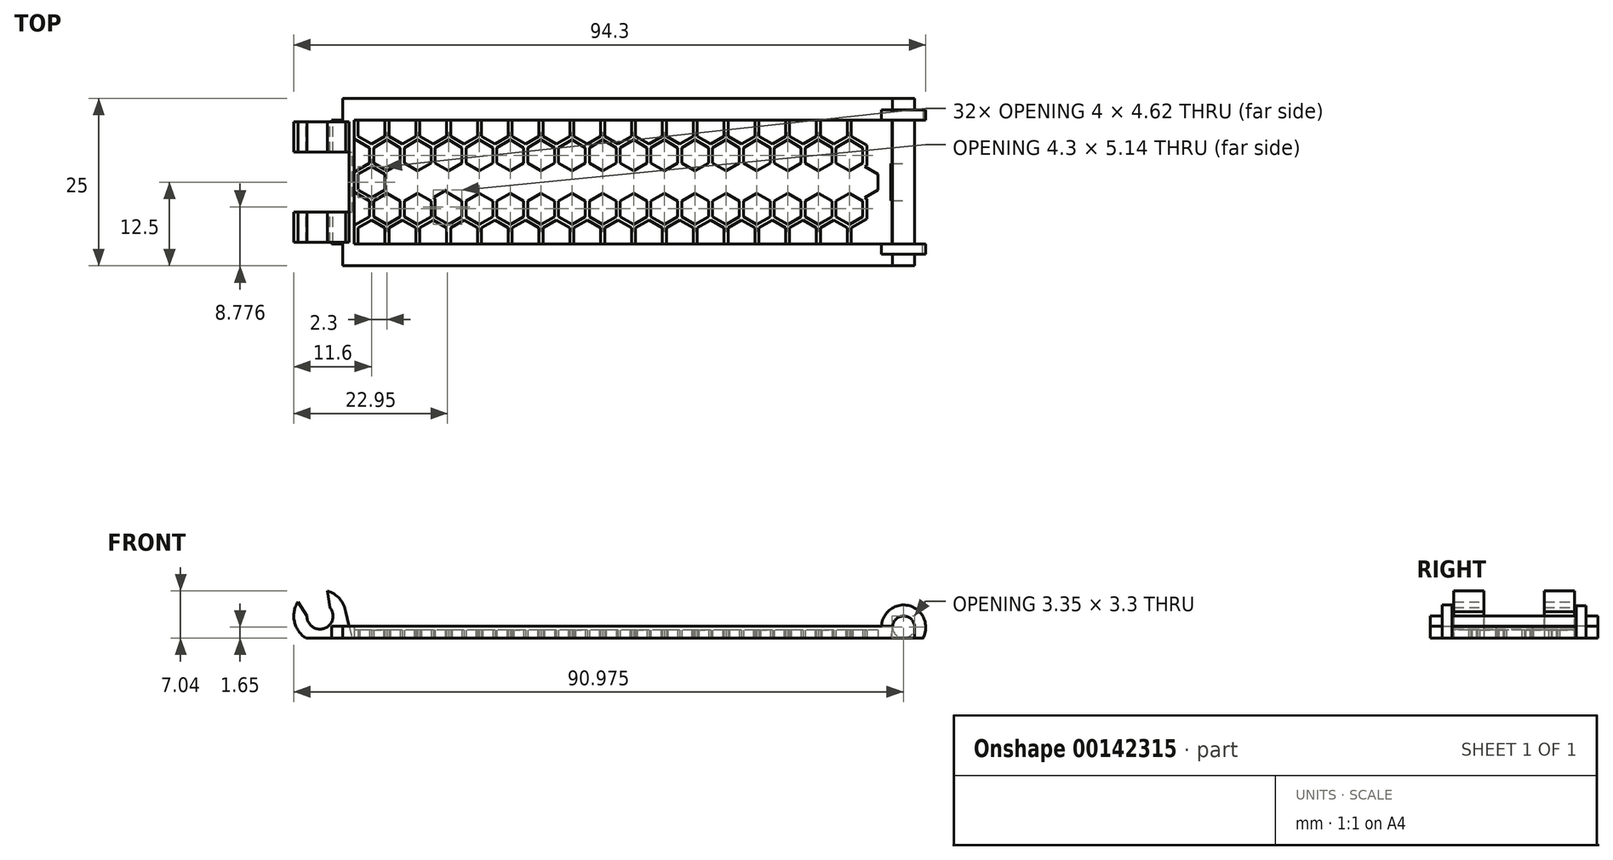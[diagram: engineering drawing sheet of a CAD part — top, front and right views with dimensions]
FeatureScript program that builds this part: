
annotation { "Feature Type Name" : "Feature", "Feature Type Description" : "" }
export const myFeature = defineFeature(function(context is Context, id is Id, definition is map)
    precondition{}
    {
        {
            var Q0;
            Q0=qCreatedBy(makeId("Top.planeOp"),FACE);
            var sketch = newSketch(context, id + "F0", { "sketchPlane" : qUnion([Q0])});
            skLineSegment(sketch, "E0.bottom", {"start": v(-40.15, -9.25) * mm, "end": v(40.15, -9.25) * mm});
            skLineSegment(sketch, "E0.top", {"start": v(-40.15, 9.25) * mm, "end": v(40.15, 9.25) * mm});
            skLineSegment(sketch, "E0.left", {"start": v(-40.15, -9.25) * mm, "end": v(-40.15, 9.25) * mm});
            skLineSegment(sketch, "E0.right", {"start": v(40.15, -9.25) * mm, "end": v(40.15, 9.25) * mm});
            skLineSegment(sketch, "E1.bottom", {"start": v(-43.5, -12.5) * mm, "end": v(43.5, -12.5) * mm});
            skLineSegment(sketch, "E1.top", {"start": v(-43.5, 12.5) * mm, "end": v(43.5, 12.5) * mm});
            skLineSegment(sketch, "E1.left", {"start": v(-43.5, -12.5) * mm, "end": v(-43.5, 12.5) * mm});
            skLineSegment(sketch, "E1.right", {"start": v(43.5, -12.5) * mm, "end": v(43.5, 12.5) * mm});
            skLineSegment(sketch, "E2", {"start": v(-43.5, -9.25) * mm, "end": v(-41.85, -9.25) * mm});
            skLineSegment(sketch, "E3", {"start": v(-41.85, -9.25) * mm, "end": v(-41.85, -12.5) * mm});
            skLineSegment(sketch, "E4", {"start": v(-56.32, 0) * mm, "end": v(-53.02, 0) * mm, "construction": true});
            skLineSegment(sketch, "E5.MirrorCS", {"start": v(-43.5, 9.25) * mm, "end": v(-41.85, 9.25) * mm});
            skLineSegment(sketch, "E6.MirrorCS", {"start": v(-41.85, 9.25) * mm, "end": v(-41.85, 12.5) * mm});
            skSolve(sketch);
        }
        {
            var Q0;
            Q0=makeQuery(id+"F0.imprint","IMPRINT",FACE,{"disambiguationData":[TD([[makeQuery(id+"F0.imprint","IMPRINT",EDGE,{"derivedFrom":sQuery(id+"F0.wireOp",EDGE,"E0.bottom")}),-1.0]])]});
            extrude(context, id + "F1", {"entities" : qUnion([Q0]), "depth" : 1.8 * mm});
        }
        {
            var Q0;
            Q0=qCreatedBy(makeId("Top.planeOp"),FACE);
            var sketch = newSketch(context, id + "F2", { "sketchPlane" : qUnion([Q0])});
            skArc(sketch, "E7.cCircle", {"start": v(-38.85, -2.25) * mm, "mid": v(-34.95, 0) * mm, "end": v(-38.85, 2.25) * mm, "construction": true});
            skLineSegment(sketch, "E7.0", {"start": v(-40.15, -1.5) * mm, "end": v(-40.15, 0) * mm});
            skLineSegment(sketch, "E7.1", {"start": v(-40.15, 1.5) * mm, "end": v(-37.85, 2.83) * mm});
            skLineSegment(sketch, "E7.2", {"start": v(-36.25, 2.25) * mm, "end": v(-35.25, 1.67) * mm});
            skLineSegment(sketch, "E7.4", {"start": v(-35.25, -1.67) * mm, "end": v(-37.25, -2.83) * mm});
            skPoint(sketch, "E7.0.midPoint", {"position": v(-40.15, 0) * mm});
            skLineSegment(sketch, "E8.0", {"start": v(-39.55, -1.15) * mm, "end": v(-39.55, 1.15) * mm});
            skLineSegment(sketch, "E8.1", {"start": v(-39.55, 1.15) * mm, "end": v(-37.55, 2.3) * mm});
            skLineSegment(sketch, "E8.2", {"start": v(-37.55, 2.3) * mm, "end": v(-35.55, 1.15) * mm});
            skLineSegment(sketch, "E8.3", {"start": v(-35.55, 1.15) * mm, "end": v(-35.55, -1.15) * mm});
            skLineSegment(sketch, "E8.4", {"start": v(-35.55, -1.15) * mm, "end": v(-37.55, -2.3) * mm});
            skLineSegment(sketch, "E8.5", {"start": v(-37.55, -2.3) * mm, "end": v(-39.55, -1.15) * mm});
            skPoint(sketch, "E8.0.midPoint", {"position": v(-39.55, 0) * mm});
            skPoint(sketch, "E9.MirrorP", {"position": v(-36.55, 6.24) * mm});
            skPoint(sketch, "E10.MirrorP", {"position": v(-36.25, 5.72) * mm});
            skLineSegment(sketch, "E11.MirrorCS", {"start": v(-35.25, 1.67) * mm, "end": v(-33.25, 2.83) * mm});
            skLineSegment(sketch, "E12.MirrorCS", {"start": v(-37.25, 2.83) * mm, "end": v(-35.25, 1.67) * mm});
            skLineSegment(sketch, "E13.MirrorCS", {"start": v(-37.25, 5.14) * mm, "end": v(-37.25, 2.83) * mm});
            skLineSegment(sketch, "E14.MirrorCS", {"start": v(-35.25, 6.3) * mm, "end": v(-37.25, 5.14) * mm});
            skCircle(sketch, "E15.MirrorC", {"center": v(-35.25, 3.98) * mm, "radius": 2 * mm, "construction": true});
            skLineSegment(sketch, "E16.MirrorCS", {"start": v(-33.25, 2.83) * mm, "end": v(-33.25, 5.14) * mm});
            skLineSegment(sketch, "E17.MirrorCS", {"start": v(-33.25, 5.14) * mm, "end": v(-35.25, 6.3) * mm});
            skCircle(sketch, "E18.MirrorC", {"center": v(-35.25, 3.98) * mm, "radius": 2.6 * mm, "construction": true});
            skLineSegment(sketch, "E19.MirrorCS", {"start": v(-35.55, 6.81) * mm, "end": v(-37.55, 5.66) * mm});
            skLineSegment(sketch, "E20.MirrorCS", {"start": v(-32.65, 2.48) * mm, "end": v(-32.65, 5.48) * mm});
            skLineSegment(sketch, "E21.MirrorCS", {"start": v(-32.65, 5.48) * mm, "end": v(-34.95, 6.81) * mm});
            skLineSegment(sketch, "E22.MirrorCS", {"start": v(-39.55, 6.81) * mm, "end": v(-39.55, 9.12) * mm});
            skLineSegment(sketch, "E23.MirrorCS", {"start": v(-40.15, 6.81) * mm, "end": v(-40.15, 9.12) * mm});
            skLineSegment(sketch, "E24.MirrorCS", {"start": v(-39.55, 9.12) * mm, "end": v(-39.33, 9.25) * mm});
            skLineSegment(sketch, "E25.MirrorCS", {"start": v(-35.77, 9.25) * mm, "end": v(-35.55, 9.12) * mm});
            skLineSegment(sketch, "E26.MirrorCS", {"start": v(-37.55, 5.66) * mm, "end": v(-39.55, 6.81) * mm});
            skLineSegment(sketch, "E27.MirrorCS", {"start": v(-35.55, 9.12) * mm, "end": v(-35.55, 6.81) * mm});
            skLineSegment(sketch, "E28.MirrorCS", {"start": v(-34.95, 9.25) * mm, "end": v(-34.95, 6.81) * mm});
            skLineSegment(sketch, "E29.MirrorCS", {"start": v(-40.15, 6.47) * mm, "end": v(-40.15, 9.25) * mm});
            skCircle(sketch, "E30.MirrorC", {"center": v(-37.55, 7.97) * mm, "radius": 2.6 * mm, "construction": true});
            skCircle(sketch, "E31.MirrorC", {"center": v(-37.55, 7.97) * mm, "radius": 2 * mm, "construction": true});
            skCircle(sketch, "E32.MirrorC", {"center": v(-37.55, 0) * mm, "radius": 2 * mm, "construction": true});
            skLineSegment(sketch, "E33.MirrorCS", {"start": v(-34.95, 1.15) * mm, "end": v(-34.95, -1.15) * mm});
            skLineSegment(sketch, "E34.trimOffspring", {"start": v(-37.85, 5.14) * mm, "end": v(-40.15, 6.47) * mm});
            skLineSegment(sketch, "E35.trimOffspring", {"start": v(-37.85, 5.14) * mm, "end": v(-37.85, 2.83) * mm});
            skLineSegment(sketch, "E36", {"start": v(-34.95, 9.25) * mm, "end": v(-35.77, 9.25) * mm});
            skLineSegment(sketch, "E37.trimOffspring", {"start": v(-34.95, 1.15) * mm, "end": v(-32.65, 2.48) * mm});
            skPoint(sketch, "E38.orphan", {"position": v(-37.55, 3) * mm});
            skLineSegment(sketch, "E39.MirrorCS", {"start": v(-35.25, -6.3) * mm, "end": v(-37.25, -5.14) * mm});
            skLineSegment(sketch, "E40.MirrorCS", {"start": v(-35.55, -6.81) * mm, "end": v(-37.55, -5.66) * mm});
            skLineSegment(sketch, "E41.MirrorCS", {"start": v(-39.55, -9.12) * mm, "end": v(-39.33, -9.25) * mm});
            skLineSegment(sketch, "E42.MirrorCS", {"start": v(-37.25, -2.83) * mm, "end": v(-35.25, -1.67) * mm});
            skLineSegment(sketch, "E43.MirrorCS", {"start": v(-35.77, -9.25) * mm, "end": v(-35.55, -9.12) * mm});
            skLineSegment(sketch, "E44.MirrorCS", {"start": v(-37.55, -2.3) * mm, "end": v(-35.55, -1.15) * mm});
            skLineSegment(sketch, "E45.MirrorCS", {"start": v(-35.55, -1.15) * mm, "end": v(-35.55, 1.15) * mm});
            skPoint(sketch, "E46.MirrorP", {"position": v(-36.55, -6.24) * mm});
            skLineSegment(sketch, "E47.MirrorCS", {"start": v(-34.95, -1.15) * mm, "end": v(-34.95, 1.15) * mm});
            skPoint(sketch, "E48.MirrorP", {"position": v(-36.25, -5.72) * mm});
            skLineSegment(sketch, "E49.MirrorCS", {"start": v(-40.15, -1.5) * mm, "end": v(-37.85, -2.83) * mm});
            skLineSegment(sketch, "E50.MirrorCS", {"start": v(-39.55, -1.15) * mm, "end": v(-37.55, -2.3) * mm});
            skLineSegment(sketch, "E51.MirrorCS", {"start": v(-40.15, -6.81) * mm, "end": v(-40.15, -9.12) * mm});
            skLineSegment(sketch, "E52.MirrorCS", {"start": v(-37.85, -5.14) * mm, "end": v(-40.15, -6.47) * mm});
            skCircle(sketch, "E53.MirrorC", {"center": v(-35.25, -3.98) * mm, "radius": 2 * mm, "construction": true});
            skLineSegment(sketch, "E54.MirrorCS", {"start": v(-40.15, -6.47) * mm, "end": v(-40.15, -9.25) * mm});
            skLineSegment(sketch, "E55.MirrorCS", {"start": v(-35.25, -1.67) * mm, "end": v(-33.25, -2.83) * mm});
            skLineSegment(sketch, "E56.MirrorCS", {"start": v(-32.65, -2.48) * mm, "end": v(-32.65, -5.48) * mm});
            skLineSegment(sketch, "E57.MirrorCS", {"start": v(-34.95, -9.25) * mm, "end": v(-35.77, -9.25) * mm});
            skLineSegment(sketch, "E58.MirrorCS", {"start": v(-35.25, 1.67) * mm, "end": v(-37.25, 2.83) * mm});
            skCircle(sketch, "E59.MirrorC", {"center": v(-37.55, 0) * mm, "radius": 2.6 * mm, "construction": true});
            skLineSegment(sketch, "E60.MirrorCS", {"start": v(-37.25, -5.14) * mm, "end": v(-37.25, -2.83) * mm});
            skLineSegment(sketch, "E61.MirrorCS", {"start": v(-37.55, -5.66) * mm, "end": v(-39.55, -6.81) * mm});
            skCircle(sketch, "E62.MirrorC", {"center": v(-37.55, -7.97) * mm, "radius": 2 * mm, "construction": true});
            skLineSegment(sketch, "E63.MirrorCS", {"start": v(-37.55, 2.3) * mm, "end": v(-39.55, 1.15) * mm});
            skLineSegment(sketch, "E64.MirrorCS", {"start": v(-37.85, -5.14) * mm, "end": v(-37.85, -2.83) * mm});
            skLineSegment(sketch, "E65.MirrorCS", {"start": v(-40.15, 1.5) * mm, "end": v(-40.15, -1.5) * mm});
            skLineSegment(sketch, "E66.MirrorCS", {"start": v(-33.25, -2.83) * mm, "end": v(-33.25, -5.14) * mm});
            skLineSegment(sketch, "E67.MirrorCS", {"start": v(-39.55, -6.81) * mm, "end": v(-39.55, -9.12) * mm});
            skLineSegment(sketch, "E68.MirrorCS", {"start": v(-32.65, -5.48) * mm, "end": v(-34.95, -6.81) * mm});
            skCircle(sketch, "E69.MirrorC", {"center": v(-35.25, -3.98) * mm, "radius": 2.6 * mm, "construction": true});
            skLineSegment(sketch, "E70.MirrorCS", {"start": v(-33.25, -5.14) * mm, "end": v(-35.25, -6.3) * mm});
            skCircle(sketch, "E71.MirrorC", {"center": v(-37.55, -7.97) * mm, "radius": 2.6 * mm, "construction": true});
            skLineSegment(sketch, "E72.MirrorCS", {"start": v(-35.55, 1.15) * mm, "end": v(-37.55, 2.3) * mm});
            skPoint(sketch, "E73.MirrorP", {"position": v(-37.55, -3) * mm});
            skLineSegment(sketch, "E74.MirrorCS", {"start": v(-34.95, -1.15) * mm, "end": v(-32.65, -2.48) * mm});
            skLineSegment(sketch, "E75.MirrorCS", {"start": v(-39.55, 1.15) * mm, "end": v(-39.55, -1.15) * mm});
            skLineSegment(sketch, "E76.MirrorCS", {"start": v(-28.36, 0) * mm, "end": v(-28.36, -9.25) * mm});
            skLineSegment(sketch, "E77.MirrorCS", {"start": v(-35.55, -9.12) * mm, "end": v(-35.55, -6.81) * mm});
            skLineSegment(sketch, "E78.MirrorCS", {"start": v(-34.95, -9.25) * mm, "end": v(-34.95, -6.81) * mm});
            skPoint(sketch, "E79.orphan", {"position": v(-34.95, 1.5) * mm});
            skLineSegment(sketch, "E80.trimOffspring", {"start": v(-37.85, 2.83) * mm, "end": v(-40.15, 1.5) * mm});
            skLineSegment(sketch, "E81.trimOffspring", {"start": v(-37.85, -2.83) * mm, "end": v(-40.15, -1.5) * mm});
            skPoint(sketch, "E82.trimOffspring.end.orphan", {"position": v(-34.95, -1.5) * mm});
            skLineSegment(sketch, "E83.trimOffspring", {"start": v(-39.33, -9.25) * mm, "end": v(-40.15, -9.25) * mm});
            skLineSegment(sketch, "E84.trimOffspring", {"start": v(-36.02, 9.25) * mm, "end": v(-40.15, 9.25) * mm});
            skPoint(sketch, "E85.1.0.0", {"position": v(-30.35, -1.5) * mm});
            skPoint(sketch, "E85.1.0.1", {"position": v(-31.65, -5.72) * mm});
            skCircle(sketch, "E85.1.0.2", {"center": v(-32.95, 0) * mm, "radius": 2 * mm, "construction": true});
            skPoint(sketch, "E85.1.0.3", {"position": v(-32.95, 3) * mm});
            skPoint(sketch, "E85.1.0.4", {"position": v(-31.95, -6.24) * mm});
            skPoint(sketch, "E85.1.0.5", {"position": v(-30.35, 1.5) * mm});
            skCircle(sketch, "E85.1.0.6", {"center": v(-32.95, 0) * mm, "radius": 2.6 * mm, "construction": true});
            skPoint(sketch, "E85.1.0.7", {"position": v(-31.95, 6.24) * mm});
            skPoint(sketch, "E85.1.0.8", {"position": v(-32.95, -3) * mm});
            skCircle(sketch, "E85.1.0.9", {"center": v(-32.95, -7.97) * mm, "radius": 2.6 * mm, "construction": true});
            skPoint(sketch, "E85.1.0.10", {"position": v(-31.65, 5.72) * mm});
            skCircle(sketch, "E85.1.0.11", {"center": v(-30.65, -3.98) * mm, "radius": 2.6 * mm, "construction": true});
            skCircle(sketch, "E85.1.0.12", {"center": v(-30.65, 3.98) * mm, "radius": 2.6 * mm, "construction": true});
            skCircle(sketch, "E85.1.0.13", {"center": v(-32.95, 7.97) * mm, "radius": 2 * mm, "construction": true});
            skCircle(sketch, "E85.1.0.14", {"center": v(-30.65, -3.98) * mm, "radius": 2 * mm, "construction": true});
            skLineSegment(sketch, "E85.1.0.15", {"start": v(-31.42, 9.25) * mm, "end": v(-35.55, 9.25) * mm});
            skPoint(sketch, "E85.1.0.16", {"position": v(-35.55, 0) * mm});
            skCircle(sketch, "E85.1.0.17", {"center": v(-32.95, 7.97) * mm, "radius": 2.6 * mm, "construction": true});
            skCircle(sketch, "E85.1.0.18", {"center": v(-30.65, 3.98) * mm, "radius": 2 * mm, "construction": true});
            skCircle(sketch, "E85.1.0.19", {"center": v(-32.95, -7.97) * mm, "radius": 2 * mm, "construction": true});
            skArc(sketch, "E85.1.0.20", {"start": v(-34.25, -2.25) * mm, "mid": v(-30.35, 0) * mm, "end": v(-34.25, 2.25) * mm, "construction": true});
            skPoint(sketch, "E85.1.0.21", {"position": v(-32.95, 3) * mm});
            skCircle(sketch, "E85.1.0.22", {"center": v(-32.95, 0) * mm, "radius": 2 * mm, "construction": true});
            skPoint(sketch, "E85.1.0.23", {"position": v(-30.35, 1.5) * mm});
            skLineSegment(sketch, "E85.1.0.24", {"start": v(-35.55, 6.81) * mm, "end": v(-35.55, 9.12) * mm});
            skLineSegment(sketch, "E85.1.0.25", {"start": v(-33.25, 5.14) * mm, "end": v(-35.55, 6.47) * mm});
            skLineSegment(sketch, "E85.1.0.26", {"start": v(-34.95, 6.81) * mm, "end": v(-34.95, 9.12) * mm});
            skLineSegment(sketch, "E85.1.0.27", {"start": v(-28.05, 5.48) * mm, "end": v(-30.35, 6.81) * mm});
            skLineSegment(sketch, "E85.1.0.28", {"start": v(-28.05, 2.48) * mm, "end": v(-28.05, 5.48) * mm});
            skLineSegment(sketch, "E85.1.0.29", {"start": v(-28.05, -2.48) * mm, "end": v(-28.05, -5.48) * mm});
            skLineSegment(sketch, "E85.1.0.30", {"start": v(-35.55, -6.47) * mm, "end": v(-35.55, -9.25) * mm});
            skLineSegment(sketch, "E85.1.0.31", {"start": v(-28.05, -5.48) * mm, "end": v(-30.35, -6.81) * mm});
            skPoint(sketch, "E85.1.0.32", {"position": v(-31.65, -5.72) * mm});
            skLineSegment(sketch, "E85.1.0.33", {"start": v(-34.95, -6.81) * mm, "end": v(-34.95, -9.12) * mm});
            skPoint(sketch, "E85.1.0.34", {"position": v(-31.65, 5.72) * mm});
            skLineSegment(sketch, "E85.1.0.35", {"start": v(-28.65, -2.83) * mm, "end": v(-28.65, -5.14) * mm});
            skLineSegment(sketch, "E85.1.0.36", {"start": v(-28.65, 2.83) * mm, "end": v(-28.65, 5.14) * mm});
            skPoint(sketch, "E85.1.0.37", {"position": v(-31.95, 6.24) * mm});
            skLineSegment(sketch, "E85.1.0.38", {"start": v(-33.25, -5.14) * mm, "end": v(-35.55, -6.47) * mm});
            skPoint(sketch, "E85.1.0.39", {"position": v(-34.95, 0) * mm});
            skLineSegment(sketch, "E85.1.0.40", {"start": v(-30.35, 9.25) * mm, "end": v(-30.35, 6.81) * mm});
            skLineSegment(sketch, "E85.1.0.41", {"start": v(-30.35, -9.25) * mm, "end": v(-30.35, -6.81) * mm});
            skPoint(sketch, "E85.1.0.42", {"position": v(-35.55, 0) * mm});
            skPoint(sketch, "E85.1.0.43", {"position": v(-31.95, -6.24) * mm});
            skPoint(sketch, "E85.1.0.44", {"position": v(-32.95, -3) * mm});
            skLineSegment(sketch, "E85.1.0.45", {"start": v(-30.95, -9.12) * mm, "end": v(-30.95, -6.81) * mm});
            skLineSegment(sketch, "E85.1.0.46", {"start": v(-30.95, 9.12) * mm, "end": v(-30.95, 6.81) * mm});
            skPoint(sketch, "E85.1.0.47", {"position": v(-30.35, -1.5) * mm});
            skLineSegment(sketch, "E85.1.0.48", {"start": v(-35.55, 1.5) * mm, "end": v(-33.25, 2.83) * mm});
            skLineSegment(sketch, "E85.1.0.49", {"start": v(-32.65, 5.14) * mm, "end": v(-32.65, 2.83) * mm});
            skLineSegment(sketch, "E85.1.0.50", {"start": v(-30.65, 1.67) * mm, "end": v(-28.65, 2.83) * mm});
            skLineSegment(sketch, "E85.1.0.51", {"start": v(-32.95, -5.66) * mm, "end": v(-34.95, -6.81) * mm});
            skLineSegment(sketch, "E85.1.0.52", {"start": v(-33.25, 5.14) * mm, "end": v(-33.25, 2.83) * mm});
            skLineSegment(sketch, "E85.1.0.53", {"start": v(-32.65, -5.14) * mm, "end": v(-32.65, -2.83) * mm});
            skLineSegment(sketch, "E85.1.0.54", {"start": v(-30.35, -1.15) * mm, "end": v(-28.05, -2.48) * mm});
            skLineSegment(sketch, "E85.1.0.55", {"start": v(-30.35, -1.15) * mm, "end": v(-30.35, 1.15) * mm});
            skLineSegment(sketch, "E85.1.0.56", {"start": v(-30.35, -9.25) * mm, "end": v(-31.17, -9.25) * mm});
            skLineSegment(sketch, "E85.1.0.57", {"start": v(-30.65, -1.67) * mm, "end": v(-28.65, -2.83) * mm});
            skLineSegment(sketch, "E85.1.0.58", {"start": v(-28.65, -5.14) * mm, "end": v(-30.65, -6.3) * mm});
            skCircle(sketch, "E85.1.0.59", {"center": v(-32.95, 0) * mm, "radius": 2 * mm, "construction": true});
            skLineSegment(sketch, "E85.1.0.60", {"start": v(-34.95, -9.12) * mm, "end": v(-34.73, -9.25) * mm});
            skLineSegment(sketch, "E85.1.0.61", {"start": v(-28.65, 5.14) * mm, "end": v(-30.65, 6.3) * mm});
            skLineSegment(sketch, "E85.1.0.62", {"start": v(-33.25, -2.83) * mm, "end": v(-35.55, -1.5) * mm});
            skLineSegment(sketch, "E85.1.0.63", {"start": v(-35.55, 6.47) * mm, "end": v(-35.55, 9.25) * mm});
            skPoint(sketch, "E85.1.0.64", {"position": v(-34.95, 0) * mm});
            skLineSegment(sketch, "E85.1.0.65", {"start": v(-33.25, -5.14) * mm, "end": v(-33.25, -2.83) * mm});
            skLineSegment(sketch, "E85.1.0.66", {"start": v(-35.55, -6.81) * mm, "end": v(-35.55, -9.12) * mm});
            skLineSegment(sketch, "E85.1.0.67", {"start": v(-30.35, 1.15) * mm, "end": v(-28.05, 2.48) * mm});
            skLineSegment(sketch, "E85.1.0.68", {"start": v(-32.95, 5.66) * mm, "end": v(-34.95, 6.81) * mm});
            skLineSegment(sketch, "E85.1.0.69", {"start": v(-35.55, -1.5) * mm, "end": v(-35.55, 0) * mm});
            skLineSegment(sketch, "E85.1.0.70", {"start": v(-31.17, 9.25) * mm, "end": v(-30.95, 9.12) * mm});
            skLineSegment(sketch, "E85.1.0.71", {"start": v(-34.95, 9.12) * mm, "end": v(-34.73, 9.25) * mm});
            skLineSegment(sketch, "E85.1.0.72", {"start": v(-30.35, -1.15) * mm, "end": v(-30.35, 1.15) * mm});
            skLineSegment(sketch, "E85.1.0.73", {"start": v(-35.55, 1.5) * mm, "end": v(-33.25, 2.83) * mm});
            skLineSegment(sketch, "E85.1.0.74", {"start": v(-30.65, -6.3) * mm, "end": v(-32.65, -5.14) * mm});
            skLineSegment(sketch, "E85.1.0.75", {"start": v(-31.17, -9.25) * mm, "end": v(-30.95, -9.12) * mm});
            skLineSegment(sketch, "E85.1.0.76", {"start": v(-30.95, 6.81) * mm, "end": v(-32.95, 5.66) * mm});
            skLineSegment(sketch, "E85.1.0.77", {"start": v(-30.95, -6.81) * mm, "end": v(-32.95, -5.66) * mm});
            skLineSegment(sketch, "E85.1.0.78", {"start": v(-34.73, -9.25) * mm, "end": v(-35.55, -9.25) * mm});
            skLineSegment(sketch, "E85.1.0.79", {"start": v(-30.65, 6.3) * mm, "end": v(-32.65, 5.14) * mm});
            skCircle(sketch, "E85.1.0.80", {"center": v(-32.95, 0) * mm, "radius": 2 * mm, "construction": true});
            skLineSegment(sketch, "E85.1.0.81", {"start": v(-30.35, 9.25) * mm, "end": v(-31.17, 9.25) * mm});
            skLineSegment(sketch, "E85.1.0.82", {"start": v(-35.55, -1.5) * mm, "end": v(-33.25, -2.83) * mm});
            skLineSegment(sketch, "E85.1.0.83", {"start": v(-30.95, 1.15) * mm, "end": v(-30.95, -1.15) * mm});
            skLineSegment(sketch, "E85.1.0.85", {"start": v(-30.35, 1.15) * mm, "end": v(-30.35, -1.15) * mm});
            skLineSegment(sketch, "E85.1.0.86", {"start": v(-30.95, 6.81) * mm, "end": v(-32.95, 5.66) * mm});
            skLineSegment(sketch, "E85.1.0.87", {"start": v(-30.95, -6.81) * mm, "end": v(-32.95, -5.66) * mm});
            skLineSegment(sketch, "E85.1.0.88", {"start": v(-30.65, -6.3) * mm, "end": v(-32.65, -5.14) * mm});
            skLineSegment(sketch, "E85.1.0.89", {"start": v(-35.55, 1.5) * mm, "end": v(-35.55, -1.5) * mm});
            skLineSegment(sketch, "E85.1.0.90", {"start": v(-33.25, 2.83) * mm, "end": v(-35.55, 1.5) * mm});
            skLineSegment(sketch, "E85.1.0.91", {"start": v(-30.65, 6.3) * mm, "end": v(-32.65, 5.14) * mm});
            skLineSegment(sketch, "E85.1.0.92", {"start": v(-35.55, -1.5) * mm, "end": v(-33.25, -2.83) * mm});
            skLineSegment(sketch, "E85.1.0.93", {"start": v(-32.95, -2.3) * mm, "end": v(-34.95, -1.15) * mm});
            skLineSegment(sketch, "E85.1.0.94", {"start": v(-31.65, 2.25) * mm, "end": v(-30.65, 1.67) * mm});
            skLineSegment(sketch, "E85.1.0.95", {"start": v(-32.65, 2.83) * mm, "end": v(-30.65, 1.67) * mm});
            skLineSegment(sketch, "E85.1.0.97", {"start": v(-30.95, -1.15) * mm, "end": v(-30.95, 1.15) * mm});
            skLineSegment(sketch, "E85.1.0.98", {"start": v(-30.35, 1.15) * mm, "end": v(-30.35, -1.15) * mm});
            skLineSegment(sketch, "E85.1.0.99", {"start": v(-30.95, -1.15) * mm, "end": v(-32.95, -2.3) * mm});
            skLineSegment(sketch, "E85.1.0.100", {"start": v(-34.95, 1.15) * mm, "end": v(-32.95, 2.3) * mm});
            skLineSegment(sketch, "E85.1.0.101", {"start": v(-30.65, -1.67) * mm, "end": v(-32.65, -2.83) * mm});
            skLineSegment(sketch, "E85.1.0.102", {"start": v(-30.65, 1.67) * mm, "end": v(-32.65, 2.83) * mm});
            skLineSegment(sketch, "E85.1.0.103", {"start": v(-30.95, 1.15) * mm, "end": v(-30.95, -1.15) * mm});
            skLineSegment(sketch, "E85.1.0.104", {"start": v(-34.95, -1.15) * mm, "end": v(-32.95, -2.3) * mm});
            skLineSegment(sketch, "E85.1.0.105", {"start": v(-32.95, 2.3) * mm, "end": v(-30.95, 1.15) * mm});
            skLineSegment(sketch, "E85.1.0.106", {"start": v(-32.95, -2.3) * mm, "end": v(-30.95, -1.15) * mm});
            skLineSegment(sketch, "E85.1.0.107", {"start": v(-32.65, -2.83) * mm, "end": v(-30.65, -1.67) * mm});
            skLineSegment(sketch, "E85.1.0.108", {"start": v(-34.95, 1.15) * mm, "end": v(-32.95, 2.3) * mm});
            skLineSegment(sketch, "E85.1.0.109", {"start": v(-30.95, -1.15) * mm, "end": v(-30.95, 1.15) * mm});
            skLineSegment(sketch, "E85.1.0.110", {"start": v(-34.95, -1.15) * mm, "end": v(-32.95, -2.3) * mm});
            skLineSegment(sketch, "E85.1.0.111", {"start": v(-30.95, 1.15) * mm, "end": v(-32.95, 2.3) * mm});
            skLineSegment(sketch, "E85.1.0.112", {"start": v(-32.95, -2.3) * mm, "end": v(-30.95, -1.15) * mm});
            skLineSegment(sketch, "E85.1.0.113", {"start": v(-32.65, -2.83) * mm, "end": v(-30.65, -1.67) * mm});
            skLineSegment(sketch, "E85.1.0.114", {"start": v(-32.95, 2.3) * mm, "end": v(-34.95, 1.15) * mm});
            skLineSegment(sketch, "E85.1.0.115", {"start": v(-32.95, 2.3) * mm, "end": v(-30.95, 1.15) * mm});
            skPoint(sketch, "E85.2.0.0", {"position": v(-25.75, -1.5) * mm});
            skPoint(sketch, "E85.2.0.1", {"position": v(-27.05, -5.72) * mm});
            skCircle(sketch, "E85.2.0.2", {"center": v(-28.35, 0) * mm, "radius": 2 * mm, "construction": true});
            skPoint(sketch, "E85.2.0.3", {"position": v(-28.35, 3) * mm});
            skPoint(sketch, "E85.2.0.4", {"position": v(-27.35, -6.24) * mm});
            skPoint(sketch, "E85.2.0.5", {"position": v(-25.75, 1.5) * mm});
            skCircle(sketch, "E85.2.0.6", {"center": v(-28.35, 0) * mm, "radius": 2.6 * mm, "construction": true});
            skPoint(sketch, "E85.2.0.7", {"position": v(-27.35, 6.24) * mm});
            skPoint(sketch, "E85.2.0.8", {"position": v(-28.35, -3) * mm});
            skCircle(sketch, "E85.2.0.9", {"center": v(-28.35, -7.97) * mm, "radius": 2.6 * mm, "construction": true});
            skPoint(sketch, "E85.2.0.10", {"position": v(-27.05, 5.72) * mm});
            skCircle(sketch, "E85.2.0.11", {"center": v(-26.05, -3.98) * mm, "radius": 2.6 * mm, "construction": true});
            skCircle(sketch, "E85.2.0.12", {"center": v(-26.05, 3.98) * mm, "radius": 2.6 * mm, "construction": true});
            skCircle(sketch, "E85.2.0.13", {"center": v(-28.35, 7.97) * mm, "radius": 2 * mm, "construction": true});
            skCircle(sketch, "E85.2.0.14", {"center": v(-26.05, -3.98) * mm, "radius": 2 * mm, "construction": true});
            skLineSegment(sketch, "E85.2.0.15", {"start": v(-26.82, 9.25) * mm, "end": v(-30.95, 9.25) * mm});
            skPoint(sketch, "E85.2.0.16", {"position": v(-30.95, 0) * mm});
            skCircle(sketch, "E85.2.0.17", {"center": v(-28.35, 7.97) * mm, "radius": 2.6 * mm, "construction": true});
            skCircle(sketch, "E85.2.0.18", {"center": v(-26.05, 3.98) * mm, "radius": 2 * mm, "construction": true});
            skCircle(sketch, "E85.2.0.19", {"center": v(-28.35, -7.97) * mm, "radius": 2 * mm, "construction": true});
            skArc(sketch, "E85.2.0.20", {"start": v(-29.65, -2.25) * mm, "mid": v(-25.75, 0) * mm, "end": v(-29.65, 2.25) * mm, "construction": true});
            skPoint(sketch, "E85.2.0.21", {"position": v(-28.35, 3) * mm});
            skCircle(sketch, "E85.2.0.22", {"center": v(-28.35, 0) * mm, "radius": 2 * mm, "construction": true});
            skPoint(sketch, "E85.2.0.23", {"position": v(-25.75, 1.5) * mm});
            skLineSegment(sketch, "E85.2.0.24", {"start": v(-30.95, 6.81) * mm, "end": v(-30.95, 9.12) * mm});
            skLineSegment(sketch, "E85.2.0.25", {"start": v(-28.65, 5.14) * mm, "end": v(-30.95, 6.47) * mm});
            skLineSegment(sketch, "E85.2.0.26", {"start": v(-30.35, 6.81) * mm, "end": v(-30.35, 9.12) * mm});
            skLineSegment(sketch, "E85.2.0.27", {"start": v(-23.45, 5.48) * mm, "end": v(-25.75, 6.81) * mm});
            skLineSegment(sketch, "E85.2.0.28", {"start": v(-23.45, 2.48) * mm, "end": v(-23.45, 5.48) * mm});
            skLineSegment(sketch, "E85.2.0.29", {"start": v(-23.45, -2.48) * mm, "end": v(-23.45, -5.48) * mm});
            skLineSegment(sketch, "E85.2.0.30", {"start": v(-30.95, -6.47) * mm, "end": v(-30.95, -9.25) * mm});
            skLineSegment(sketch, "E85.2.0.31", {"start": v(-23.45, -5.48) * mm, "end": v(-25.75, -6.81) * mm});
            skPoint(sketch, "E85.2.0.32", {"position": v(-27.05, -5.72) * mm});
            skLineSegment(sketch, "E85.2.0.33", {"start": v(-30.35, -6.81) * mm, "end": v(-30.35, -9.12) * mm});
            skPoint(sketch, "E85.2.0.34", {"position": v(-27.05, 5.72) * mm});
            skLineSegment(sketch, "E85.2.0.35", {"start": v(-24.05, -2.83) * mm, "end": v(-24.05, -5.14) * mm});
            skLineSegment(sketch, "E85.2.0.36", {"start": v(-24.05, 2.83) * mm, "end": v(-24.05, 5.14) * mm});
            skPoint(sketch, "E85.2.0.37", {"position": v(-27.35, 6.24) * mm});
            skLineSegment(sketch, "E85.2.0.38", {"start": v(-28.65, -5.14) * mm, "end": v(-30.95, -6.47) * mm});
            skPoint(sketch, "E85.2.0.39", {"position": v(-30.35, 0) * mm});
            skLineSegment(sketch, "E85.2.0.40", {"start": v(-25.75, 9.25) * mm, "end": v(-25.75, 6.81) * mm});
            skLineSegment(sketch, "E85.2.0.41", {"start": v(-25.75, -9.25) * mm, "end": v(-25.75, -6.81) * mm});
            skPoint(sketch, "E85.2.0.42", {"position": v(-30.95, 0) * mm});
            skPoint(sketch, "E85.2.0.43", {"position": v(-27.35, -6.24) * mm});
            skPoint(sketch, "E85.2.0.44", {"position": v(-28.35, -3) * mm});
            skLineSegment(sketch, "E85.2.0.45", {"start": v(-26.35, -9.12) * mm, "end": v(-26.35, -6.81) * mm});
            skLineSegment(sketch, "E85.2.0.46", {"start": v(-26.35, 9.12) * mm, "end": v(-26.35, 6.81) * mm});
            skPoint(sketch, "E85.2.0.47", {"position": v(-25.75, -1.5) * mm});
            skLineSegment(sketch, "E85.2.0.48", {"start": v(-30.95, 1.5) * mm, "end": v(-28.65, 2.83) * mm});
            skLineSegment(sketch, "E85.2.0.49", {"start": v(-28.05, 5.14) * mm, "end": v(-28.05, 2.83) * mm});
            skLineSegment(sketch, "E85.2.0.50", {"start": v(-26.05, 1.67) * mm, "end": v(-24.05, 2.83) * mm});
            skLineSegment(sketch, "E85.2.0.51", {"start": v(-28.35, -5.66) * mm, "end": v(-30.35, -6.81) * mm});
            skLineSegment(sketch, "E85.2.0.52", {"start": v(-28.65, 5.14) * mm, "end": v(-28.65, 2.83) * mm});
            skLineSegment(sketch, "E85.2.0.53", {"start": v(-28.05, -5.14) * mm, "end": v(-28.05, -2.83) * mm});
            skLineSegment(sketch, "E85.2.0.54", {"start": v(-25.75, -1.15) * mm, "end": v(-23.45, -2.48) * mm});
            skLineSegment(sketch, "E85.2.0.55", {"start": v(-25.75, -1.15) * mm, "end": v(-25.75, 1.15) * mm});
            skLineSegment(sketch, "E85.2.0.56", {"start": v(-25.75, -9.25) * mm, "end": v(-26.57, -9.25) * mm});
            skLineSegment(sketch, "E85.2.0.57", {"start": v(-26.05, -1.67) * mm, "end": v(-24.05, -2.83) * mm});
            skLineSegment(sketch, "E85.2.0.58", {"start": v(-24.05, -5.14) * mm, "end": v(-26.05, -6.3) * mm});
            skCircle(sketch, "E85.2.0.59", {"center": v(-28.35, 0) * mm, "radius": 2 * mm, "construction": true});
            skLineSegment(sketch, "E85.2.0.60", {"start": v(-30.35, -9.12) * mm, "end": v(-30.13, -9.25) * mm});
            skLineSegment(sketch, "E85.2.0.61", {"start": v(-24.05, 5.14) * mm, "end": v(-26.05, 6.3) * mm});
            skLineSegment(sketch, "E85.2.0.62", {"start": v(-28.65, -2.83) * mm, "end": v(-30.95, -1.5) * mm});
            skLineSegment(sketch, "E85.2.0.63", {"start": v(-30.95, 6.47) * mm, "end": v(-30.95, 9.25) * mm});
            skPoint(sketch, "E85.2.0.64", {"position": v(-30.35, 0) * mm});
            skLineSegment(sketch, "E85.2.0.65", {"start": v(-28.65, -5.14) * mm, "end": v(-28.65, -2.83) * mm});
            skLineSegment(sketch, "E85.2.0.66", {"start": v(-30.95, -6.81) * mm, "end": v(-30.95, -9.12) * mm});
            skLineSegment(sketch, "E85.2.0.67", {"start": v(-25.75, 1.15) * mm, "end": v(-23.45, 2.48) * mm});
            skLineSegment(sketch, "E85.2.0.68", {"start": v(-28.35, 5.66) * mm, "end": v(-30.35, 6.81) * mm});
            skLineSegment(sketch, "E85.2.0.69", {"start": v(-30.95, -1.5) * mm, "end": v(-30.95, 0) * mm});
            skLineSegment(sketch, "E85.2.0.70", {"start": v(-26.57, 9.25) * mm, "end": v(-26.35, 9.12) * mm});
            skLineSegment(sketch, "E85.2.0.71", {"start": v(-30.35, 9.12) * mm, "end": v(-30.13, 9.25) * mm});
            skLineSegment(sketch, "E85.2.0.72", {"start": v(-25.75, -1.15) * mm, "end": v(-25.75, 1.15) * mm});
            skLineSegment(sketch, "E85.2.0.73", {"start": v(-30.95, 1.5) * mm, "end": v(-28.65, 2.83) * mm});
            skLineSegment(sketch, "E85.2.0.74", {"start": v(-26.05, -6.3) * mm, "end": v(-28.05, -5.14) * mm});
            skLineSegment(sketch, "E85.2.0.75", {"start": v(-26.57, -9.25) * mm, "end": v(-26.35, -9.12) * mm});
            skLineSegment(sketch, "E85.2.0.76", {"start": v(-26.35, 6.81) * mm, "end": v(-28.35, 5.66) * mm});
            skLineSegment(sketch, "E85.2.0.77", {"start": v(-26.35, -6.81) * mm, "end": v(-28.35, -5.66) * mm});
            skLineSegment(sketch, "E85.2.0.78", {"start": v(-30.13, -9.25) * mm, "end": v(-30.95, -9.25) * mm});
            skLineSegment(sketch, "E85.2.0.79", {"start": v(-26.05, 6.3) * mm, "end": v(-28.05, 5.14) * mm});
            skCircle(sketch, "E85.2.0.80", {"center": v(-28.35, 0) * mm, "radius": 2 * mm, "construction": true});
            skLineSegment(sketch, "E85.2.0.81", {"start": v(-25.75, 9.25) * mm, "end": v(-26.57, 9.25) * mm});
            skLineSegment(sketch, "E85.2.0.82", {"start": v(-30.95, -1.5) * mm, "end": v(-28.65, -2.83) * mm});
            skLineSegment(sketch, "E85.2.0.83", {"start": v(-26.35, 1.15) * mm, "end": v(-26.35, -1.15) * mm});
            skLineSegment(sketch, "E85.2.0.84", {"start": v(-30.35, -1.15) * mm, "end": v(-30.35, 1.15) * mm});
            skLineSegment(sketch, "E85.2.0.85", {"start": v(-25.75, 1.15) * mm, "end": v(-25.75, -1.15) * mm});
            skLineSegment(sketch, "E85.2.0.86", {"start": v(-26.35, 6.81) * mm, "end": v(-28.35, 5.66) * mm});
            skLineSegment(sketch, "E85.2.0.87", {"start": v(-26.35, -6.81) * mm, "end": v(-28.35, -5.66) * mm});
            skLineSegment(sketch, "E85.2.0.88", {"start": v(-26.05, -6.3) * mm, "end": v(-28.05, -5.14) * mm});
            skLineSegment(sketch, "E85.2.0.89", {"start": v(-30.95, 1.5) * mm, "end": v(-30.95, -1.5) * mm});
            skLineSegment(sketch, "E85.2.0.90", {"start": v(-28.65, 2.83) * mm, "end": v(-30.95, 1.5) * mm});
            skLineSegment(sketch, "E85.2.0.91", {"start": v(-26.05, 6.3) * mm, "end": v(-28.05, 5.14) * mm});
            skLineSegment(sketch, "E85.2.0.92", {"start": v(-30.95, -1.5) * mm, "end": v(-28.65, -2.83) * mm});
            skLineSegment(sketch, "E85.2.0.93", {"start": v(-28.35, -2.3) * mm, "end": v(-30.35, -1.15) * mm});
            skLineSegment(sketch, "E85.2.0.94", {"start": v(-27.05, 2.25) * mm, "end": v(-26.05, 1.67) * mm});
            skLineSegment(sketch, "E85.2.0.95", {"start": v(-28.05, 2.83) * mm, "end": v(-26.05, 1.67) * mm});
            skLineSegment(sketch, "E85.2.0.96", {"start": v(-30.35, 1.15) * mm, "end": v(-30.35, -1.15) * mm});
            skLineSegment(sketch, "E85.2.0.97", {"start": v(-26.35, -1.15) * mm, "end": v(-26.35, 1.15) * mm});
            skLineSegment(sketch, "E85.2.0.98", {"start": v(-25.75, 1.15) * mm, "end": v(-25.75, -1.15) * mm});
            skLineSegment(sketch, "E85.2.0.99", {"start": v(-26.35, -1.15) * mm, "end": v(-28.35, -2.3) * mm});
            skLineSegment(sketch, "E85.2.0.100", {"start": v(-30.35, 1.15) * mm, "end": v(-28.35, 2.3) * mm});
            skLineSegment(sketch, "E85.2.0.101", {"start": v(-26.05, -1.67) * mm, "end": v(-28.05, -2.83) * mm});
            skLineSegment(sketch, "E85.2.0.102", {"start": v(-26.05, 1.67) * mm, "end": v(-28.05, 2.83) * mm});
            skLineSegment(sketch, "E85.2.0.103", {"start": v(-26.35, 1.15) * mm, "end": v(-26.35, -1.15) * mm});
            skLineSegment(sketch, "E85.2.0.104", {"start": v(-30.35, -1.15) * mm, "end": v(-28.35, -2.3) * mm});
            skLineSegment(sketch, "E85.2.0.105", {"start": v(-28.35, 2.3) * mm, "end": v(-26.35, 1.15) * mm});
            skLineSegment(sketch, "E85.2.0.106", {"start": v(-28.35, -2.3) * mm, "end": v(-26.35, -1.15) * mm});
            skLineSegment(sketch, "E85.2.0.107", {"start": v(-28.05, -2.83) * mm, "end": v(-26.05, -1.67) * mm});
            skLineSegment(sketch, "E85.2.0.108", {"start": v(-30.35, 1.15) * mm, "end": v(-28.35, 2.3) * mm});
            skLineSegment(sketch, "E85.2.0.109", {"start": v(-26.35, -1.15) * mm, "end": v(-26.35, 1.15) * mm});
            skLineSegment(sketch, "E85.2.0.110", {"start": v(-30.35, -1.15) * mm, "end": v(-28.35, -2.3) * mm});
            skLineSegment(sketch, "E85.2.0.111", {"start": v(-26.35, 1.15) * mm, "end": v(-28.35, 2.3) * mm});
            skLineSegment(sketch, "E85.2.0.112", {"start": v(-28.35, -2.3) * mm, "end": v(-26.35, -1.15) * mm});
            skLineSegment(sketch, "E85.2.0.113", {"start": v(-28.05, -2.83) * mm, "end": v(-26.05, -1.67) * mm});
            skLineSegment(sketch, "E85.2.0.114", {"start": v(-28.35, 2.3) * mm, "end": v(-30.35, 1.15) * mm});
            skLineSegment(sketch, "E85.2.0.115", {"start": v(-28.35, 2.3) * mm, "end": v(-26.35, 1.15) * mm});
            skLineSegment(sketch, "E85.direction1", {"start": v(-40.15, -9.25) * mm, "end": v(-35.55, -9.25) * mm, "construction": true});
            skPoint(sketch, "E86.0.3.0", {"position": v(-21.15, -1.5) * mm});
            skPoint(sketch, "E86.1.3.0", {"position": v(-22.45, -5.72) * mm});
            skCircle(sketch, "E86.2.3.0", {"center": v(-23.75, 0) * mm, "radius": 2 * mm, "construction": true});
            skPoint(sketch, "E86.4.3.0", {"position": v(-23.75, 3) * mm});
            skPoint(sketch, "E86.5.3.0", {"position": v(-22.75, -6.24) * mm});
            skPoint(sketch, "E86.6.3.0", {"position": v(-21.15, 1.5) * mm});
            skCircle(sketch, "E86.7.3.0", {"center": v(-23.75, 0) * mm, "radius": 2.6 * mm, "construction": true});
            skPoint(sketch, "E86.9.3.0", {"position": v(-22.75, 6.24) * mm});
            skPoint(sketch, "E86.10.3.0", {"position": v(-23.75, -3) * mm});
            skCircle(sketch, "E86.11.3.0", {"center": v(-23.75, -7.97) * mm, "radius": 2.6 * mm, "construction": true});
            skPoint(sketch, "E86.13.3.0", {"position": v(-22.45, 5.72) * mm});
            skCircle(sketch, "E86.14.3.0", {"center": v(-21.45, -3.98) * mm, "radius": 2.6 * mm, "construction": true});
            skCircle(sketch, "E86.16.3.0", {"center": v(-21.45, 3.98) * mm, "radius": 2.6 * mm, "construction": true});
            skCircle(sketch, "E86.18.3.0", {"center": v(-23.75, 7.97) * mm, "radius": 2 * mm, "construction": true});
            skCircle(sketch, "E86.20.3.0", {"center": v(-21.45, -3.98) * mm, "radius": 2 * mm, "construction": true});
            skLineSegment(sketch, "E86.22.3.0", {"start": v(-22.22, 9.25) * mm, "end": v(-26.35, 9.25) * mm});
            skPoint(sketch, "E86.25.3.0", {"position": v(-26.35, 0) * mm});
            skCircle(sketch, "E86.26.3.0", {"center": v(-23.75, 7.97) * mm, "radius": 2.6 * mm, "construction": true});
            skCircle(sketch, "E86.28.3.0", {"center": v(-21.45, 3.98) * mm, "radius": 2 * mm, "construction": true});
            skCircle(sketch, "E86.30.3.0", {"center": v(-23.75, -7.97) * mm, "radius": 2 * mm, "construction": true});
            skArc(sketch, "E86.32.3.0", {"start": v(-25.05, -2.25) * mm, "mid": v(-21.15, 0) * mm, "end": v(-25.05, 2.25) * mm, "construction": true});
            skPoint(sketch, "E86.36.3.0", {"position": v(-23.75, 3) * mm});
            skCircle(sketch, "E86.37.3.0", {"center": v(-23.75, 0) * mm, "radius": 2 * mm, "construction": true});
            skPoint(sketch, "E86.39.3.0", {"position": v(-21.15, 1.5) * mm});
            skLineSegment(sketch, "E86.40.3.0", {"start": v(-26.35, 6.81) * mm, "end": v(-26.35, 9.12) * mm});
            skLineSegment(sketch, "E86.43.3.0", {"start": v(-24.05, 5.14) * mm, "end": v(-26.35, 6.47) * mm});
            skLineSegment(sketch, "E86.46.3.0", {"start": v(-25.75, 6.81) * mm, "end": v(-25.75, 9.12) * mm});
            skLineSegment(sketch, "E86.49.3.0", {"start": v(-18.85, 5.48) * mm, "end": v(-21.15, 6.81) * mm});
            skLineSegment(sketch, "E86.52.3.0", {"start": v(-18.85, 2.48) * mm, "end": v(-18.85, 5.48) * mm});
            skLineSegment(sketch, "E86.55.3.0", {"start": v(-18.85, -2.48) * mm, "end": v(-18.85, -5.48) * mm});
            skLineSegment(sketch, "E86.58.3.0", {"start": v(-26.35, -6.47) * mm, "end": v(-26.35, -9.25) * mm});
            skLineSegment(sketch, "E86.61.3.0", {"start": v(-18.85, -5.48) * mm, "end": v(-21.15, -6.81) * mm});
            skPoint(sketch, "E86.64.3.0", {"position": v(-22.45, -5.72) * mm});
            skLineSegment(sketch, "E86.65.3.0", {"start": v(-25.75, -6.81) * mm, "end": v(-25.75, -9.12) * mm});
            skPoint(sketch, "E86.68.3.0", {"position": v(-22.45, 5.72) * mm});
            skLineSegment(sketch, "E86.69.3.0", {"start": v(-19.45, -2.83) * mm, "end": v(-19.45, -5.14) * mm});
            skLineSegment(sketch, "E86.72.3.0", {"start": v(-19.45, 2.83) * mm, "end": v(-19.45, 5.14) * mm});
            skPoint(sketch, "E86.75.3.0", {"position": v(-22.75, 6.24) * mm});
            skLineSegment(sketch, "E86.76.3.0", {"start": v(-24.05, -5.14) * mm, "end": v(-26.35, -6.47) * mm});
            skPoint(sketch, "E86.79.3.0", {"position": v(-25.75, 0) * mm});
            skLineSegment(sketch, "E86.80.3.0", {"start": v(-21.15, 9.25) * mm, "end": v(-21.15, 6.81) * mm});
            skLineSegment(sketch, "E86.83.3.0", {"start": v(-21.15, -9.25) * mm, "end": v(-21.15, -6.81) * mm});
            skPoint(sketch, "E86.86.3.0", {"position": v(-26.35, 0) * mm});
            skPoint(sketch, "E86.87.3.0", {"position": v(-22.75, -6.24) * mm});
            skPoint(sketch, "E86.88.3.0", {"position": v(-23.75, -3) * mm});
            skLineSegment(sketch, "E86.89.3.0", {"start": v(-21.75, -9.12) * mm, "end": v(-21.75, -6.81) * mm});
            skLineSegment(sketch, "E86.92.3.0", {"start": v(-21.75, 9.12) * mm, "end": v(-21.75, 6.81) * mm});
            skPoint(sketch, "E86.95.3.0", {"position": v(-21.15, -1.5) * mm});
            skLineSegment(sketch, "E86.96.3.0", {"start": v(-26.35, 1.5) * mm, "end": v(-24.05, 2.83) * mm});
            skLineSegment(sketch, "E86.99.3.0", {"start": v(-23.45, 5.14) * mm, "end": v(-23.45, 2.83) * mm});
            skLineSegment(sketch, "E86.102.3.0", {"start": v(-21.45, 1.67) * mm, "end": v(-19.45, 2.83) * mm});
            skLineSegment(sketch, "E86.105.3.0", {"start": v(-23.75, -5.66) * mm, "end": v(-25.75, -6.81) * mm});
            skLineSegment(sketch, "E86.108.3.0", {"start": v(-24.05, 5.14) * mm, "end": v(-24.05, 2.83) * mm});
            skLineSegment(sketch, "E86.111.3.0", {"start": v(-23.45, -5.14) * mm, "end": v(-23.45, -2.83) * mm});
            skLineSegment(sketch, "E86.114.3.0", {"start": v(-21.15, -1.15) * mm, "end": v(-18.85, -2.48) * mm});
            skLineSegment(sketch, "E86.117.3.0", {"start": v(-21.15, -1.15) * mm, "end": v(-21.15, 1.15) * mm});
            skLineSegment(sketch, "E86.120.3.0", {"start": v(-21.15, -9.25) * mm, "end": v(-21.97, -9.25) * mm});
            skLineSegment(sketch, "E86.123.3.0", {"start": v(-21.45, -1.67) * mm, "end": v(-19.45, -2.83) * mm});
            skLineSegment(sketch, "E86.126.3.0", {"start": v(-19.45, -5.14) * mm, "end": v(-21.45, -6.3) * mm});
            skCircle(sketch, "E86.129.3.0", {"center": v(-23.75, 0) * mm, "radius": 2 * mm, "construction": true});
            skLineSegment(sketch, "E86.131.3.0", {"start": v(-25.75, -9.12) * mm, "end": v(-25.53, -9.25) * mm});
            skLineSegment(sketch, "E86.134.3.0", {"start": v(-19.45, 5.14) * mm, "end": v(-21.45, 6.3) * mm});
            skLineSegment(sketch, "E86.137.3.0", {"start": v(-24.05, -2.83) * mm, "end": v(-26.35, -1.5) * mm});
            skLineSegment(sketch, "E86.140.3.0", {"start": v(-26.35, 6.47) * mm, "end": v(-26.35, 9.25) * mm});
            skPoint(sketch, "E86.143.3.0", {"position": v(-25.75, 0) * mm});
            skLineSegment(sketch, "E86.144.3.0", {"start": v(-24.05, -5.14) * mm, "end": v(-24.05, -2.83) * mm});
            skLineSegment(sketch, "E86.147.3.0", {"start": v(-26.35, -6.81) * mm, "end": v(-26.35, -9.12) * mm});
            skLineSegment(sketch, "E86.150.3.0", {"start": v(-21.15, 1.15) * mm, "end": v(-18.85, 2.48) * mm});
            skLineSegment(sketch, "E86.153.3.0", {"start": v(-23.75, 5.66) * mm, "end": v(-25.75, 6.81) * mm});
            skLineSegment(sketch, "E86.156.3.0", {"start": v(-26.35, -1.5) * mm, "end": v(-26.35, 0) * mm});
            skLineSegment(sketch, "E86.159.3.0", {"start": v(-21.97, 9.25) * mm, "end": v(-21.75, 9.12) * mm});
            skLineSegment(sketch, "E86.162.3.0", {"start": v(-25.75, 9.12) * mm, "end": v(-25.53, 9.25) * mm});
            skLineSegment(sketch, "E86.165.3.0", {"start": v(-21.15, -1.15) * mm, "end": v(-21.15, 1.15) * mm});
            skLineSegment(sketch, "E86.168.3.0", {"start": v(-26.35, 1.5) * mm, "end": v(-24.05, 2.83) * mm});
            skLineSegment(sketch, "E86.171.3.0", {"start": v(-21.45, -6.3) * mm, "end": v(-23.45, -5.14) * mm});
            skLineSegment(sketch, "E86.174.3.0", {"start": v(-21.97, -9.25) * mm, "end": v(-21.75, -9.12) * mm});
            skLineSegment(sketch, "E86.177.3.0", {"start": v(-21.75, 6.81) * mm, "end": v(-23.75, 5.66) * mm});
            skLineSegment(sketch, "E86.180.3.0", {"start": v(-21.75, -6.81) * mm, "end": v(-23.75, -5.66) * mm});
            skLineSegment(sketch, "E86.183.3.0", {"start": v(-25.53, -9.25) * mm, "end": v(-26.35, -9.25) * mm});
            skLineSegment(sketch, "E86.186.3.0", {"start": v(-21.45, 6.3) * mm, "end": v(-23.45, 5.14) * mm});
            skCircle(sketch, "E86.189.3.0", {"center": v(-23.75, 0) * mm, "radius": 2 * mm, "construction": true});
            skLineSegment(sketch, "E86.191.3.0", {"start": v(-21.15, 9.25) * mm, "end": v(-21.97, 9.25) * mm});
            skLineSegment(sketch, "E86.194.3.0", {"start": v(-26.35, -1.5) * mm, "end": v(-24.05, -2.83) * mm});
            skLineSegment(sketch, "E86.197.3.0", {"start": v(-21.75, 1.15) * mm, "end": v(-21.75, -1.15) * mm});
            skLineSegment(sketch, "E86.203.3.0", {"start": v(-21.15, 1.15) * mm, "end": v(-21.15, -1.15) * mm});
            skLineSegment(sketch, "E86.206.3.0", {"start": v(-21.75, 6.81) * mm, "end": v(-23.75, 5.66) * mm});
            skLineSegment(sketch, "E86.209.3.0", {"start": v(-21.75, -6.81) * mm, "end": v(-23.75, -5.66) * mm});
            skLineSegment(sketch, "E86.212.3.0", {"start": v(-21.45, -6.3) * mm, "end": v(-23.45, -5.14) * mm});
            skLineSegment(sketch, "E86.215.3.0", {"start": v(-26.35, 1.5) * mm, "end": v(-26.35, -1.5) * mm});
            skLineSegment(sketch, "E86.218.3.0", {"start": v(-24.05, 2.83) * mm, "end": v(-26.35, 1.5) * mm});
            skLineSegment(sketch, "E86.221.3.0", {"start": v(-21.45, 6.3) * mm, "end": v(-23.45, 5.14) * mm});
            skLineSegment(sketch, "E86.224.3.0", {"start": v(-26.35, -1.5) * mm, "end": v(-24.05, -2.83) * mm});
            skLineSegment(sketch, "E86.227.3.0", {"start": v(-23.75, -2.3) * mm, "end": v(-25.75, -1.15) * mm});
            skLineSegment(sketch, "E86.230.3.0", {"start": v(-22.45, 2.25) * mm, "end": v(-21.45, 1.67) * mm});
            skLineSegment(sketch, "E86.233.3.0", {"start": v(-23.45, 2.83) * mm, "end": v(-21.45, 1.67) * mm});
            skLineSegment(sketch, "E86.239.3.0", {"start": v(-21.75, -1.15) * mm, "end": v(-21.75, 1.15) * mm});
            skLineSegment(sketch, "E86.242.3.0", {"start": v(-21.15, 1.15) * mm, "end": v(-21.15, -1.15) * mm});
            skLineSegment(sketch, "E86.245.3.0", {"start": v(-21.75, -1.15) * mm, "end": v(-23.75, -2.3) * mm});
            skLineSegment(sketch, "E86.248.3.0", {"start": v(-25.75, 1.15) * mm, "end": v(-23.75, 2.3) * mm});
            skLineSegment(sketch, "E86.251.3.0", {"start": v(-21.45, -1.67) * mm, "end": v(-23.45, -2.83) * mm});
            skLineSegment(sketch, "E86.254.3.0", {"start": v(-21.45, 1.67) * mm, "end": v(-23.45, 2.83) * mm});
            skLineSegment(sketch, "E86.257.3.0", {"start": v(-21.75, 1.15) * mm, "end": v(-21.75, -1.15) * mm});
            skLineSegment(sketch, "E86.260.3.0", {"start": v(-25.75, -1.15) * mm, "end": v(-23.75, -2.3) * mm});
            skLineSegment(sketch, "E86.263.3.0", {"start": v(-23.75, 2.3) * mm, "end": v(-21.75, 1.15) * mm});
            skLineSegment(sketch, "E86.266.3.0", {"start": v(-23.75, -2.3) * mm, "end": v(-21.75, -1.15) * mm});
            skLineSegment(sketch, "E86.269.3.0", {"start": v(-23.45, -2.83) * mm, "end": v(-21.45, -1.67) * mm});
            skLineSegment(sketch, "E86.272.3.0", {"start": v(-25.75, 1.15) * mm, "end": v(-23.75, 2.3) * mm});
            skLineSegment(sketch, "E86.275.3.0", {"start": v(-21.75, -1.15) * mm, "end": v(-21.75, 1.15) * mm});
            skLineSegment(sketch, "E86.278.3.0", {"start": v(-25.75, -1.15) * mm, "end": v(-23.75, -2.3) * mm});
            skLineSegment(sketch, "E86.281.3.0", {"start": v(-21.75, 1.15) * mm, "end": v(-23.75, 2.3) * mm});
            skLineSegment(sketch, "E86.284.3.0", {"start": v(-23.75, -2.3) * mm, "end": v(-21.75, -1.15) * mm});
            skLineSegment(sketch, "E86.287.3.0", {"start": v(-23.45, -2.83) * mm, "end": v(-21.45, -1.67) * mm});
            skLineSegment(sketch, "E86.290.3.0", {"start": v(-23.75, 2.3) * mm, "end": v(-25.75, 1.15) * mm});
            skLineSegment(sketch, "E86.293.3.0", {"start": v(-23.75, 2.3) * mm, "end": v(-21.75, 1.15) * mm});
            skPoint(sketch, "E86.0.4.0", {"position": v(-16.55, -1.5) * mm});
            skPoint(sketch, "E86.1.4.0", {"position": v(-17.85, -5.72) * mm});
            skCircle(sketch, "E86.2.4.0", {"center": v(-19.15, 0) * mm, "radius": 2 * mm, "construction": true});
            skPoint(sketch, "E86.4.4.0", {"position": v(-19.15, 3) * mm});
            skPoint(sketch, "E86.5.4.0", {"position": v(-18.15, -6.24) * mm});
            skPoint(sketch, "E86.6.4.0", {"position": v(-16.55, 1.5) * mm});
            skCircle(sketch, "E86.7.4.0", {"center": v(-19.15, 0) * mm, "radius": 2.6 * mm, "construction": true});
            skPoint(sketch, "E86.9.4.0", {"position": v(-18.15, 6.24) * mm});
            skPoint(sketch, "E86.10.4.0", {"position": v(-19.15, -3) * mm});
            skCircle(sketch, "E86.11.4.0", {"center": v(-19.15, -7.97) * mm, "radius": 2.6 * mm, "construction": true});
            skPoint(sketch, "E86.13.4.0", {"position": v(-17.85, 5.72) * mm});
            skCircle(sketch, "E86.14.4.0", {"center": v(-16.85, -3.98) * mm, "radius": 2.6 * mm, "construction": true});
            skCircle(sketch, "E86.16.4.0", {"center": v(-16.85, 3.98) * mm, "radius": 2.6 * mm, "construction": true});
            skCircle(sketch, "E86.18.4.0", {"center": v(-19.15, 7.97) * mm, "radius": 2 * mm, "construction": true});
            skCircle(sketch, "E86.20.4.0", {"center": v(-16.85, -3.98) * mm, "radius": 2 * mm, "construction": true});
            skLineSegment(sketch, "E86.22.4.0", {"start": v(-17.62, 9.25) * mm, "end": v(-21.75, 9.25) * mm});
            skPoint(sketch, "E86.25.4.0", {"position": v(-21.75, 0) * mm});
            skCircle(sketch, "E86.26.4.0", {"center": v(-19.15, 7.97) * mm, "radius": 2.6 * mm, "construction": true});
            skCircle(sketch, "E86.28.4.0", {"center": v(-16.85, 3.98) * mm, "radius": 2 * mm, "construction": true});
            skCircle(sketch, "E86.30.4.0", {"center": v(-19.15, -7.97) * mm, "radius": 2 * mm, "construction": true});
            skArc(sketch, "E86.32.4.0", {"start": v(-20.45, -2.25) * mm, "mid": v(-16.55, 0) * mm, "end": v(-20.45, 2.25) * mm, "construction": true});
            skPoint(sketch, "E86.36.4.0", {"position": v(-19.15, 3) * mm});
            skCircle(sketch, "E86.37.4.0", {"center": v(-19.15, 0) * mm, "radius": 2 * mm, "construction": true});
            skPoint(sketch, "E86.39.4.0", {"position": v(-16.55, 1.5) * mm});
            skLineSegment(sketch, "E86.40.4.0", {"start": v(-21.75, 6.81) * mm, "end": v(-21.75, 9.12) * mm});
            skLineSegment(sketch, "E86.43.4.0", {"start": v(-19.45, 5.14) * mm, "end": v(-21.75, 6.47) * mm});
            skLineSegment(sketch, "E86.46.4.0", {"start": v(-21.15, 6.81) * mm, "end": v(-21.15, 9.12) * mm});
            skLineSegment(sketch, "E86.49.4.0", {"start": v(-14.25, 5.48) * mm, "end": v(-16.55, 6.81) * mm});
            skLineSegment(sketch, "E86.52.4.0", {"start": v(-14.25, 2.48) * mm, "end": v(-14.25, 5.48) * mm});
            skLineSegment(sketch, "E86.55.4.0", {"start": v(-14.25, -2.48) * mm, "end": v(-14.25, -5.48) * mm});
            skLineSegment(sketch, "E86.58.4.0", {"start": v(-21.75, -6.47) * mm, "end": v(-21.75, -9.25) * mm});
            skLineSegment(sketch, "E86.61.4.0", {"start": v(-14.25, -5.48) * mm, "end": v(-16.55, -6.81) * mm});
            skPoint(sketch, "E86.64.4.0", {"position": v(-17.85, -5.72) * mm});
            skLineSegment(sketch, "E86.65.4.0", {"start": v(-21.15, -6.81) * mm, "end": v(-21.15, -9.12) * mm});
            skPoint(sketch, "E86.68.4.0", {"position": v(-17.85, 5.72) * mm});
            skLineSegment(sketch, "E86.69.4.0", {"start": v(-14.85, -2.83) * mm, "end": v(-14.85, -5.14) * mm});
            skLineSegment(sketch, "E86.72.4.0", {"start": v(-14.85, 2.83) * mm, "end": v(-14.85, 5.14) * mm});
            skPoint(sketch, "E86.75.4.0", {"position": v(-18.15, 6.24) * mm});
            skLineSegment(sketch, "E86.76.4.0", {"start": v(-19.45, -5.14) * mm, "end": v(-21.75, -6.47) * mm});
            skPoint(sketch, "E86.79.4.0", {"position": v(-21.15, 0) * mm});
            skLineSegment(sketch, "E86.80.4.0", {"start": v(-16.55, 9.25) * mm, "end": v(-16.55, 6.81) * mm});
            skLineSegment(sketch, "E86.83.4.0", {"start": v(-16.55, -9.25) * mm, "end": v(-16.55, -6.81) * mm});
            skPoint(sketch, "E86.86.4.0", {"position": v(-21.75, 0) * mm});
            skPoint(sketch, "E86.87.4.0", {"position": v(-18.15, -6.24) * mm});
            skPoint(sketch, "E86.88.4.0", {"position": v(-19.15, -3) * mm});
            skLineSegment(sketch, "E86.89.4.0", {"start": v(-17.15, -9.12) * mm, "end": v(-17.15, -6.81) * mm});
            skLineSegment(sketch, "E86.92.4.0", {"start": v(-17.15, 9.12) * mm, "end": v(-17.15, 6.81) * mm});
            skPoint(sketch, "E86.95.4.0", {"position": v(-16.55, -1.5) * mm});
            skLineSegment(sketch, "E86.96.4.0", {"start": v(-21.75, 1.5) * mm, "end": v(-19.45, 2.83) * mm});
            skLineSegment(sketch, "E86.99.4.0", {"start": v(-18.85, 5.14) * mm, "end": v(-18.85, 2.83) * mm});
            skLineSegment(sketch, "E86.102.4.0", {"start": v(-16.85, 1.67) * mm, "end": v(-14.85, 2.83) * mm});
            skLineSegment(sketch, "E86.105.4.0", {"start": v(-19.15, -5.66) * mm, "end": v(-21.15, -6.81) * mm});
            skLineSegment(sketch, "E86.108.4.0", {"start": v(-19.45, 5.14) * mm, "end": v(-19.45, 2.83) * mm});
            skLineSegment(sketch, "E86.111.4.0", {"start": v(-18.85, -5.14) * mm, "end": v(-18.85, -2.83) * mm});
            skLineSegment(sketch, "E86.114.4.0", {"start": v(-16.55, -1.15) * mm, "end": v(-14.25, -2.48) * mm});
            skLineSegment(sketch, "E86.117.4.0", {"start": v(-16.55, -1.15) * mm, "end": v(-16.55, 1.15) * mm});
            skLineSegment(sketch, "E86.120.4.0", {"start": v(-16.55, -9.25) * mm, "end": v(-17.37, -9.25) * mm});
            skLineSegment(sketch, "E86.123.4.0", {"start": v(-16.85, -1.67) * mm, "end": v(-14.85, -2.83) * mm});
            skLineSegment(sketch, "E86.126.4.0", {"start": v(-14.85, -5.14) * mm, "end": v(-16.85, -6.3) * mm});
            skCircle(sketch, "E86.129.4.0", {"center": v(-19.15, 0) * mm, "radius": 2 * mm, "construction": true});
            skLineSegment(sketch, "E86.131.4.0", {"start": v(-21.15, -9.12) * mm, "end": v(-20.93, -9.25) * mm});
            skLineSegment(sketch, "E86.134.4.0", {"start": v(-14.85, 5.14) * mm, "end": v(-16.85, 6.3) * mm});
            skLineSegment(sketch, "E86.137.4.0", {"start": v(-19.45, -2.83) * mm, "end": v(-21.75, -1.5) * mm});
            skLineSegment(sketch, "E86.140.4.0", {"start": v(-21.75, 6.47) * mm, "end": v(-21.75, 9.25) * mm});
            skPoint(sketch, "E86.143.4.0", {"position": v(-21.15, 0) * mm});
            skLineSegment(sketch, "E86.144.4.0", {"start": v(-19.45, -5.14) * mm, "end": v(-19.45, -2.83) * mm});
            skLineSegment(sketch, "E86.147.4.0", {"start": v(-21.75, -6.81) * mm, "end": v(-21.75, -9.12) * mm});
            skLineSegment(sketch, "E86.150.4.0", {"start": v(-16.55, 1.15) * mm, "end": v(-14.25, 2.48) * mm});
            skLineSegment(sketch, "E86.153.4.0", {"start": v(-19.15, 5.66) * mm, "end": v(-21.15, 6.81) * mm});
            skLineSegment(sketch, "E86.156.4.0", {"start": v(-21.75, -1.5) * mm, "end": v(-21.75, 0) * mm});
            skLineSegment(sketch, "E86.159.4.0", {"start": v(-17.37, 9.25) * mm, "end": v(-17.15, 9.12) * mm});
            skLineSegment(sketch, "E86.162.4.0", {"start": v(-21.15, 9.12) * mm, "end": v(-20.93, 9.25) * mm});
            skLineSegment(sketch, "E86.165.4.0", {"start": v(-16.55, -1.15) * mm, "end": v(-16.55, 1.15) * mm});
            skLineSegment(sketch, "E86.168.4.0", {"start": v(-21.75, 1.5) * mm, "end": v(-19.45, 2.83) * mm});
            skLineSegment(sketch, "E86.171.4.0", {"start": v(-16.85, -6.3) * mm, "end": v(-18.85, -5.14) * mm});
            skLineSegment(sketch, "E86.174.4.0", {"start": v(-17.37, -9.25) * mm, "end": v(-17.15, -9.12) * mm});
            skLineSegment(sketch, "E86.177.4.0", {"start": v(-17.15, 6.81) * mm, "end": v(-19.15, 5.66) * mm});
            skLineSegment(sketch, "E86.180.4.0", {"start": v(-17.15, -6.81) * mm, "end": v(-19.15, -5.66) * mm});
            skLineSegment(sketch, "E86.183.4.0", {"start": v(-20.93, -9.25) * mm, "end": v(-21.75, -9.25) * mm});
            skLineSegment(sketch, "E86.186.4.0", {"start": v(-16.85, 6.3) * mm, "end": v(-18.85, 5.14) * mm});
            skCircle(sketch, "E86.189.4.0", {"center": v(-19.15, 0) * mm, "radius": 2 * mm, "construction": true});
            skLineSegment(sketch, "E86.191.4.0", {"start": v(-16.55, 9.25) * mm, "end": v(-17.37, 9.25) * mm});
            skLineSegment(sketch, "E86.194.4.0", {"start": v(-21.75, -1.5) * mm, "end": v(-19.45, -2.83) * mm});
            skLineSegment(sketch, "E86.197.4.0", {"start": v(-17.15, 1.15) * mm, "end": v(-17.15, -1.15) * mm});
            skLineSegment(sketch, "E86.200.4.0", {"start": v(-21.15, -1.15) * mm, "end": v(-21.15, 1.15) * mm});
            skLineSegment(sketch, "E86.203.4.0", {"start": v(-16.55, 1.15) * mm, "end": v(-16.55, -1.15) * mm});
            skLineSegment(sketch, "E86.206.4.0", {"start": v(-17.15, 6.81) * mm, "end": v(-19.15, 5.66) * mm});
            skLineSegment(sketch, "E86.209.4.0", {"start": v(-17.15, -6.81) * mm, "end": v(-19.15, -5.66) * mm});
            skLineSegment(sketch, "E86.212.4.0", {"start": v(-16.85, -6.3) * mm, "end": v(-18.85, -5.14) * mm});
            skLineSegment(sketch, "E86.215.4.0", {"start": v(-21.75, 1.5) * mm, "end": v(-21.75, -1.5) * mm});
            skLineSegment(sketch, "E86.218.4.0", {"start": v(-19.45, 2.83) * mm, "end": v(-21.75, 1.5) * mm});
            skLineSegment(sketch, "E86.221.4.0", {"start": v(-16.85, 6.3) * mm, "end": v(-18.85, 5.14) * mm});
            skLineSegment(sketch, "E86.224.4.0", {"start": v(-21.75, -1.5) * mm, "end": v(-19.45, -2.83) * mm});
            skLineSegment(sketch, "E86.227.4.0", {"start": v(-19.15, -2.3) * mm, "end": v(-21.15, -1.15) * mm});
            skLineSegment(sketch, "E86.230.4.0", {"start": v(-17.85, 2.25) * mm, "end": v(-16.85, 1.67) * mm});
            skLineSegment(sketch, "E86.233.4.0", {"start": v(-18.85, 2.83) * mm, "end": v(-16.85, 1.67) * mm});
            skLineSegment(sketch, "E86.236.4.0", {"start": v(-21.15, 1.15) * mm, "end": v(-21.15, -1.15) * mm});
            skLineSegment(sketch, "E86.239.4.0", {"start": v(-17.15, -1.15) * mm, "end": v(-17.15, 1.15) * mm});
            skLineSegment(sketch, "E86.242.4.0", {"start": v(-16.55, 1.15) * mm, "end": v(-16.55, -1.15) * mm});
            skLineSegment(sketch, "E86.245.4.0", {"start": v(-17.15, -1.15) * mm, "end": v(-19.15, -2.3) * mm});
            skLineSegment(sketch, "E86.248.4.0", {"start": v(-21.15, 1.15) * mm, "end": v(-19.15, 2.3) * mm});
            skLineSegment(sketch, "E86.251.4.0", {"start": v(-16.85, -1.67) * mm, "end": v(-18.85, -2.83) * mm});
            skLineSegment(sketch, "E86.254.4.0", {"start": v(-16.85, 1.67) * mm, "end": v(-18.85, 2.83) * mm});
            skLineSegment(sketch, "E86.257.4.0", {"start": v(-17.15, 1.15) * mm, "end": v(-17.15, -1.15) * mm});
            skLineSegment(sketch, "E86.260.4.0", {"start": v(-21.15, -1.15) * mm, "end": v(-19.15, -2.3) * mm});
            skLineSegment(sketch, "E86.263.4.0", {"start": v(-19.15, 2.3) * mm, "end": v(-17.15, 1.15) * mm});
            skLineSegment(sketch, "E86.266.4.0", {"start": v(-19.15, -2.3) * mm, "end": v(-17.15, -1.15) * mm});
            skLineSegment(sketch, "E86.269.4.0", {"start": v(-18.85, -2.83) * mm, "end": v(-16.85, -1.67) * mm});
            skLineSegment(sketch, "E86.272.4.0", {"start": v(-21.15, 1.15) * mm, "end": v(-19.15, 2.3) * mm});
            skLineSegment(sketch, "E86.275.4.0", {"start": v(-17.15, -1.15) * mm, "end": v(-17.15, 1.15) * mm});
            skLineSegment(sketch, "E86.278.4.0", {"start": v(-21.15, -1.15) * mm, "end": v(-19.15, -2.3) * mm});
            skLineSegment(sketch, "E86.281.4.0", {"start": v(-17.15, 1.15) * mm, "end": v(-19.15, 2.3) * mm});
            skLineSegment(sketch, "E86.284.4.0", {"start": v(-19.15, -2.3) * mm, "end": v(-17.15, -1.15) * mm});
            skLineSegment(sketch, "E86.287.4.0", {"start": v(-18.85, -2.83) * mm, "end": v(-16.85, -1.67) * mm});
            skLineSegment(sketch, "E86.290.4.0", {"start": v(-19.15, 2.3) * mm, "end": v(-21.15, 1.15) * mm});
            skLineSegment(sketch, "E86.293.4.0", {"start": v(-19.15, 2.3) * mm, "end": v(-17.15, 1.15) * mm});
            skPoint(sketch, "E86.0.5.0", {"position": v(-11.95, -1.5) * mm});
            skPoint(sketch, "E86.1.5.0", {"position": v(-13.25, -5.72) * mm});
            skCircle(sketch, "E86.2.5.0", {"center": v(-14.55, 0) * mm, "radius": 2 * mm, "construction": true});
            skPoint(sketch, "E86.4.5.0", {"position": v(-14.55, 3) * mm});
            skPoint(sketch, "E86.5.5.0", {"position": v(-13.55, -6.24) * mm});
            skPoint(sketch, "E86.6.5.0", {"position": v(-11.95, 1.5) * mm});
            skCircle(sketch, "E86.7.5.0", {"center": v(-14.55, 0) * mm, "radius": 2.6 * mm, "construction": true});
            skPoint(sketch, "E86.9.5.0", {"position": v(-13.55, 6.24) * mm});
            skPoint(sketch, "E86.10.5.0", {"position": v(-14.55, -3) * mm});
            skCircle(sketch, "E86.11.5.0", {"center": v(-14.55, -7.97) * mm, "radius": 2.6 * mm, "construction": true});
            skPoint(sketch, "E86.13.5.0", {"position": v(-13.25, 5.72) * mm});
            skCircle(sketch, "E86.14.5.0", {"center": v(-12.25, -3.98) * mm, "radius": 2.6 * mm, "construction": true});
            skCircle(sketch, "E86.16.5.0", {"center": v(-12.25, 3.98) * mm, "radius": 2.6 * mm, "construction": true});
            skCircle(sketch, "E86.18.5.0", {"center": v(-14.55, 7.97) * mm, "radius": 2 * mm, "construction": true});
            skCircle(sketch, "E86.20.5.0", {"center": v(-12.25, -3.98) * mm, "radius": 2 * mm, "construction": true});
            skLineSegment(sketch, "E86.22.5.0", {"start": v(-13.02, 9.25) * mm, "end": v(-17.15, 9.25) * mm});
            skPoint(sketch, "E86.25.5.0", {"position": v(-17.15, 0) * mm});
            skCircle(sketch, "E86.26.5.0", {"center": v(-14.55, 7.97) * mm, "radius": 2.6 * mm, "construction": true});
            skCircle(sketch, "E86.28.5.0", {"center": v(-12.25, 3.98) * mm, "radius": 2 * mm, "construction": true});
            skCircle(sketch, "E86.30.5.0", {"center": v(-14.55, -7.97) * mm, "radius": 2 * mm, "construction": true});
            skArc(sketch, "E86.32.5.0", {"start": v(-15.85, -2.25) * mm, "mid": v(-11.95, 0) * mm, "end": v(-15.85, 2.25) * mm, "construction": true});
            skPoint(sketch, "E86.36.5.0", {"position": v(-14.55, 3) * mm});
            skCircle(sketch, "E86.37.5.0", {"center": v(-14.55, 0) * mm, "radius": 2 * mm, "construction": true});
            skPoint(sketch, "E86.39.5.0", {"position": v(-11.95, 1.5) * mm});
            skLineSegment(sketch, "E86.40.5.0", {"start": v(-17.15, 6.81) * mm, "end": v(-17.15, 9.12) * mm});
            skLineSegment(sketch, "E86.43.5.0", {"start": v(-14.85, 5.14) * mm, "end": v(-17.15, 6.47) * mm});
            skLineSegment(sketch, "E86.46.5.0", {"start": v(-16.55, 6.81) * mm, "end": v(-16.55, 9.12) * mm});
            skLineSegment(sketch, "E86.49.5.0", {"start": v(-9.65, 5.48) * mm, "end": v(-11.95, 6.81) * mm});
            skLineSegment(sketch, "E86.52.5.0", {"start": v(-9.65, 2.48) * mm, "end": v(-9.65, 5.48) * mm});
            skLineSegment(sketch, "E86.55.5.0", {"start": v(-9.65, -2.48) * mm, "end": v(-9.65, -5.48) * mm});
            skLineSegment(sketch, "E86.58.5.0", {"start": v(-17.15, -6.47) * mm, "end": v(-17.15, -9.25) * mm});
            skLineSegment(sketch, "E86.61.5.0", {"start": v(-9.65, -5.48) * mm, "end": v(-11.95, -6.81) * mm});
            skPoint(sketch, "E86.64.5.0", {"position": v(-13.25, -5.72) * mm});
            skLineSegment(sketch, "E86.65.5.0", {"start": v(-16.55, -6.81) * mm, "end": v(-16.55, -9.12) * mm});
            skPoint(sketch, "E86.68.5.0", {"position": v(-13.25, 5.72) * mm});
            skLineSegment(sketch, "E86.69.5.0", {"start": v(-10.25, -2.83) * mm, "end": v(-10.25, -5.14) * mm});
            skLineSegment(sketch, "E86.72.5.0", {"start": v(-10.25, 2.83) * mm, "end": v(-10.25, 5.14) * mm});
            skPoint(sketch, "E86.75.5.0", {"position": v(-13.55, 6.24) * mm});
            skLineSegment(sketch, "E86.76.5.0", {"start": v(-14.85, -5.14) * mm, "end": v(-17.15, -6.47) * mm});
            skPoint(sketch, "E86.79.5.0", {"position": v(-16.55, 0) * mm});
            skLineSegment(sketch, "E86.80.5.0", {"start": v(-11.95, 9.25) * mm, "end": v(-11.95, 6.81) * mm});
            skLineSegment(sketch, "E86.83.5.0", {"start": v(-11.95, -9.25) * mm, "end": v(-11.95, -6.81) * mm});
            skPoint(sketch, "E86.86.5.0", {"position": v(-17.15, 0) * mm});
            skPoint(sketch, "E86.87.5.0", {"position": v(-13.55, -6.24) * mm});
            skPoint(sketch, "E86.88.5.0", {"position": v(-14.55, -3) * mm});
            skLineSegment(sketch, "E86.89.5.0", {"start": v(-12.55, -9.12) * mm, "end": v(-12.55, -6.81) * mm});
            skLineSegment(sketch, "E86.92.5.0", {"start": v(-12.55, 9.12) * mm, "end": v(-12.55, 6.81) * mm});
            skPoint(sketch, "E86.95.5.0", {"position": v(-11.95, -1.5) * mm});
            skLineSegment(sketch, "E86.96.5.0", {"start": v(-17.15, 1.5) * mm, "end": v(-14.85, 2.83) * mm});
            skLineSegment(sketch, "E86.99.5.0", {"start": v(-14.25, 5.14) * mm, "end": v(-14.25, 2.83) * mm});
            skLineSegment(sketch, "E86.102.5.0", {"start": v(-12.25, 1.67) * mm, "end": v(-10.25, 2.83) * mm});
            skLineSegment(sketch, "E86.105.5.0", {"start": v(-14.55, -5.66) * mm, "end": v(-16.55, -6.81) * mm});
            skLineSegment(sketch, "E86.108.5.0", {"start": v(-14.85, 5.14) * mm, "end": v(-14.85, 2.83) * mm});
            skLineSegment(sketch, "E86.111.5.0", {"start": v(-14.25, -5.14) * mm, "end": v(-14.25, -2.83) * mm});
            skLineSegment(sketch, "E86.114.5.0", {"start": v(-11.95, -1.15) * mm, "end": v(-9.65, -2.48) * mm});
            skLineSegment(sketch, "E86.117.5.0", {"start": v(-11.95, -1.15) * mm, "end": v(-11.95, 1.15) * mm});
            skLineSegment(sketch, "E86.120.5.0", {"start": v(-11.95, -9.25) * mm, "end": v(-12.77, -9.25) * mm});
            skLineSegment(sketch, "E86.123.5.0", {"start": v(-12.25, -1.67) * mm, "end": v(-10.25, -2.83) * mm});
            skLineSegment(sketch, "E86.126.5.0", {"start": v(-10.25, -5.14) * mm, "end": v(-12.25, -6.3) * mm});
            skCircle(sketch, "E86.129.5.0", {"center": v(-14.55, 0) * mm, "radius": 2 * mm, "construction": true});
            skLineSegment(sketch, "E86.131.5.0", {"start": v(-16.55, -9.12) * mm, "end": v(-16.33, -9.25) * mm});
            skLineSegment(sketch, "E86.134.5.0", {"start": v(-10.25, 5.14) * mm, "end": v(-12.25, 6.3) * mm});
            skLineSegment(sketch, "E86.137.5.0", {"start": v(-14.85, -2.83) * mm, "end": v(-17.15, -1.5) * mm});
            skLineSegment(sketch, "E86.140.5.0", {"start": v(-17.15, 6.47) * mm, "end": v(-17.15, 9.25) * mm});
            skPoint(sketch, "E86.143.5.0", {"position": v(-16.55, 0) * mm});
            skLineSegment(sketch, "E86.144.5.0", {"start": v(-14.85, -5.14) * mm, "end": v(-14.85, -2.83) * mm});
            skLineSegment(sketch, "E86.147.5.0", {"start": v(-17.15, -6.81) * mm, "end": v(-17.15, -9.12) * mm});
            skLineSegment(sketch, "E86.150.5.0", {"start": v(-11.95, 1.15) * mm, "end": v(-9.65, 2.48) * mm});
            skLineSegment(sketch, "E86.153.5.0", {"start": v(-14.55, 5.66) * mm, "end": v(-16.55, 6.81) * mm});
            skLineSegment(sketch, "E86.156.5.0", {"start": v(-17.15, -1.5) * mm, "end": v(-17.15, 0) * mm});
            skLineSegment(sketch, "E86.159.5.0", {"start": v(-12.77, 9.25) * mm, "end": v(-12.55, 9.12) * mm});
            skLineSegment(sketch, "E86.162.5.0", {"start": v(-16.55, 9.12) * mm, "end": v(-16.33, 9.25) * mm});
            skLineSegment(sketch, "E86.165.5.0", {"start": v(-11.95, -1.15) * mm, "end": v(-11.95, 1.15) * mm});
            skLineSegment(sketch, "E86.168.5.0", {"start": v(-17.15, 1.5) * mm, "end": v(-14.85, 2.83) * mm});
            skLineSegment(sketch, "E86.171.5.0", {"start": v(-12.25, -6.3) * mm, "end": v(-14.25, -5.14) * mm});
            skLineSegment(sketch, "E86.174.5.0", {"start": v(-12.77, -9.25) * mm, "end": v(-12.55, -9.12) * mm});
            skLineSegment(sketch, "E86.177.5.0", {"start": v(-12.55, 6.81) * mm, "end": v(-14.55, 5.66) * mm});
            skLineSegment(sketch, "E86.180.5.0", {"start": v(-12.55, -6.81) * mm, "end": v(-14.55, -5.66) * mm});
            skLineSegment(sketch, "E86.183.5.0", {"start": v(-16.33, -9.25) * mm, "end": v(-17.15, -9.25) * mm});
            skLineSegment(sketch, "E86.186.5.0", {"start": v(-12.25, 6.3) * mm, "end": v(-14.25, 5.14) * mm});
            skCircle(sketch, "E86.189.5.0", {"center": v(-14.55, 0) * mm, "radius": 2 * mm, "construction": true});
            skLineSegment(sketch, "E86.191.5.0", {"start": v(-11.95, 9.25) * mm, "end": v(-12.77, 9.25) * mm});
            skLineSegment(sketch, "E86.194.5.0", {"start": v(-17.15, -1.5) * mm, "end": v(-14.85, -2.83) * mm});
            skLineSegment(sketch, "E86.197.5.0", {"start": v(-12.55, 1.15) * mm, "end": v(-12.55, -1.15) * mm});
            skLineSegment(sketch, "E86.200.5.0", {"start": v(-16.55, -1.15) * mm, "end": v(-16.55, 1.15) * mm});
            skLineSegment(sketch, "E86.203.5.0", {"start": v(-11.95, 1.15) * mm, "end": v(-11.95, -1.15) * mm});
            skLineSegment(sketch, "E86.206.5.0", {"start": v(-12.55, 6.81) * mm, "end": v(-14.55, 5.66) * mm});
            skLineSegment(sketch, "E86.209.5.0", {"start": v(-12.55, -6.81) * mm, "end": v(-14.55, -5.66) * mm});
            skLineSegment(sketch, "E86.212.5.0", {"start": v(-12.25, -6.3) * mm, "end": v(-14.25, -5.14) * mm});
            skLineSegment(sketch, "E86.215.5.0", {"start": v(-17.15, 1.5) * mm, "end": v(-17.15, -1.5) * mm});
            skLineSegment(sketch, "E86.218.5.0", {"start": v(-14.85, 2.83) * mm, "end": v(-17.15, 1.5) * mm});
            skLineSegment(sketch, "E86.221.5.0", {"start": v(-12.25, 6.3) * mm, "end": v(-14.25, 5.14) * mm});
            skLineSegment(sketch, "E86.224.5.0", {"start": v(-17.15, -1.5) * mm, "end": v(-14.85, -2.83) * mm});
            skLineSegment(sketch, "E86.227.5.0", {"start": v(-14.55, -2.3) * mm, "end": v(-16.55, -1.15) * mm});
            skLineSegment(sketch, "E86.230.5.0", {"start": v(-13.25, 2.25) * mm, "end": v(-12.25, 1.67) * mm});
            skLineSegment(sketch, "E86.233.5.0", {"start": v(-14.25, 2.83) * mm, "end": v(-12.25, 1.67) * mm});
            skLineSegment(sketch, "E86.236.5.0", {"start": v(-16.55, 1.15) * mm, "end": v(-16.55, -1.15) * mm});
            skLineSegment(sketch, "E86.239.5.0", {"start": v(-12.55, -1.15) * mm, "end": v(-12.55, 1.15) * mm});
            skLineSegment(sketch, "E86.242.5.0", {"start": v(-11.95, 1.15) * mm, "end": v(-11.95, -1.15) * mm});
            skLineSegment(sketch, "E86.245.5.0", {"start": v(-12.55, -1.15) * mm, "end": v(-14.55, -2.3) * mm});
            skLineSegment(sketch, "E86.248.5.0", {"start": v(-16.55, 1.15) * mm, "end": v(-14.55, 2.3) * mm});
            skLineSegment(sketch, "E86.251.5.0", {"start": v(-12.25, -1.67) * mm, "end": v(-14.25, -2.83) * mm});
            skLineSegment(sketch, "E86.254.5.0", {"start": v(-12.25, 1.67) * mm, "end": v(-14.25, 2.83) * mm});
            skLineSegment(sketch, "E86.257.5.0", {"start": v(-12.55, 1.15) * mm, "end": v(-12.55, -1.15) * mm});
            skLineSegment(sketch, "E86.260.5.0", {"start": v(-16.55, -1.15) * mm, "end": v(-14.55, -2.3) * mm});
            skLineSegment(sketch, "E86.263.5.0", {"start": v(-14.55, 2.3) * mm, "end": v(-12.55, 1.15) * mm});
            skLineSegment(sketch, "E86.266.5.0", {"start": v(-14.55, -2.3) * mm, "end": v(-12.55, -1.15) * mm});
            skLineSegment(sketch, "E86.269.5.0", {"start": v(-14.25, -2.83) * mm, "end": v(-12.25, -1.67) * mm});
            skLineSegment(sketch, "E86.272.5.0", {"start": v(-16.55, 1.15) * mm, "end": v(-14.55, 2.3) * mm});
            skLineSegment(sketch, "E86.275.5.0", {"start": v(-12.55, -1.15) * mm, "end": v(-12.55, 1.15) * mm});
            skLineSegment(sketch, "E86.278.5.0", {"start": v(-16.55, -1.15) * mm, "end": v(-14.55, -2.3) * mm});
            skLineSegment(sketch, "E86.281.5.0", {"start": v(-12.55, 1.15) * mm, "end": v(-14.55, 2.3) * mm});
            skLineSegment(sketch, "E86.284.5.0", {"start": v(-14.55, -2.3) * mm, "end": v(-12.55, -1.15) * mm});
            skLineSegment(sketch, "E86.287.5.0", {"start": v(-14.25, -2.83) * mm, "end": v(-12.25, -1.67) * mm});
            skLineSegment(sketch, "E86.290.5.0", {"start": v(-14.55, 2.3) * mm, "end": v(-16.55, 1.15) * mm});
            skLineSegment(sketch, "E86.293.5.0", {"start": v(-14.55, 2.3) * mm, "end": v(-12.55, 1.15) * mm});
            skPoint(sketch, "E86.0.6.0", {"position": v(-7.35, -1.5) * mm});
            skPoint(sketch, "E86.1.6.0", {"position": v(-8.65, -5.72) * mm});
            skCircle(sketch, "E86.2.6.0", {"center": v(-9.95, 0) * mm, "radius": 2 * mm, "construction": true});
            skPoint(sketch, "E86.4.6.0", {"position": v(-9.95, 3) * mm});
            skPoint(sketch, "E86.5.6.0", {"position": v(-8.95, -6.24) * mm});
            skPoint(sketch, "E86.6.6.0", {"position": v(-7.35, 1.5) * mm});
            skCircle(sketch, "E86.7.6.0", {"center": v(-9.95, 0) * mm, "radius": 2.6 * mm, "construction": true});
            skPoint(sketch, "E86.9.6.0", {"position": v(-8.95, 6.24) * mm});
            skPoint(sketch, "E86.10.6.0", {"position": v(-9.95, -3) * mm});
            skCircle(sketch, "E86.11.6.0", {"center": v(-9.95, -7.97) * mm, "radius": 2.6 * mm, "construction": true});
            skPoint(sketch, "E86.13.6.0", {"position": v(-8.65, 5.72) * mm});
            skCircle(sketch, "E86.14.6.0", {"center": v(-7.65, -3.98) * mm, "radius": 2.6 * mm, "construction": true});
            skCircle(sketch, "E86.16.6.0", {"center": v(-7.65, 3.98) * mm, "radius": 2.6 * mm, "construction": true});
            skCircle(sketch, "E86.18.6.0", {"center": v(-9.95, 7.97) * mm, "radius": 2 * mm, "construction": true});
            skCircle(sketch, "E86.20.6.0", {"center": v(-7.65, -3.98) * mm, "radius": 2 * mm, "construction": true});
            skLineSegment(sketch, "E86.22.6.0", {"start": v(-8.42, 9.25) * mm, "end": v(-12.55, 9.25) * mm});
            skPoint(sketch, "E86.25.6.0", {"position": v(-12.55, 0) * mm});
            skCircle(sketch, "E86.26.6.0", {"center": v(-9.95, 7.97) * mm, "radius": 2.6 * mm, "construction": true});
            skCircle(sketch, "E86.28.6.0", {"center": v(-7.65, 3.98) * mm, "radius": 2 * mm, "construction": true});
            skCircle(sketch, "E86.30.6.0", {"center": v(-9.95, -7.97) * mm, "radius": 2 * mm, "construction": true});
            skArc(sketch, "E86.32.6.0", {"start": v(-11.25, -2.25) * mm, "mid": v(-7.35, 0) * mm, "end": v(-11.25, 2.25) * mm, "construction": true});
            skPoint(sketch, "E86.36.6.0", {"position": v(-9.95, 3) * mm});
            skCircle(sketch, "E86.37.6.0", {"center": v(-9.95, 0) * mm, "radius": 2 * mm, "construction": true});
            skPoint(sketch, "E86.39.6.0", {"position": v(-7.35, 1.5) * mm});
            skLineSegment(sketch, "E86.40.6.0", {"start": v(-12.55, 6.81) * mm, "end": v(-12.55, 9.12) * mm});
            skLineSegment(sketch, "E86.43.6.0", {"start": v(-10.25, 5.14) * mm, "end": v(-12.55, 6.47) * mm});
            skLineSegment(sketch, "E86.46.6.0", {"start": v(-11.95, 6.81) * mm, "end": v(-11.95, 9.12) * mm});
            skLineSegment(sketch, "E86.49.6.0", {"start": v(-5.05, 5.48) * mm, "end": v(-7.35, 6.81) * mm});
            skLineSegment(sketch, "E86.52.6.0", {"start": v(-5.05, 2.48) * mm, "end": v(-5.05, 5.48) * mm});
            skLineSegment(sketch, "E86.55.6.0", {"start": v(-5.05, -2.48) * mm, "end": v(-5.05, -5.48) * mm});
            skLineSegment(sketch, "E86.58.6.0", {"start": v(-12.55, -6.47) * mm, "end": v(-12.55, -9.25) * mm});
            skLineSegment(sketch, "E86.61.6.0", {"start": v(-5.05, -5.48) * mm, "end": v(-7.35, -6.81) * mm});
            skPoint(sketch, "E86.64.6.0", {"position": v(-8.65, -5.72) * mm});
            skLineSegment(sketch, "E86.65.6.0", {"start": v(-11.95, -6.81) * mm, "end": v(-11.95, -9.12) * mm});
            skPoint(sketch, "E86.68.6.0", {"position": v(-8.65, 5.72) * mm});
            skLineSegment(sketch, "E86.69.6.0", {"start": v(-5.65, -2.83) * mm, "end": v(-5.65, -5.14) * mm});
            skLineSegment(sketch, "E86.72.6.0", {"start": v(-5.65, 2.83) * mm, "end": v(-5.65, 5.14) * mm});
            skPoint(sketch, "E86.75.6.0", {"position": v(-8.95, 6.24) * mm});
            skLineSegment(sketch, "E86.76.6.0", {"start": v(-10.25, -5.14) * mm, "end": v(-12.55, -6.47) * mm});
            skPoint(sketch, "E86.79.6.0", {"position": v(-11.95, 0) * mm});
            skLineSegment(sketch, "E86.80.6.0", {"start": v(-7.35, 9.25) * mm, "end": v(-7.35, 6.81) * mm});
            skLineSegment(sketch, "E86.83.6.0", {"start": v(-7.35, -9.25) * mm, "end": v(-7.35, -6.81) * mm});
            skPoint(sketch, "E86.86.6.0", {"position": v(-12.55, 0) * mm});
            skPoint(sketch, "E86.87.6.0", {"position": v(-8.95, -6.24) * mm});
            skPoint(sketch, "E86.88.6.0", {"position": v(-9.95, -3) * mm});
            skLineSegment(sketch, "E86.89.6.0", {"start": v(-7.95, -9.12) * mm, "end": v(-7.95, -6.81) * mm});
            skLineSegment(sketch, "E86.92.6.0", {"start": v(-7.95, 9.12) * mm, "end": v(-7.95, 6.81) * mm});
            skPoint(sketch, "E86.95.6.0", {"position": v(-7.35, -1.5) * mm});
            skLineSegment(sketch, "E86.96.6.0", {"start": v(-12.55, 1.5) * mm, "end": v(-10.25, 2.83) * mm});
            skLineSegment(sketch, "E86.99.6.0", {"start": v(-9.65, 5.14) * mm, "end": v(-9.65, 2.83) * mm});
            skLineSegment(sketch, "E86.102.6.0", {"start": v(-7.65, 1.67) * mm, "end": v(-5.65, 2.83) * mm});
            skLineSegment(sketch, "E86.105.6.0", {"start": v(-9.95, -5.66) * mm, "end": v(-11.95, -6.81) * mm});
            skLineSegment(sketch, "E86.108.6.0", {"start": v(-10.25, 5.14) * mm, "end": v(-10.25, 2.83) * mm});
            skLineSegment(sketch, "E86.111.6.0", {"start": v(-9.65, -5.14) * mm, "end": v(-9.65, -2.83) * mm});
            skLineSegment(sketch, "E86.114.6.0", {"start": v(-7.35, -1.15) * mm, "end": v(-5.05, -2.48) * mm});
            skLineSegment(sketch, "E86.117.6.0", {"start": v(-7.35, -1.15) * mm, "end": v(-7.35, 1.15) * mm});
            skLineSegment(sketch, "E86.120.6.0", {"start": v(-7.35, -9.25) * mm, "end": v(-8.17, -9.25) * mm});
            skLineSegment(sketch, "E86.123.6.0", {"start": v(-7.65, -1.67) * mm, "end": v(-5.65, -2.83) * mm});
            skLineSegment(sketch, "E86.126.6.0", {"start": v(-5.65, -5.14) * mm, "end": v(-7.65, -6.3) * mm});
            skCircle(sketch, "E86.129.6.0", {"center": v(-9.95, 0) * mm, "radius": 2 * mm, "construction": true});
            skLineSegment(sketch, "E86.131.6.0", {"start": v(-11.95, -9.12) * mm, "end": v(-11.73, -9.25) * mm});
            skLineSegment(sketch, "E86.134.6.0", {"start": v(-5.65, 5.14) * mm, "end": v(-7.65, 6.3) * mm});
            skLineSegment(sketch, "E86.137.6.0", {"start": v(-10.25, -2.83) * mm, "end": v(-12.55, -1.5) * mm});
            skLineSegment(sketch, "E86.140.6.0", {"start": v(-12.55, 6.47) * mm, "end": v(-12.55, 9.25) * mm});
            skPoint(sketch, "E86.143.6.0", {"position": v(-11.95, 0) * mm});
            skLineSegment(sketch, "E86.144.6.0", {"start": v(-10.25, -5.14) * mm, "end": v(-10.25, -2.83) * mm});
            skLineSegment(sketch, "E86.147.6.0", {"start": v(-12.55, -6.81) * mm, "end": v(-12.55, -9.12) * mm});
            skLineSegment(sketch, "E86.150.6.0", {"start": v(-7.35, 1.15) * mm, "end": v(-5.05, 2.48) * mm});
            skLineSegment(sketch, "E86.153.6.0", {"start": v(-9.95, 5.66) * mm, "end": v(-11.95, 6.81) * mm});
            skLineSegment(sketch, "E86.156.6.0", {"start": v(-12.55, -1.5) * mm, "end": v(-12.55, 0) * mm});
            skLineSegment(sketch, "E86.159.6.0", {"start": v(-8.17, 9.25) * mm, "end": v(-7.95, 9.12) * mm});
            skLineSegment(sketch, "E86.162.6.0", {"start": v(-11.95, 9.12) * mm, "end": v(-11.73, 9.25) * mm});
            skLineSegment(sketch, "E86.165.6.0", {"start": v(-7.35, -1.15) * mm, "end": v(-7.35, 1.15) * mm});
            skLineSegment(sketch, "E86.168.6.0", {"start": v(-12.55, 1.5) * mm, "end": v(-10.25, 2.83) * mm});
            skLineSegment(sketch, "E86.171.6.0", {"start": v(-7.65, -6.3) * mm, "end": v(-9.65, -5.14) * mm});
            skLineSegment(sketch, "E86.174.6.0", {"start": v(-8.17, -9.25) * mm, "end": v(-7.95, -9.12) * mm});
            skLineSegment(sketch, "E86.177.6.0", {"start": v(-7.95, 6.81) * mm, "end": v(-9.95, 5.66) * mm});
            skLineSegment(sketch, "E86.180.6.0", {"start": v(-7.95, -6.81) * mm, "end": v(-9.95, -5.66) * mm});
            skLineSegment(sketch, "E86.183.6.0", {"start": v(-11.73, -9.25) * mm, "end": v(-12.55, -9.25) * mm});
            skLineSegment(sketch, "E86.186.6.0", {"start": v(-7.65, 6.3) * mm, "end": v(-9.65, 5.14) * mm});
            skCircle(sketch, "E86.189.6.0", {"center": v(-9.95, 0) * mm, "radius": 2 * mm, "construction": true});
            skLineSegment(sketch, "E86.191.6.0", {"start": v(-7.35, 9.25) * mm, "end": v(-8.17, 9.25) * mm});
            skLineSegment(sketch, "E86.194.6.0", {"start": v(-12.55, -1.5) * mm, "end": v(-10.25, -2.83) * mm});
            skLineSegment(sketch, "E86.197.6.0", {"start": v(-7.95, 1.15) * mm, "end": v(-7.95, -1.15) * mm});
            skLineSegment(sketch, "E86.200.6.0", {"start": v(-11.95, -1.15) * mm, "end": v(-11.95, 1.15) * mm});
            skLineSegment(sketch, "E86.203.6.0", {"start": v(-7.35, 1.15) * mm, "end": v(-7.35, -1.15) * mm});
            skLineSegment(sketch, "E86.206.6.0", {"start": v(-7.95, 6.81) * mm, "end": v(-9.95, 5.66) * mm});
            skLineSegment(sketch, "E86.209.6.0", {"start": v(-7.95, -6.81) * mm, "end": v(-9.95, -5.66) * mm});
            skLineSegment(sketch, "E86.212.6.0", {"start": v(-7.65, -6.3) * mm, "end": v(-9.65, -5.14) * mm});
            skLineSegment(sketch, "E86.215.6.0", {"start": v(-12.55, 1.5) * mm, "end": v(-12.55, -1.5) * mm});
            skLineSegment(sketch, "E86.218.6.0", {"start": v(-10.25, 2.83) * mm, "end": v(-12.55, 1.5) * mm});
            skLineSegment(sketch, "E86.221.6.0", {"start": v(-7.65, 6.3) * mm, "end": v(-9.65, 5.14) * mm});
            skLineSegment(sketch, "E86.224.6.0", {"start": v(-12.55, -1.5) * mm, "end": v(-10.25, -2.83) * mm});
            skLineSegment(sketch, "E86.227.6.0", {"start": v(-9.95, -2.3) * mm, "end": v(-11.95, -1.15) * mm});
            skLineSegment(sketch, "E86.230.6.0", {"start": v(-8.65, 2.25) * mm, "end": v(-7.65, 1.67) * mm});
            skLineSegment(sketch, "E86.233.6.0", {"start": v(-9.65, 2.83) * mm, "end": v(-7.65, 1.67) * mm});
            skLineSegment(sketch, "E86.236.6.0", {"start": v(-11.95, 1.15) * mm, "end": v(-11.95, -1.15) * mm});
            skLineSegment(sketch, "E86.239.6.0", {"start": v(-7.95, -1.15) * mm, "end": v(-7.95, 1.15) * mm});
            skLineSegment(sketch, "E86.242.6.0", {"start": v(-7.35, 1.15) * mm, "end": v(-7.35, -1.15) * mm});
            skLineSegment(sketch, "E86.245.6.0", {"start": v(-7.95, -1.15) * mm, "end": v(-9.95, -2.3) * mm});
            skLineSegment(sketch, "E86.248.6.0", {"start": v(-11.95, 1.15) * mm, "end": v(-9.95, 2.3) * mm});
            skLineSegment(sketch, "E86.251.6.0", {"start": v(-7.65, -1.67) * mm, "end": v(-9.65, -2.83) * mm});
            skLineSegment(sketch, "E86.254.6.0", {"start": v(-7.65, 1.67) * mm, "end": v(-9.65, 2.83) * mm});
            skLineSegment(sketch, "E86.257.6.0", {"start": v(-7.95, 1.15) * mm, "end": v(-7.95, -1.15) * mm});
            skLineSegment(sketch, "E86.260.6.0", {"start": v(-11.95, -1.15) * mm, "end": v(-9.95, -2.3) * mm});
            skLineSegment(sketch, "E86.263.6.0", {"start": v(-9.95, 2.3) * mm, "end": v(-7.95, 1.15) * mm});
            skLineSegment(sketch, "E86.266.6.0", {"start": v(-9.95, -2.3) * mm, "end": v(-7.95, -1.15) * mm});
            skLineSegment(sketch, "E86.269.6.0", {"start": v(-9.65, -2.83) * mm, "end": v(-7.65, -1.67) * mm});
            skLineSegment(sketch, "E86.272.6.0", {"start": v(-11.95, 1.15) * mm, "end": v(-9.95, 2.3) * mm});
            skLineSegment(sketch, "E86.275.6.0", {"start": v(-7.95, -1.15) * mm, "end": v(-7.95, 1.15) * mm});
            skLineSegment(sketch, "E86.278.6.0", {"start": v(-11.95, -1.15) * mm, "end": v(-9.95, -2.3) * mm});
            skLineSegment(sketch, "E86.281.6.0", {"start": v(-7.95, 1.15) * mm, "end": v(-9.95, 2.3) * mm});
            skLineSegment(sketch, "E86.284.6.0", {"start": v(-9.95, -2.3) * mm, "end": v(-7.95, -1.15) * mm});
            skLineSegment(sketch, "E86.287.6.0", {"start": v(-9.65, -2.83) * mm, "end": v(-7.65, -1.67) * mm});
            skLineSegment(sketch, "E86.290.6.0", {"start": v(-9.95, 2.3) * mm, "end": v(-11.95, 1.15) * mm});
            skLineSegment(sketch, "E86.293.6.0", {"start": v(-9.95, 2.3) * mm, "end": v(-7.95, 1.15) * mm});
            skPoint(sketch, "E86.0.7.0", {"position": v(-2.75, -1.5) * mm});
            skPoint(sketch, "E86.1.7.0", {"position": v(-4.05, -5.72) * mm});
            skCircle(sketch, "E86.2.7.0", {"center": v(-5.35, 0) * mm, "radius": 2 * mm, "construction": true});
            skPoint(sketch, "E86.4.7.0", {"position": v(-5.35, 3) * mm});
            skPoint(sketch, "E86.5.7.0", {"position": v(-4.35, -6.24) * mm});
            skPoint(sketch, "E86.6.7.0", {"position": v(-2.75, 1.5) * mm});
            skCircle(sketch, "E86.7.7.0", {"center": v(-5.35, 0) * mm, "radius": 2.6 * mm, "construction": true});
            skPoint(sketch, "E86.9.7.0", {"position": v(-4.35, 6.24) * mm});
            skPoint(sketch, "E86.10.7.0", {"position": v(-5.35, -3) * mm});
            skCircle(sketch, "E86.11.7.0", {"center": v(-5.35, -7.97) * mm, "radius": 2.6 * mm, "construction": true});
            skPoint(sketch, "E86.13.7.0", {"position": v(-4.05, 5.72) * mm});
            skCircle(sketch, "E86.14.7.0", {"center": v(-3.05, -3.98) * mm, "radius": 2.6 * mm, "construction": true});
            skCircle(sketch, "E86.16.7.0", {"center": v(-3.05, 3.98) * mm, "radius": 2.6 * mm, "construction": true});
            skCircle(sketch, "E86.18.7.0", {"center": v(-5.35, 7.97) * mm, "radius": 2 * mm, "construction": true});
            skCircle(sketch, "E86.20.7.0", {"center": v(-3.05, -3.98) * mm, "radius": 2 * mm, "construction": true});
            skLineSegment(sketch, "E86.22.7.0", {"start": v(-3.82, 9.25) * mm, "end": v(-7.95, 9.25) * mm});
            skPoint(sketch, "E86.25.7.0", {"position": v(-7.95, 0) * mm});
            skCircle(sketch, "E86.26.7.0", {"center": v(-5.35, 7.97) * mm, "radius": 2.6 * mm, "construction": true});
            skCircle(sketch, "E86.28.7.0", {"center": v(-3.05, 3.98) * mm, "radius": 2 * mm, "construction": true});
            skCircle(sketch, "E86.30.7.0", {"center": v(-5.35, -7.97) * mm, "radius": 2 * mm, "construction": true});
            skArc(sketch, "E86.32.7.0", {"start": v(-6.65, -2.25) * mm, "mid": v(-2.75, 0) * mm, "end": v(-6.65, 2.25) * mm, "construction": true});
            skPoint(sketch, "E86.36.7.0", {"position": v(-5.35, 3) * mm});
            skCircle(sketch, "E86.37.7.0", {"center": v(-5.35, 0) * mm, "radius": 2 * mm, "construction": true});
            skPoint(sketch, "E86.39.7.0", {"position": v(-2.75, 1.5) * mm});
            skLineSegment(sketch, "E86.40.7.0", {"start": v(-7.95, 6.81) * mm, "end": v(-7.95, 9.12) * mm});
            skLineSegment(sketch, "E86.43.7.0", {"start": v(-5.65, 5.14) * mm, "end": v(-7.95, 6.47) * mm});
            skLineSegment(sketch, "E86.46.7.0", {"start": v(-7.35, 6.81) * mm, "end": v(-7.35, 9.12) * mm});
            skLineSegment(sketch, "E86.49.7.0", {"start": v(-0.45, 5.48) * mm, "end": v(-2.75, 6.81) * mm});
            skLineSegment(sketch, "E86.52.7.0", {"start": v(-0.45, 2.48) * mm, "end": v(-0.45, 5.48) * mm});
            skLineSegment(sketch, "E86.55.7.0", {"start": v(-0.45, -2.48) * mm, "end": v(-0.45, -5.48) * mm});
            skLineSegment(sketch, "E86.58.7.0", {"start": v(-7.95, -6.47) * mm, "end": v(-7.95, -9.25) * mm});
            skLineSegment(sketch, "E86.61.7.0", {"start": v(-0.45, -5.48) * mm, "end": v(-2.75, -6.81) * mm});
            skPoint(sketch, "E86.64.7.0", {"position": v(-4.05, -5.72) * mm});
            skLineSegment(sketch, "E86.65.7.0", {"start": v(-7.35, -6.81) * mm, "end": v(-7.35, -9.12) * mm});
            skPoint(sketch, "E86.68.7.0", {"position": v(-4.05, 5.72) * mm});
            skLineSegment(sketch, "E86.69.7.0", {"start": v(-1.05, -2.83) * mm, "end": v(-1.05, -5.14) * mm});
            skLineSegment(sketch, "E86.72.7.0", {"start": v(-1.05, 2.83) * mm, "end": v(-1.05, 5.14) * mm});
            skPoint(sketch, "E86.75.7.0", {"position": v(-4.35, 6.24) * mm});
            skLineSegment(sketch, "E86.76.7.0", {"start": v(-5.65, -5.14) * mm, "end": v(-7.95, -6.47) * mm});
            skPoint(sketch, "E86.79.7.0", {"position": v(-7.35, 0) * mm});
            skLineSegment(sketch, "E86.80.7.0", {"start": v(-2.75, 9.25) * mm, "end": v(-2.75, 6.81) * mm});
            skLineSegment(sketch, "E86.83.7.0", {"start": v(-2.75, -9.25) * mm, "end": v(-2.75, -6.81) * mm});
            skPoint(sketch, "E86.86.7.0", {"position": v(-7.95, 0) * mm});
            skPoint(sketch, "E86.87.7.0", {"position": v(-4.35, -6.24) * mm});
            skPoint(sketch, "E86.88.7.0", {"position": v(-5.35, -3) * mm});
            skLineSegment(sketch, "E86.89.7.0", {"start": v(-3.35, -9.12) * mm, "end": v(-3.35, -6.81) * mm});
            skLineSegment(sketch, "E86.92.7.0", {"start": v(-3.35, 9.12) * mm, "end": v(-3.35, 6.81) * mm});
            skPoint(sketch, "E86.95.7.0", {"position": v(-2.75, -1.5) * mm});
            skLineSegment(sketch, "E86.96.7.0", {"start": v(-7.95, 1.5) * mm, "end": v(-5.65, 2.83) * mm});
            skLineSegment(sketch, "E86.99.7.0", {"start": v(-5.05, 5.14) * mm, "end": v(-5.05, 2.83) * mm});
            skLineSegment(sketch, "E86.102.7.0", {"start": v(-3.05, 1.67) * mm, "end": v(-1.05, 2.83) * mm});
            skLineSegment(sketch, "E86.105.7.0", {"start": v(-5.35, -5.66) * mm, "end": v(-7.35, -6.81) * mm});
            skLineSegment(sketch, "E86.108.7.0", {"start": v(-5.65, 5.14) * mm, "end": v(-5.65, 2.83) * mm});
            skLineSegment(sketch, "E86.111.7.0", {"start": v(-5.05, -5.14) * mm, "end": v(-5.05, -2.83) * mm});
            skLineSegment(sketch, "E86.114.7.0", {"start": v(-2.75, -1.15) * mm, "end": v(-0.45, -2.48) * mm});
            skLineSegment(sketch, "E86.117.7.0", {"start": v(-2.75, -1.15) * mm, "end": v(-2.75, 1.15) * mm});
            skLineSegment(sketch, "E86.120.7.0", {"start": v(-2.75, -9.25) * mm, "end": v(-3.57, -9.25) * mm});
            skLineSegment(sketch, "E86.123.7.0", {"start": v(-3.05, -1.67) * mm, "end": v(-1.05, -2.83) * mm});
            skLineSegment(sketch, "E86.126.7.0", {"start": v(-1.05, -5.14) * mm, "end": v(-3.05, -6.3) * mm});
            skCircle(sketch, "E86.129.7.0", {"center": v(-5.35, 0) * mm, "radius": 2 * mm, "construction": true});
            skLineSegment(sketch, "E86.131.7.0", {"start": v(-7.35, -9.12) * mm, "end": v(-7.13, -9.25) * mm});
            skLineSegment(sketch, "E86.134.7.0", {"start": v(-1.05, 5.14) * mm, "end": v(-3.05, 6.3) * mm});
            skLineSegment(sketch, "E86.137.7.0", {"start": v(-5.65, -2.83) * mm, "end": v(-7.95, -1.5) * mm});
            skLineSegment(sketch, "E86.140.7.0", {"start": v(-7.95, 6.47) * mm, "end": v(-7.95, 9.25) * mm});
            skPoint(sketch, "E86.143.7.0", {"position": v(-7.35, 0) * mm});
            skLineSegment(sketch, "E86.144.7.0", {"start": v(-5.65, -5.14) * mm, "end": v(-5.65, -2.83) * mm});
            skLineSegment(sketch, "E86.147.7.0", {"start": v(-7.95, -6.81) * mm, "end": v(-7.95, -9.12) * mm});
            skLineSegment(sketch, "E86.150.7.0", {"start": v(-2.75, 1.15) * mm, "end": v(-0.45, 2.48) * mm});
            skLineSegment(sketch, "E86.153.7.0", {"start": v(-5.35, 5.66) * mm, "end": v(-7.35, 6.81) * mm});
            skLineSegment(sketch, "E86.156.7.0", {"start": v(-7.95, -1.5) * mm, "end": v(-7.95, 0) * mm});
            skLineSegment(sketch, "E86.159.7.0", {"start": v(-3.57, 9.25) * mm, "end": v(-3.35, 9.12) * mm});
            skLineSegment(sketch, "E86.162.7.0", {"start": v(-7.35, 9.12) * mm, "end": v(-7.13, 9.25) * mm});
            skLineSegment(sketch, "E86.165.7.0", {"start": v(-2.75, -1.15) * mm, "end": v(-2.75, 1.15) * mm});
            skLineSegment(sketch, "E86.168.7.0", {"start": v(-7.95, 1.5) * mm, "end": v(-5.65, 2.83) * mm});
            skLineSegment(sketch, "E86.171.7.0", {"start": v(-3.05, -6.3) * mm, "end": v(-5.05, -5.14) * mm});
            skLineSegment(sketch, "E86.174.7.0", {"start": v(-3.57, -9.25) * mm, "end": v(-3.35, -9.12) * mm});
            skLineSegment(sketch, "E86.177.7.0", {"start": v(-3.35, 6.81) * mm, "end": v(-5.35, 5.66) * mm});
            skLineSegment(sketch, "E86.180.7.0", {"start": v(-3.35, -6.81) * mm, "end": v(-5.35, -5.66) * mm});
            skLineSegment(sketch, "E86.183.7.0", {"start": v(-7.13, -9.25) * mm, "end": v(-7.95, -9.25) * mm});
            skLineSegment(sketch, "E86.186.7.0", {"start": v(-3.05, 6.3) * mm, "end": v(-5.05, 5.14) * mm});
            skCircle(sketch, "E86.189.7.0", {"center": v(-5.35, 0) * mm, "radius": 2 * mm, "construction": true});
            skLineSegment(sketch, "E86.191.7.0", {"start": v(-2.75, 9.25) * mm, "end": v(-3.57, 9.25) * mm});
            skLineSegment(sketch, "E86.194.7.0", {"start": v(-7.95, -1.5) * mm, "end": v(-5.65, -2.83) * mm});
            skLineSegment(sketch, "E86.197.7.0", {"start": v(-3.35, 1.15) * mm, "end": v(-3.35, -1.15) * mm});
            skLineSegment(sketch, "E86.200.7.0", {"start": v(-7.35, -1.15) * mm, "end": v(-7.35, 1.15) * mm});
            skLineSegment(sketch, "E86.203.7.0", {"start": v(-2.75, 1.15) * mm, "end": v(-2.75, -1.15) * mm});
            skLineSegment(sketch, "E86.206.7.0", {"start": v(-3.35, 6.81) * mm, "end": v(-5.35, 5.66) * mm});
            skLineSegment(sketch, "E86.209.7.0", {"start": v(-3.35, -6.81) * mm, "end": v(-5.35, -5.66) * mm});
            skLineSegment(sketch, "E86.212.7.0", {"start": v(-3.05, -6.3) * mm, "end": v(-5.05, -5.14) * mm});
            skLineSegment(sketch, "E86.215.7.0", {"start": v(-7.95, 1.5) * mm, "end": v(-7.95, -1.5) * mm});
            skLineSegment(sketch, "E86.218.7.0", {"start": v(-5.65, 2.83) * mm, "end": v(-7.95, 1.5) * mm});
            skLineSegment(sketch, "E86.221.7.0", {"start": v(-3.05, 6.3) * mm, "end": v(-5.05, 5.14) * mm});
            skLineSegment(sketch, "E86.224.7.0", {"start": v(-7.95, -1.5) * mm, "end": v(-5.65, -2.83) * mm});
            skLineSegment(sketch, "E86.227.7.0", {"start": v(-5.35, -2.3) * mm, "end": v(-7.35, -1.15) * mm});
            skLineSegment(sketch, "E86.230.7.0", {"start": v(-4.05, 2.25) * mm, "end": v(-3.05, 1.67) * mm});
            skLineSegment(sketch, "E86.233.7.0", {"start": v(-5.05, 2.83) * mm, "end": v(-3.05, 1.67) * mm});
            skLineSegment(sketch, "E86.236.7.0", {"start": v(-7.35, 1.15) * mm, "end": v(-7.35, -1.15) * mm});
            skLineSegment(sketch, "E86.239.7.0", {"start": v(-3.35, -1.15) * mm, "end": v(-3.35, 1.15) * mm});
            skLineSegment(sketch, "E86.242.7.0", {"start": v(-2.75, 1.15) * mm, "end": v(-2.75, -1.15) * mm});
            skLineSegment(sketch, "E86.245.7.0", {"start": v(-3.35, -1.15) * mm, "end": v(-5.35, -2.3) * mm});
            skLineSegment(sketch, "E86.248.7.0", {"start": v(-7.35, 1.15) * mm, "end": v(-5.35, 2.3) * mm});
            skLineSegment(sketch, "E86.251.7.0", {"start": v(-3.05, -1.67) * mm, "end": v(-5.05, -2.83) * mm});
            skLineSegment(sketch, "E86.254.7.0", {"start": v(-3.05, 1.67) * mm, "end": v(-5.05, 2.83) * mm});
            skLineSegment(sketch, "E86.257.7.0", {"start": v(-3.35, 1.15) * mm, "end": v(-3.35, -1.15) * mm});
            skLineSegment(sketch, "E86.260.7.0", {"start": v(-7.35, -1.15) * mm, "end": v(-5.35, -2.3) * mm});
            skLineSegment(sketch, "E86.263.7.0", {"start": v(-5.35, 2.3) * mm, "end": v(-3.35, 1.15) * mm});
            skLineSegment(sketch, "E86.266.7.0", {"start": v(-5.35, -2.3) * mm, "end": v(-3.35, -1.15) * mm});
            skLineSegment(sketch, "E86.269.7.0", {"start": v(-5.05, -2.83) * mm, "end": v(-3.05, -1.67) * mm});
            skLineSegment(sketch, "E86.272.7.0", {"start": v(-7.35, 1.15) * mm, "end": v(-5.35, 2.3) * mm});
            skLineSegment(sketch, "E86.275.7.0", {"start": v(-3.35, -1.15) * mm, "end": v(-3.35, 1.15) * mm});
            skLineSegment(sketch, "E86.278.7.0", {"start": v(-7.35, -1.15) * mm, "end": v(-5.35, -2.3) * mm});
            skLineSegment(sketch, "E86.281.7.0", {"start": v(-3.35, 1.15) * mm, "end": v(-5.35, 2.3) * mm});
            skLineSegment(sketch, "E86.284.7.0", {"start": v(-5.35, -2.3) * mm, "end": v(-3.35, -1.15) * mm});
            skLineSegment(sketch, "E86.287.7.0", {"start": v(-5.05, -2.83) * mm, "end": v(-3.05, -1.67) * mm});
            skLineSegment(sketch, "E86.290.7.0", {"start": v(-5.35, 2.3) * mm, "end": v(-7.35, 1.15) * mm});
            skLineSegment(sketch, "E86.293.7.0", {"start": v(-5.35, 2.3) * mm, "end": v(-3.35, 1.15) * mm});
            skPoint(sketch, "E86.0.8.0", {"position": v(1.85, -1.5) * mm});
            skPoint(sketch, "E86.1.8.0", {"position": v(0.55, -5.72) * mm});
            skCircle(sketch, "E86.2.8.0", {"center": v(-0.75, 0) * mm, "radius": 2 * mm, "construction": true});
            skPoint(sketch, "E86.4.8.0", {"position": v(-0.75, 3) * mm});
            skPoint(sketch, "E86.5.8.0", {"position": v(0.25, -6.24) * mm});
            skPoint(sketch, "E86.6.8.0", {"position": v(1.85, 1.5) * mm});
            skCircle(sketch, "E86.7.8.0", {"center": v(-0.75, 0) * mm, "radius": 2.6 * mm, "construction": true});
            skPoint(sketch, "E86.9.8.0", {"position": v(0.25, 6.24) * mm});
            skPoint(sketch, "E86.10.8.0", {"position": v(-0.75, -3) * mm});
            skCircle(sketch, "E86.11.8.0", {"center": v(-0.75, -7.97) * mm, "radius": 2.6 * mm, "construction": true});
            skPoint(sketch, "E86.13.8.0", {"position": v(0.55, 5.72) * mm});
            skCircle(sketch, "E86.14.8.0", {"center": v(1.55, -3.98) * mm, "radius": 2.6 * mm, "construction": true});
            skCircle(sketch, "E86.16.8.0", {"center": v(1.55, 3.98) * mm, "radius": 2.6 * mm, "construction": true});
            skCircle(sketch, "E86.18.8.0", {"center": v(-0.75, 7.97) * mm, "radius": 2 * mm, "construction": true});
            skCircle(sketch, "E86.20.8.0", {"center": v(1.55, -3.98) * mm, "radius": 2 * mm, "construction": true});
            skLineSegment(sketch, "E86.22.8.0", {"start": v(0.78, 9.25) * mm, "end": v(-3.35, 9.25) * mm});
            skPoint(sketch, "E86.25.8.0", {"position": v(-3.35, 0) * mm});
            skCircle(sketch, "E86.26.8.0", {"center": v(-0.75, 7.97) * mm, "radius": 2.6 * mm, "construction": true});
            skCircle(sketch, "E86.28.8.0", {"center": v(1.55, 3.98) * mm, "radius": 2 * mm, "construction": true});
            skCircle(sketch, "E86.30.8.0", {"center": v(-0.75, -7.97) * mm, "radius": 2 * mm, "construction": true});
            skArc(sketch, "E86.32.8.0", {"start": v(-2.05, -2.25) * mm, "mid": v(1.85, 0) * mm, "end": v(-2.05, 2.25) * mm, "construction": true});
            skPoint(sketch, "E86.36.8.0", {"position": v(-0.75, 3) * mm});
            skCircle(sketch, "E86.37.8.0", {"center": v(-0.75, 0) * mm, "radius": 2 * mm, "construction": true});
            skPoint(sketch, "E86.39.8.0", {"position": v(1.85, 1.5) * mm});
            skLineSegment(sketch, "E86.40.8.0", {"start": v(-3.35, 6.81) * mm, "end": v(-3.35, 9.12) * mm});
            skLineSegment(sketch, "E86.43.8.0", {"start": v(-1.05, 5.14) * mm, "end": v(-3.35, 6.47) * mm});
            skLineSegment(sketch, "E86.46.8.0", {"start": v(-2.75, 6.81) * mm, "end": v(-2.75, 9.12) * mm});
            skLineSegment(sketch, "E86.49.8.0", {"start": v(4.15, 5.48) * mm, "end": v(1.85, 6.81) * mm});
            skLineSegment(sketch, "E86.52.8.0", {"start": v(4.15, 2.48) * mm, "end": v(4.15, 5.48) * mm});
            skLineSegment(sketch, "E86.55.8.0", {"start": v(4.15, -2.48) * mm, "end": v(4.15, -5.48) * mm});
            skLineSegment(sketch, "E86.58.8.0", {"start": v(-3.35, -6.47) * mm, "end": v(-3.35, -9.25) * mm});
            skLineSegment(sketch, "E86.61.8.0", {"start": v(4.15, -5.48) * mm, "end": v(1.85, -6.81) * mm});
            skPoint(sketch, "E86.64.8.0", {"position": v(0.55, -5.72) * mm});
            skLineSegment(sketch, "E86.65.8.0", {"start": v(-2.75, -6.81) * mm, "end": v(-2.75, -9.12) * mm});
            skPoint(sketch, "E86.68.8.0", {"position": v(0.55, 5.72) * mm});
            skLineSegment(sketch, "E86.69.8.0", {"start": v(3.55, -2.83) * mm, "end": v(3.55, -5.14) * mm});
            skLineSegment(sketch, "E86.72.8.0", {"start": v(3.55, 2.83) * mm, "end": v(3.55, 5.14) * mm});
            skPoint(sketch, "E86.75.8.0", {"position": v(0.25, 6.24) * mm});
            skLineSegment(sketch, "E86.76.8.0", {"start": v(-1.05, -5.14) * mm, "end": v(-3.35, -6.47) * mm});
            skPoint(sketch, "E86.79.8.0", {"position": v(-2.75, 0) * mm});
            skLineSegment(sketch, "E86.80.8.0", {"start": v(1.85, 9.25) * mm, "end": v(1.85, 6.81) * mm});
            skLineSegment(sketch, "E86.83.8.0", {"start": v(1.85, -9.25) * mm, "end": v(1.85, -6.81) * mm});
            skPoint(sketch, "E86.86.8.0", {"position": v(-3.35, 0) * mm});
            skPoint(sketch, "E86.87.8.0", {"position": v(0.25, -6.24) * mm});
            skPoint(sketch, "E86.88.8.0", {"position": v(-0.75, -3) * mm});
            skLineSegment(sketch, "E86.89.8.0", {"start": v(1.25, -9.12) * mm, "end": v(1.25, -6.81) * mm});
            skLineSegment(sketch, "E86.92.8.0", {"start": v(1.25, 9.12) * mm, "end": v(1.25, 6.81) * mm});
            skPoint(sketch, "E86.95.8.0", {"position": v(1.85, -1.5) * mm});
            skLineSegment(sketch, "E86.96.8.0", {"start": v(-3.35, 1.5) * mm, "end": v(-1.05, 2.83) * mm});
            skLineSegment(sketch, "E86.99.8.0", {"start": v(-0.45, 5.14) * mm, "end": v(-0.45, 2.83) * mm});
            skLineSegment(sketch, "E86.102.8.0", {"start": v(1.55, 1.67) * mm, "end": v(3.55, 2.83) * mm});
            skLineSegment(sketch, "E86.105.8.0", {"start": v(-0.75, -5.66) * mm, "end": v(-2.75, -6.81) * mm});
            skLineSegment(sketch, "E86.108.8.0", {"start": v(-1.05, 5.14) * mm, "end": v(-1.05, 2.83) * mm});
            skLineSegment(sketch, "E86.111.8.0", {"start": v(-0.45, -5.14) * mm, "end": v(-0.45, -2.83) * mm});
            skLineSegment(sketch, "E86.114.8.0", {"start": v(1.85, -1.15) * mm, "end": v(4.15, -2.48) * mm});
            skLineSegment(sketch, "E86.117.8.0", {"start": v(1.85, -1.15) * mm, "end": v(1.85, 1.15) * mm});
            skLineSegment(sketch, "E86.120.8.0", {"start": v(1.85, -9.25) * mm, "end": v(1.03, -9.25) * mm});
            skLineSegment(sketch, "E86.123.8.0", {"start": v(1.55, -1.67) * mm, "end": v(3.55, -2.83) * mm});
            skLineSegment(sketch, "E86.126.8.0", {"start": v(3.55, -5.14) * mm, "end": v(1.55, -6.3) * mm});
            skCircle(sketch, "E86.129.8.0", {"center": v(-0.75, 0) * mm, "radius": 2 * mm, "construction": true});
            skLineSegment(sketch, "E86.131.8.0", {"start": v(-2.75, -9.12) * mm, "end": v(-2.53, -9.25) * mm});
            skLineSegment(sketch, "E86.134.8.0", {"start": v(3.55, 5.14) * mm, "end": v(1.55, 6.3) * mm});
            skLineSegment(sketch, "E86.137.8.0", {"start": v(-1.05, -2.83) * mm, "end": v(-3.35, -1.5) * mm});
            skLineSegment(sketch, "E86.140.8.0", {"start": v(-3.35, 6.47) * mm, "end": v(-3.35, 9.25) * mm});
            skPoint(sketch, "E86.143.8.0", {"position": v(-2.75, 0) * mm});
            skLineSegment(sketch, "E86.144.8.0", {"start": v(-1.05, -5.14) * mm, "end": v(-1.05, -2.83) * mm});
            skLineSegment(sketch, "E86.147.8.0", {"start": v(-3.35, -6.81) * mm, "end": v(-3.35, -9.12) * mm});
            skLineSegment(sketch, "E86.150.8.0", {"start": v(1.85, 1.15) * mm, "end": v(4.15, 2.48) * mm});
            skLineSegment(sketch, "E86.153.8.0", {"start": v(-0.75, 5.66) * mm, "end": v(-2.75, 6.81) * mm});
            skLineSegment(sketch, "E86.156.8.0", {"start": v(-3.35, -1.5) * mm, "end": v(-3.35, 0) * mm});
            skLineSegment(sketch, "E86.159.8.0", {"start": v(1.03, 9.25) * mm, "end": v(1.25, 9.12) * mm});
            skLineSegment(sketch, "E86.162.8.0", {"start": v(-2.75, 9.12) * mm, "end": v(-2.53, 9.25) * mm});
            skLineSegment(sketch, "E86.165.8.0", {"start": v(1.85, -1.15) * mm, "end": v(1.85, 1.15) * mm});
            skLineSegment(sketch, "E86.168.8.0", {"start": v(-3.35, 1.5) * mm, "end": v(-1.05, 2.83) * mm});
            skLineSegment(sketch, "E86.171.8.0", {"start": v(1.55, -6.3) * mm, "end": v(-0.45, -5.14) * mm});
            skLineSegment(sketch, "E86.174.8.0", {"start": v(1.03, -9.25) * mm, "end": v(1.25, -9.12) * mm});
            skLineSegment(sketch, "E86.177.8.0", {"start": v(1.25, 6.81) * mm, "end": v(-0.75, 5.66) * mm});
            skLineSegment(sketch, "E86.180.8.0", {"start": v(1.25, -6.81) * mm, "end": v(-0.75, -5.66) * mm});
            skLineSegment(sketch, "E86.183.8.0", {"start": v(-2.53, -9.25) * mm, "end": v(-3.35, -9.25) * mm});
            skLineSegment(sketch, "E86.186.8.0", {"start": v(1.55, 6.3) * mm, "end": v(-0.45, 5.14) * mm});
            skCircle(sketch, "E86.189.8.0", {"center": v(-0.75, 0) * mm, "radius": 2 * mm, "construction": true});
            skLineSegment(sketch, "E86.191.8.0", {"start": v(1.85, 9.25) * mm, "end": v(1.03, 9.25) * mm});
            skLineSegment(sketch, "E86.194.8.0", {"start": v(-3.35, -1.5) * mm, "end": v(-1.05, -2.83) * mm});
            skLineSegment(sketch, "E86.197.8.0", {"start": v(1.25, 1.15) * mm, "end": v(1.25, -1.15) * mm});
            skLineSegment(sketch, "E86.200.8.0", {"start": v(-2.75, -1.15) * mm, "end": v(-2.75, 1.15) * mm});
            skLineSegment(sketch, "E86.203.8.0", {"start": v(1.85, 1.15) * mm, "end": v(1.85, -1.15) * mm});
            skLineSegment(sketch, "E86.206.8.0", {"start": v(1.25, 6.81) * mm, "end": v(-0.75, 5.66) * mm});
            skLineSegment(sketch, "E86.209.8.0", {"start": v(1.25, -6.81) * mm, "end": v(-0.75, -5.66) * mm});
            skLineSegment(sketch, "E86.212.8.0", {"start": v(1.55, -6.3) * mm, "end": v(-0.45, -5.14) * mm});
            skLineSegment(sketch, "E86.215.8.0", {"start": v(-3.35, 1.5) * mm, "end": v(-3.35, -1.5) * mm});
            skLineSegment(sketch, "E86.218.8.0", {"start": v(-1.05, 2.83) * mm, "end": v(-3.35, 1.5) * mm});
            skLineSegment(sketch, "E86.221.8.0", {"start": v(1.55, 6.3) * mm, "end": v(-0.45, 5.14) * mm});
            skLineSegment(sketch, "E86.224.8.0", {"start": v(-3.35, -1.5) * mm, "end": v(-1.05, -2.83) * mm});
            skLineSegment(sketch, "E86.227.8.0", {"start": v(-0.75, -2.3) * mm, "end": v(-2.75, -1.15) * mm});
            skLineSegment(sketch, "E86.230.8.0", {"start": v(0.55, 2.25) * mm, "end": v(1.55, 1.67) * mm});
            skLineSegment(sketch, "E86.233.8.0", {"start": v(-0.45, 2.83) * mm, "end": v(1.55, 1.67) * mm});
            skLineSegment(sketch, "E86.236.8.0", {"start": v(-2.75, 1.15) * mm, "end": v(-2.75, -1.15) * mm});
            skLineSegment(sketch, "E86.239.8.0", {"start": v(1.25, -1.15) * mm, "end": v(1.25, 1.15) * mm});
            skLineSegment(sketch, "E86.242.8.0", {"start": v(1.85, 1.15) * mm, "end": v(1.85, -1.15) * mm});
            skLineSegment(sketch, "E86.245.8.0", {"start": v(1.25, -1.15) * mm, "end": v(-0.75, -2.3) * mm});
            skLineSegment(sketch, "E86.248.8.0", {"start": v(-2.75, 1.15) * mm, "end": v(-0.75, 2.3) * mm});
            skLineSegment(sketch, "E86.251.8.0", {"start": v(1.55, -1.67) * mm, "end": v(-0.45, -2.83) * mm});
            skLineSegment(sketch, "E86.254.8.0", {"start": v(1.55, 1.67) * mm, "end": v(-0.45, 2.83) * mm});
            skLineSegment(sketch, "E86.257.8.0", {"start": v(1.25, 1.15) * mm, "end": v(1.25, -1.15) * mm});
            skLineSegment(sketch, "E86.260.8.0", {"start": v(-2.75, -1.15) * mm, "end": v(-0.75, -2.3) * mm});
            skLineSegment(sketch, "E86.263.8.0", {"start": v(-0.75, 2.3) * mm, "end": v(1.25, 1.15) * mm});
            skLineSegment(sketch, "E86.266.8.0", {"start": v(-0.75, -2.3) * mm, "end": v(1.25, -1.15) * mm});
            skLineSegment(sketch, "E86.269.8.0", {"start": v(-0.45, -2.83) * mm, "end": v(1.55, -1.67) * mm});
            skLineSegment(sketch, "E86.272.8.0", {"start": v(-2.75, 1.15) * mm, "end": v(-0.75, 2.3) * mm});
            skLineSegment(sketch, "E86.275.8.0", {"start": v(1.25, -1.15) * mm, "end": v(1.25, 1.15) * mm});
            skLineSegment(sketch, "E86.278.8.0", {"start": v(-2.75, -1.15) * mm, "end": v(-0.75, -2.3) * mm});
            skLineSegment(sketch, "E86.281.8.0", {"start": v(1.25, 1.15) * mm, "end": v(-0.75, 2.3) * mm});
            skLineSegment(sketch, "E86.284.8.0", {"start": v(-0.75, -2.3) * mm, "end": v(1.25, -1.15) * mm});
            skLineSegment(sketch, "E86.287.8.0", {"start": v(-0.45, -2.83) * mm, "end": v(1.55, -1.67) * mm});
            skLineSegment(sketch, "E86.290.8.0", {"start": v(-0.75, 2.3) * mm, "end": v(-2.75, 1.15) * mm});
            skLineSegment(sketch, "E86.293.8.0", {"start": v(-0.75, 2.3) * mm, "end": v(1.25, 1.15) * mm});
            skPoint(sketch, "E86.0.9.0", {"position": v(6.45, -1.5) * mm});
            skPoint(sketch, "E86.1.9.0", {"position": v(5.15, -5.72) * mm});
            skCircle(sketch, "E86.2.9.0", {"center": v(3.85, 0) * mm, "radius": 2 * mm, "construction": true});
            skPoint(sketch, "E86.4.9.0", {"position": v(3.85, 3) * mm});
            skPoint(sketch, "E86.5.9.0", {"position": v(4.85, -6.24) * mm});
            skPoint(sketch, "E86.6.9.0", {"position": v(6.45, 1.5) * mm});
            skCircle(sketch, "E86.7.9.0", {"center": v(3.85, 0) * mm, "radius": 2.6 * mm, "construction": true});
            skPoint(sketch, "E86.9.9.0", {"position": v(4.85, 6.24) * mm});
            skPoint(sketch, "E86.10.9.0", {"position": v(3.85, -3) * mm});
            skCircle(sketch, "E86.11.9.0", {"center": v(3.85, -7.97) * mm, "radius": 2.6 * mm, "construction": true});
            skPoint(sketch, "E86.13.9.0", {"position": v(5.15, 5.72) * mm});
            skCircle(sketch, "E86.14.9.0", {"center": v(6.15, -3.98) * mm, "radius": 2.6 * mm, "construction": true});
            skCircle(sketch, "E86.16.9.0", {"center": v(6.15, 3.98) * mm, "radius": 2.6 * mm, "construction": true});
            skCircle(sketch, "E86.18.9.0", {"center": v(3.85, 7.97) * mm, "radius": 2 * mm, "construction": true});
            skCircle(sketch, "E86.20.9.0", {"center": v(6.15, -3.98) * mm, "radius": 2 * mm, "construction": true});
            skLineSegment(sketch, "E86.22.9.0", {"start": v(5.38, 9.25) * mm, "end": v(1.25, 9.25) * mm});
            skPoint(sketch, "E86.25.9.0", {"position": v(1.25, 0) * mm});
            skCircle(sketch, "E86.26.9.0", {"center": v(3.85, 7.97) * mm, "radius": 2.6 * mm, "construction": true});
            skCircle(sketch, "E86.28.9.0", {"center": v(6.15, 3.98) * mm, "radius": 2 * mm, "construction": true});
            skCircle(sketch, "E86.30.9.0", {"center": v(3.85, -7.97) * mm, "radius": 2 * mm, "construction": true});
            skArc(sketch, "E86.32.9.0", {"start": v(2.55, -2.25) * mm, "mid": v(6.45, 0) * mm, "end": v(2.55, 2.25) * mm, "construction": true});
            skPoint(sketch, "E86.36.9.0", {"position": v(3.85, 3) * mm});
            skCircle(sketch, "E86.37.9.0", {"center": v(3.85, 0) * mm, "radius": 2 * mm, "construction": true});
            skPoint(sketch, "E86.39.9.0", {"position": v(6.45, 1.5) * mm});
            skLineSegment(sketch, "E86.40.9.0", {"start": v(1.25, 6.81) * mm, "end": v(1.25, 9.12) * mm});
            skLineSegment(sketch, "E86.43.9.0", {"start": v(3.55, 5.14) * mm, "end": v(1.25, 6.47) * mm});
            skLineSegment(sketch, "E86.46.9.0", {"start": v(1.85, 6.81) * mm, "end": v(1.85, 9.12) * mm});
            skLineSegment(sketch, "E86.49.9.0", {"start": v(8.75, 5.48) * mm, "end": v(6.45, 6.81) * mm});
            skLineSegment(sketch, "E86.52.9.0", {"start": v(8.75, 2.48) * mm, "end": v(8.75, 5.48) * mm});
            skLineSegment(sketch, "E86.55.9.0", {"start": v(8.75, -2.48) * mm, "end": v(8.75, -5.48) * mm});
            skLineSegment(sketch, "E86.58.9.0", {"start": v(1.25, -6.47) * mm, "end": v(1.25, -9.25) * mm});
            skLineSegment(sketch, "E86.61.9.0", {"start": v(8.75, -5.48) * mm, "end": v(6.45, -6.81) * mm});
            skPoint(sketch, "E86.64.9.0", {"position": v(5.15, -5.72) * mm});
            skLineSegment(sketch, "E86.65.9.0", {"start": v(1.85, -6.81) * mm, "end": v(1.85, -9.12) * mm});
            skPoint(sketch, "E86.68.9.0", {"position": v(5.15, 5.72) * mm});
            skLineSegment(sketch, "E86.69.9.0", {"start": v(8.15, -2.83) * mm, "end": v(8.15, -5.14) * mm});
            skLineSegment(sketch, "E86.72.9.0", {"start": v(8.15, 2.83) * mm, "end": v(8.15, 5.14) * mm});
            skPoint(sketch, "E86.75.9.0", {"position": v(4.85, 6.24) * mm});
            skLineSegment(sketch, "E86.76.9.0", {"start": v(3.55, -5.14) * mm, "end": v(1.25, -6.47) * mm});
            skPoint(sketch, "E86.79.9.0", {"position": v(1.85, 0) * mm});
            skLineSegment(sketch, "E86.80.9.0", {"start": v(6.45, 9.25) * mm, "end": v(6.45, 6.81) * mm});
            skLineSegment(sketch, "E86.83.9.0", {"start": v(6.45, -9.25) * mm, "end": v(6.45, -6.81) * mm});
            skPoint(sketch, "E86.86.9.0", {"position": v(1.25, 0) * mm});
            skPoint(sketch, "E86.87.9.0", {"position": v(4.85, -6.24) * mm});
            skPoint(sketch, "E86.88.9.0", {"position": v(3.85, -3) * mm});
            skLineSegment(sketch, "E86.89.9.0", {"start": v(5.85, -9.12) * mm, "end": v(5.85, -6.81) * mm});
            skLineSegment(sketch, "E86.92.9.0", {"start": v(5.85, 9.12) * mm, "end": v(5.85, 6.81) * mm});
            skPoint(sketch, "E86.95.9.0", {"position": v(6.45, -1.5) * mm});
            skLineSegment(sketch, "E86.96.9.0", {"start": v(1.25, 1.5) * mm, "end": v(3.55, 2.83) * mm});
            skLineSegment(sketch, "E86.99.9.0", {"start": v(4.15, 5.14) * mm, "end": v(4.15, 2.83) * mm});
            skLineSegment(sketch, "E86.102.9.0", {"start": v(6.15, 1.67) * mm, "end": v(8.15, 2.83) * mm});
            skLineSegment(sketch, "E86.105.9.0", {"start": v(3.85, -5.66) * mm, "end": v(1.85, -6.81) * mm});
            skLineSegment(sketch, "E86.108.9.0", {"start": v(3.55, 5.14) * mm, "end": v(3.55, 2.83) * mm});
            skLineSegment(sketch, "E86.111.9.0", {"start": v(4.15, -5.14) * mm, "end": v(4.15, -2.83) * mm});
            skLineSegment(sketch, "E86.114.9.0", {"start": v(6.45, -1.15) * mm, "end": v(8.75, -2.48) * mm});
            skLineSegment(sketch, "E86.117.9.0", {"start": v(6.45, -1.15) * mm, "end": v(6.45, 1.15) * mm});
            skLineSegment(sketch, "E86.120.9.0", {"start": v(6.45, -9.25) * mm, "end": v(5.63, -9.25) * mm});
            skLineSegment(sketch, "E86.123.9.0", {"start": v(6.15, -1.67) * mm, "end": v(8.15, -2.83) * mm});
            skLineSegment(sketch, "E86.126.9.0", {"start": v(8.15, -5.14) * mm, "end": v(6.15, -6.3) * mm});
            skCircle(sketch, "E86.129.9.0", {"center": v(3.85, 0) * mm, "radius": 2 * mm, "construction": true});
            skLineSegment(sketch, "E86.131.9.0", {"start": v(1.85, -9.12) * mm, "end": v(2.07, -9.25) * mm});
            skLineSegment(sketch, "E86.134.9.0", {"start": v(8.15, 5.14) * mm, "end": v(6.15, 6.3) * mm});
            skLineSegment(sketch, "E86.137.9.0", {"start": v(3.55, -2.83) * mm, "end": v(1.25, -1.5) * mm});
            skLineSegment(sketch, "E86.140.9.0", {"start": v(1.25, 6.47) * mm, "end": v(1.25, 9.25) * mm});
            skPoint(sketch, "E86.143.9.0", {"position": v(1.85, 0) * mm});
            skLineSegment(sketch, "E86.144.9.0", {"start": v(3.55, -5.14) * mm, "end": v(3.55, -2.83) * mm});
            skLineSegment(sketch, "E86.147.9.0", {"start": v(1.25, -6.81) * mm, "end": v(1.25, -9.12) * mm});
            skLineSegment(sketch, "E86.150.9.0", {"start": v(6.45, 1.15) * mm, "end": v(8.75, 2.48) * mm});
            skLineSegment(sketch, "E86.153.9.0", {"start": v(3.85, 5.66) * mm, "end": v(1.85, 6.81) * mm});
            skLineSegment(sketch, "E86.156.9.0", {"start": v(1.25, -1.5) * mm, "end": v(1.25, 0) * mm});
            skLineSegment(sketch, "E86.159.9.0", {"start": v(5.63, 9.25) * mm, "end": v(5.85, 9.12) * mm});
            skLineSegment(sketch, "E86.162.9.0", {"start": v(1.85, 9.12) * mm, "end": v(2.07, 9.25) * mm});
            skLineSegment(sketch, "E86.165.9.0", {"start": v(6.45, -1.15) * mm, "end": v(6.45, 1.15) * mm});
            skLineSegment(sketch, "E86.168.9.0", {"start": v(1.25, 1.5) * mm, "end": v(3.55, 2.83) * mm});
            skLineSegment(sketch, "E86.171.9.0", {"start": v(6.15, -6.3) * mm, "end": v(4.15, -5.14) * mm});
            skLineSegment(sketch, "E86.174.9.0", {"start": v(5.63, -9.25) * mm, "end": v(5.85, -9.12) * mm});
            skLineSegment(sketch, "E86.177.9.0", {"start": v(5.85, 6.81) * mm, "end": v(3.85, 5.66) * mm});
            skLineSegment(sketch, "E86.180.9.0", {"start": v(5.85, -6.81) * mm, "end": v(3.85, -5.66) * mm});
            skLineSegment(sketch, "E86.183.9.0", {"start": v(2.07, -9.25) * mm, "end": v(1.25, -9.25) * mm});
            skLineSegment(sketch, "E86.186.9.0", {"start": v(6.15, 6.3) * mm, "end": v(4.15, 5.14) * mm});
            skCircle(sketch, "E86.189.9.0", {"center": v(3.85, 0) * mm, "radius": 2 * mm, "construction": true});
            skLineSegment(sketch, "E86.191.9.0", {"start": v(6.45, 9.25) * mm, "end": v(5.63, 9.25) * mm});
            skLineSegment(sketch, "E86.194.9.0", {"start": v(1.25, -1.5) * mm, "end": v(3.55, -2.83) * mm});
            skLineSegment(sketch, "E86.197.9.0", {"start": v(5.85, 1.15) * mm, "end": v(5.85, -1.15) * mm});
            skLineSegment(sketch, "E86.200.9.0", {"start": v(1.85, -1.15) * mm, "end": v(1.85, 1.15) * mm});
            skLineSegment(sketch, "E86.203.9.0", {"start": v(6.45, 1.15) * mm, "end": v(6.45, -1.15) * mm});
            skLineSegment(sketch, "E86.206.9.0", {"start": v(5.85, 6.81) * mm, "end": v(3.85, 5.66) * mm});
            skLineSegment(sketch, "E86.209.9.0", {"start": v(5.85, -6.81) * mm, "end": v(3.85, -5.66) * mm});
            skLineSegment(sketch, "E86.212.9.0", {"start": v(6.15, -6.3) * mm, "end": v(4.15, -5.14) * mm});
            skLineSegment(sketch, "E86.215.9.0", {"start": v(1.25, 1.5) * mm, "end": v(1.25, -1.5) * mm});
            skLineSegment(sketch, "E86.218.9.0", {"start": v(3.55, 2.83) * mm, "end": v(1.25, 1.5) * mm});
            skLineSegment(sketch, "E86.221.9.0", {"start": v(6.15, 6.3) * mm, "end": v(4.15, 5.14) * mm});
            skLineSegment(sketch, "E86.224.9.0", {"start": v(1.25, -1.5) * mm, "end": v(3.55, -2.83) * mm});
            skLineSegment(sketch, "E86.227.9.0", {"start": v(3.85, -2.3) * mm, "end": v(1.85, -1.15) * mm});
            skLineSegment(sketch, "E86.230.9.0", {"start": v(5.15, 2.25) * mm, "end": v(6.15, 1.67) * mm});
            skLineSegment(sketch, "E86.233.9.0", {"start": v(4.15, 2.83) * mm, "end": v(6.15, 1.67) * mm});
            skLineSegment(sketch, "E86.236.9.0", {"start": v(1.85, 1.15) * mm, "end": v(1.85, -1.15) * mm});
            skLineSegment(sketch, "E86.239.9.0", {"start": v(5.85, -1.15) * mm, "end": v(5.85, 1.15) * mm});
            skLineSegment(sketch, "E86.242.9.0", {"start": v(6.45, 1.15) * mm, "end": v(6.45, -1.15) * mm});
            skLineSegment(sketch, "E86.245.9.0", {"start": v(5.85, -1.15) * mm, "end": v(3.85, -2.3) * mm});
            skLineSegment(sketch, "E86.248.9.0", {"start": v(1.85, 1.15) * mm, "end": v(3.85, 2.3) * mm});
            skLineSegment(sketch, "E86.251.9.0", {"start": v(6.15, -1.67) * mm, "end": v(4.15, -2.83) * mm});
            skLineSegment(sketch, "E86.254.9.0", {"start": v(6.15, 1.67) * mm, "end": v(4.15, 2.83) * mm});
            skLineSegment(sketch, "E86.257.9.0", {"start": v(5.85, 1.15) * mm, "end": v(5.85, -1.15) * mm});
            skLineSegment(sketch, "E86.260.9.0", {"start": v(1.85, -1.15) * mm, "end": v(3.85, -2.3) * mm});
            skLineSegment(sketch, "E86.263.9.0", {"start": v(3.85, 2.3) * mm, "end": v(5.85, 1.15) * mm});
            skLineSegment(sketch, "E86.266.9.0", {"start": v(3.85, -2.3) * mm, "end": v(5.85, -1.15) * mm});
            skLineSegment(sketch, "E86.269.9.0", {"start": v(4.15, -2.83) * mm, "end": v(6.15, -1.67) * mm});
            skLineSegment(sketch, "E86.272.9.0", {"start": v(1.85, 1.15) * mm, "end": v(3.85, 2.3) * mm});
            skLineSegment(sketch, "E86.275.9.0", {"start": v(5.85, -1.15) * mm, "end": v(5.85, 1.15) * mm});
            skLineSegment(sketch, "E86.278.9.0", {"start": v(1.85, -1.15) * mm, "end": v(3.85, -2.3) * mm});
            skLineSegment(sketch, "E86.281.9.0", {"start": v(5.85, 1.15) * mm, "end": v(3.85, 2.3) * mm});
            skLineSegment(sketch, "E86.284.9.0", {"start": v(3.85, -2.3) * mm, "end": v(5.85, -1.15) * mm});
            skLineSegment(sketch, "E86.287.9.0", {"start": v(4.15, -2.83) * mm, "end": v(6.15, -1.67) * mm});
            skLineSegment(sketch, "E86.290.9.0", {"start": v(3.85, 2.3) * mm, "end": v(1.85, 1.15) * mm});
            skLineSegment(sketch, "E86.293.9.0", {"start": v(3.85, 2.3) * mm, "end": v(5.85, 1.15) * mm});
            skPoint(sketch, "E86.0.10.0", {"position": v(11.05, -1.5) * mm});
            skPoint(sketch, "E86.1.10.0", {"position": v(9.75, -5.72) * mm});
            skCircle(sketch, "E86.2.10.0", {"center": v(8.45, 0) * mm, "radius": 2 * mm, "construction": true});
            skPoint(sketch, "E86.4.10.0", {"position": v(8.45, 3) * mm});
            skPoint(sketch, "E86.5.10.0", {"position": v(9.45, -6.24) * mm});
            skPoint(sketch, "E86.6.10.0", {"position": v(11.05, 1.5) * mm});
            skCircle(sketch, "E86.7.10.0", {"center": v(8.45, 0) * mm, "radius": 2.6 * mm, "construction": true});
            skPoint(sketch, "E86.9.10.0", {"position": v(9.45, 6.24) * mm});
            skPoint(sketch, "E86.10.10.0", {"position": v(8.45, -3) * mm});
            skCircle(sketch, "E86.11.10.0", {"center": v(8.45, -7.97) * mm, "radius": 2.6 * mm, "construction": true});
            skPoint(sketch, "E86.13.10.0", {"position": v(9.75, 5.72) * mm});
            skCircle(sketch, "E86.14.10.0", {"center": v(10.75, -3.98) * mm, "radius": 2.6 * mm, "construction": true});
            skCircle(sketch, "E86.16.10.0", {"center": v(10.75, 3.98) * mm, "radius": 2.6 * mm, "construction": true});
            skCircle(sketch, "E86.18.10.0", {"center": v(8.45, 7.97) * mm, "radius": 2 * mm, "construction": true});
            skCircle(sketch, "E86.20.10.0", {"center": v(10.75, -3.98) * mm, "radius": 2 * mm, "construction": true});
            skLineSegment(sketch, "E86.22.10.0", {"start": v(9.98, 9.25) * mm, "end": v(5.85, 9.25) * mm});
            skPoint(sketch, "E86.25.10.0", {"position": v(5.85, 0) * mm});
            skCircle(sketch, "E86.26.10.0", {"center": v(8.45, 7.97) * mm, "radius": 2.6 * mm, "construction": true});
            skCircle(sketch, "E86.28.10.0", {"center": v(10.75, 3.98) * mm, "radius": 2 * mm, "construction": true});
            skCircle(sketch, "E86.30.10.0", {"center": v(8.45, -7.97) * mm, "radius": 2 * mm, "construction": true});
            skArc(sketch, "E86.32.10.0", {"start": v(7.15, -2.25) * mm, "mid": v(11.05, 0) * mm, "end": v(7.15, 2.25) * mm, "construction": true});
            skPoint(sketch, "E86.36.10.0", {"position": v(8.45, 3) * mm});
            skCircle(sketch, "E86.37.10.0", {"center": v(8.45, 0) * mm, "radius": 2 * mm, "construction": true});
            skPoint(sketch, "E86.39.10.0", {"position": v(11.05, 1.5) * mm});
            skLineSegment(sketch, "E86.40.10.0", {"start": v(5.85, 6.81) * mm, "end": v(5.85, 9.12) * mm});
            skLineSegment(sketch, "E86.43.10.0", {"start": v(8.15, 5.14) * mm, "end": v(5.85, 6.47) * mm});
            skLineSegment(sketch, "E86.46.10.0", {"start": v(6.45, 6.81) * mm, "end": v(6.45, 9.12) * mm});
            skLineSegment(sketch, "E86.49.10.0", {"start": v(13.35, 5.48) * mm, "end": v(11.05, 6.81) * mm});
            skLineSegment(sketch, "E86.52.10.0", {"start": v(13.35, 2.48) * mm, "end": v(13.35, 5.48) * mm});
            skLineSegment(sketch, "E86.55.10.0", {"start": v(13.35, -2.48) * mm, "end": v(13.35, -5.48) * mm});
            skLineSegment(sketch, "E86.58.10.0", {"start": v(5.85, -6.47) * mm, "end": v(5.85, -9.25) * mm});
            skLineSegment(sketch, "E86.61.10.0", {"start": v(13.35, -5.48) * mm, "end": v(11.05, -6.81) * mm});
            skPoint(sketch, "E86.64.10.0", {"position": v(9.75, -5.72) * mm});
            skLineSegment(sketch, "E86.65.10.0", {"start": v(6.45, -6.81) * mm, "end": v(6.45, -9.12) * mm});
            skPoint(sketch, "E86.68.10.0", {"position": v(9.75, 5.72) * mm});
            skLineSegment(sketch, "E86.69.10.0", {"start": v(12.75, -2.83) * mm, "end": v(12.75, -5.14) * mm});
            skLineSegment(sketch, "E86.72.10.0", {"start": v(12.75, 2.83) * mm, "end": v(12.75, 5.14) * mm});
            skPoint(sketch, "E86.75.10.0", {"position": v(9.45, 6.24) * mm});
            skLineSegment(sketch, "E86.76.10.0", {"start": v(8.15, -5.14) * mm, "end": v(5.85, -6.47) * mm});
            skPoint(sketch, "E86.79.10.0", {"position": v(6.45, 0) * mm});
            skLineSegment(sketch, "E86.80.10.0", {"start": v(11.05, 9.25) * mm, "end": v(11.05, 6.81) * mm});
            skLineSegment(sketch, "E86.83.10.0", {"start": v(11.05, -9.25) * mm, "end": v(11.05, -6.81) * mm});
            skPoint(sketch, "E86.86.10.0", {"position": v(5.85, 0) * mm});
            skPoint(sketch, "E86.87.10.0", {"position": v(9.45, -6.24) * mm});
            skPoint(sketch, "E86.88.10.0", {"position": v(8.45, -3) * mm});
            skLineSegment(sketch, "E86.89.10.0", {"start": v(10.45, -9.12) * mm, "end": v(10.45, -6.81) * mm});
            skLineSegment(sketch, "E86.92.10.0", {"start": v(10.45, 9.12) * mm, "end": v(10.45, 6.81) * mm});
            skPoint(sketch, "E86.95.10.0", {"position": v(11.05, -1.5) * mm});
            skLineSegment(sketch, "E86.96.10.0", {"start": v(5.85, 1.5) * mm, "end": v(8.15, 2.83) * mm});
            skLineSegment(sketch, "E86.99.10.0", {"start": v(8.75, 5.14) * mm, "end": v(8.75, 2.83) * mm});
            skLineSegment(sketch, "E86.102.10.0", {"start": v(10.75, 1.67) * mm, "end": v(12.75, 2.83) * mm});
            skLineSegment(sketch, "E86.105.10.0", {"start": v(8.45, -5.66) * mm, "end": v(6.45, -6.81) * mm});
            skLineSegment(sketch, "E86.108.10.0", {"start": v(8.15, 5.14) * mm, "end": v(8.15, 2.83) * mm});
            skLineSegment(sketch, "E86.111.10.0", {"start": v(8.75, -5.14) * mm, "end": v(8.75, -2.83) * mm});
            skLineSegment(sketch, "E86.114.10.0", {"start": v(11.05, -1.15) * mm, "end": v(13.35, -2.48) * mm});
            skLineSegment(sketch, "E86.117.10.0", {"start": v(11.05, -1.15) * mm, "end": v(11.05, 1.15) * mm});
            skLineSegment(sketch, "E86.120.10.0", {"start": v(11.05, -9.25) * mm, "end": v(10.23, -9.25) * mm});
            skLineSegment(sketch, "E86.123.10.0", {"start": v(10.75, -1.67) * mm, "end": v(12.75, -2.83) * mm});
            skLineSegment(sketch, "E86.126.10.0", {"start": v(12.75, -5.14) * mm, "end": v(10.75, -6.3) * mm});
            skCircle(sketch, "E86.129.10.0", {"center": v(8.45, 0) * mm, "radius": 2 * mm, "construction": true});
            skLineSegment(sketch, "E86.131.10.0", {"start": v(6.45, -9.12) * mm, "end": v(6.67, -9.25) * mm});
            skLineSegment(sketch, "E86.134.10.0", {"start": v(12.75, 5.14) * mm, "end": v(10.75, 6.3) * mm});
            skLineSegment(sketch, "E86.137.10.0", {"start": v(8.15, -2.83) * mm, "end": v(5.85, -1.5) * mm});
            skLineSegment(sketch, "E86.140.10.0", {"start": v(5.85, 6.47) * mm, "end": v(5.85, 9.25) * mm});
            skPoint(sketch, "E86.143.10.0", {"position": v(6.45, 0) * mm});
            skLineSegment(sketch, "E86.144.10.0", {"start": v(8.15, -5.14) * mm, "end": v(8.15, -2.83) * mm});
            skLineSegment(sketch, "E86.147.10.0", {"start": v(5.85, -6.81) * mm, "end": v(5.85, -9.12) * mm});
            skLineSegment(sketch, "E86.150.10.0", {"start": v(11.05, 1.15) * mm, "end": v(13.35, 2.48) * mm});
            skLineSegment(sketch, "E86.153.10.0", {"start": v(8.45, 5.66) * mm, "end": v(6.45, 6.81) * mm});
            skLineSegment(sketch, "E86.156.10.0", {"start": v(5.85, -1.5) * mm, "end": v(5.85, 0) * mm});
            skLineSegment(sketch, "E86.159.10.0", {"start": v(10.23, 9.25) * mm, "end": v(10.45, 9.12) * mm});
            skLineSegment(sketch, "E86.162.10.0", {"start": v(6.45, 9.12) * mm, "end": v(6.67, 9.25) * mm});
            skLineSegment(sketch, "E86.165.10.0", {"start": v(11.05, -1.15) * mm, "end": v(11.05, 1.15) * mm});
            skLineSegment(sketch, "E86.168.10.0", {"start": v(5.85, 1.5) * mm, "end": v(8.15, 2.83) * mm});
            skLineSegment(sketch, "E86.171.10.0", {"start": v(10.75, -6.3) * mm, "end": v(8.75, -5.14) * mm});
            skLineSegment(sketch, "E86.174.10.0", {"start": v(10.23, -9.25) * mm, "end": v(10.45, -9.12) * mm});
            skLineSegment(sketch, "E86.177.10.0", {"start": v(10.45, 6.81) * mm, "end": v(8.45, 5.66) * mm});
            skLineSegment(sketch, "E86.180.10.0", {"start": v(10.45, -6.81) * mm, "end": v(8.45, -5.66) * mm});
            skLineSegment(sketch, "E86.183.10.0", {"start": v(6.67, -9.25) * mm, "end": v(5.85, -9.25) * mm});
            skLineSegment(sketch, "E86.186.10.0", {"start": v(10.75, 6.3) * mm, "end": v(8.75, 5.14) * mm});
            skCircle(sketch, "E86.189.10.0", {"center": v(8.45, 0) * mm, "radius": 2 * mm, "construction": true});
            skLineSegment(sketch, "E86.191.10.0", {"start": v(11.05, 9.25) * mm, "end": v(10.23, 9.25) * mm});
            skLineSegment(sketch, "E86.194.10.0", {"start": v(5.85, -1.5) * mm, "end": v(8.15, -2.83) * mm});
            skLineSegment(sketch, "E86.197.10.0", {"start": v(10.45, 1.15) * mm, "end": v(10.45, -1.15) * mm});
            skLineSegment(sketch, "E86.200.10.0", {"start": v(6.45, -1.15) * mm, "end": v(6.45, 1.15) * mm});
            skLineSegment(sketch, "E86.203.10.0", {"start": v(11.05, 1.15) * mm, "end": v(11.05, -1.15) * mm});
            skLineSegment(sketch, "E86.206.10.0", {"start": v(10.45, 6.81) * mm, "end": v(8.45, 5.66) * mm});
            skLineSegment(sketch, "E86.209.10.0", {"start": v(10.45, -6.81) * mm, "end": v(8.45, -5.66) * mm});
            skLineSegment(sketch, "E86.212.10.0", {"start": v(10.75, -6.3) * mm, "end": v(8.75, -5.14) * mm});
            skLineSegment(sketch, "E86.215.10.0", {"start": v(5.85, 1.5) * mm, "end": v(5.85, -1.5) * mm});
            skLineSegment(sketch, "E86.218.10.0", {"start": v(8.15, 2.83) * mm, "end": v(5.85, 1.5) * mm});
            skLineSegment(sketch, "E86.221.10.0", {"start": v(10.75, 6.3) * mm, "end": v(8.75, 5.14) * mm});
            skLineSegment(sketch, "E86.224.10.0", {"start": v(5.85, -1.5) * mm, "end": v(8.15, -2.83) * mm});
            skLineSegment(sketch, "E86.227.10.0", {"start": v(8.45, -2.3) * mm, "end": v(6.45, -1.15) * mm});
            skLineSegment(sketch, "E86.230.10.0", {"start": v(9.75, 2.25) * mm, "end": v(10.75, 1.67) * mm});
            skLineSegment(sketch, "E86.233.10.0", {"start": v(8.75, 2.83) * mm, "end": v(10.75, 1.67) * mm});
            skLineSegment(sketch, "E86.236.10.0", {"start": v(6.45, 1.15) * mm, "end": v(6.45, -1.15) * mm});
            skLineSegment(sketch, "E86.239.10.0", {"start": v(10.45, -1.15) * mm, "end": v(10.45, 1.15) * mm});
            skLineSegment(sketch, "E86.242.10.0", {"start": v(11.05, 1.15) * mm, "end": v(11.05, -1.15) * mm});
            skLineSegment(sketch, "E86.245.10.0", {"start": v(10.45, -1.15) * mm, "end": v(8.45, -2.3) * mm});
            skLineSegment(sketch, "E86.248.10.0", {"start": v(6.45, 1.15) * mm, "end": v(8.45, 2.3) * mm});
            skLineSegment(sketch, "E86.251.10.0", {"start": v(10.75, -1.67) * mm, "end": v(8.75, -2.83) * mm});
            skLineSegment(sketch, "E86.254.10.0", {"start": v(10.75, 1.67) * mm, "end": v(8.75, 2.83) * mm});
            skLineSegment(sketch, "E86.257.10.0", {"start": v(10.45, 1.15) * mm, "end": v(10.45, -1.15) * mm});
            skLineSegment(sketch, "E86.260.10.0", {"start": v(6.45, -1.15) * mm, "end": v(8.45, -2.3) * mm});
            skLineSegment(sketch, "E86.263.10.0", {"start": v(8.45, 2.3) * mm, "end": v(10.45, 1.15) * mm});
            skLineSegment(sketch, "E86.266.10.0", {"start": v(8.45, -2.3) * mm, "end": v(10.45, -1.15) * mm});
            skLineSegment(sketch, "E86.269.10.0", {"start": v(8.75, -2.83) * mm, "end": v(10.75, -1.67) * mm});
            skLineSegment(sketch, "E86.272.10.0", {"start": v(6.45, 1.15) * mm, "end": v(8.45, 2.3) * mm});
            skLineSegment(sketch, "E86.275.10.0", {"start": v(10.45, -1.15) * mm, "end": v(10.45, 1.15) * mm});
            skLineSegment(sketch, "E86.278.10.0", {"start": v(6.45, -1.15) * mm, "end": v(8.45, -2.3) * mm});
            skLineSegment(sketch, "E86.281.10.0", {"start": v(10.45, 1.15) * mm, "end": v(8.45, 2.3) * mm});
            skLineSegment(sketch, "E86.284.10.0", {"start": v(8.45, -2.3) * mm, "end": v(10.45, -1.15) * mm});
            skLineSegment(sketch, "E86.287.10.0", {"start": v(8.75, -2.83) * mm, "end": v(10.75, -1.67) * mm});
            skLineSegment(sketch, "E86.290.10.0", {"start": v(8.45, 2.3) * mm, "end": v(6.45, 1.15) * mm});
            skLineSegment(sketch, "E86.293.10.0", {"start": v(8.45, 2.3) * mm, "end": v(10.45, 1.15) * mm});
            skPoint(sketch, "E86.0.11.0", {"position": v(15.65, -1.5) * mm});
            skPoint(sketch, "E86.1.11.0", {"position": v(14.35, -5.72) * mm});
            skCircle(sketch, "E86.2.11.0", {"center": v(13.05, 0) * mm, "radius": 2 * mm, "construction": true});
            skPoint(sketch, "E86.4.11.0", {"position": v(13.05, 3) * mm});
            skPoint(sketch, "E86.5.11.0", {"position": v(14.05, -6.24) * mm});
            skPoint(sketch, "E86.6.11.0", {"position": v(15.65, 1.5) * mm});
            skCircle(sketch, "E86.7.11.0", {"center": v(13.05, 0) * mm, "radius": 2.6 * mm, "construction": true});
            skPoint(sketch, "E86.9.11.0", {"position": v(14.05, 6.24) * mm});
            skPoint(sketch, "E86.10.11.0", {"position": v(13.05, -3) * mm});
            skCircle(sketch, "E86.11.11.0", {"center": v(13.05, -7.97) * mm, "radius": 2.6 * mm, "construction": true});
            skPoint(sketch, "E86.13.11.0", {"position": v(14.35, 5.72) * mm});
            skCircle(sketch, "E86.14.11.0", {"center": v(15.35, -3.98) * mm, "radius": 2.6 * mm, "construction": true});
            skCircle(sketch, "E86.16.11.0", {"center": v(15.35, 3.98) * mm, "radius": 2.6 * mm, "construction": true});
            skCircle(sketch, "E86.18.11.0", {"center": v(13.05, 7.97) * mm, "radius": 2 * mm, "construction": true});
            skCircle(sketch, "E86.20.11.0", {"center": v(15.35, -3.98) * mm, "radius": 2 * mm, "construction": true});
            skLineSegment(sketch, "E86.22.11.0", {"start": v(14.58, 9.25) * mm, "end": v(10.45, 9.25) * mm});
            skPoint(sketch, "E86.25.11.0", {"position": v(10.45, 0) * mm});
            skCircle(sketch, "E86.26.11.0", {"center": v(13.05, 7.97) * mm, "radius": 2.6 * mm, "construction": true});
            skCircle(sketch, "E86.28.11.0", {"center": v(15.35, 3.98) * mm, "radius": 2 * mm, "construction": true});
            skCircle(sketch, "E86.30.11.0", {"center": v(13.05, -7.97) * mm, "radius": 2 * mm, "construction": true});
            skArc(sketch, "E86.32.11.0", {"start": v(11.75, -2.25) * mm, "mid": v(15.65, 0) * mm, "end": v(11.75, 2.25) * mm, "construction": true});
            skPoint(sketch, "E86.36.11.0", {"position": v(13.05, 3) * mm});
            skCircle(sketch, "E86.37.11.0", {"center": v(13.05, 0) * mm, "radius": 2 * mm, "construction": true});
            skPoint(sketch, "E86.39.11.0", {"position": v(15.65, 1.5) * mm});
            skLineSegment(sketch, "E86.40.11.0", {"start": v(10.45, 6.81) * mm, "end": v(10.45, 9.12) * mm});
            skLineSegment(sketch, "E86.43.11.0", {"start": v(12.75, 5.14) * mm, "end": v(10.45, 6.47) * mm});
            skLineSegment(sketch, "E86.46.11.0", {"start": v(11.05, 6.81) * mm, "end": v(11.05, 9.12) * mm});
            skLineSegment(sketch, "E86.49.11.0", {"start": v(17.95, 5.48) * mm, "end": v(15.65, 6.81) * mm});
            skLineSegment(sketch, "E86.52.11.0", {"start": v(17.95, 2.48) * mm, "end": v(17.95, 5.48) * mm});
            skLineSegment(sketch, "E86.55.11.0", {"start": v(17.95, -2.48) * mm, "end": v(17.95, -5.48) * mm});
            skLineSegment(sketch, "E86.58.11.0", {"start": v(10.45, -6.47) * mm, "end": v(10.45, -9.25) * mm});
            skLineSegment(sketch, "E86.61.11.0", {"start": v(17.95, -5.48) * mm, "end": v(15.65, -6.81) * mm});
            skPoint(sketch, "E86.64.11.0", {"position": v(14.35, -5.72) * mm});
            skLineSegment(sketch, "E86.65.11.0", {"start": v(11.05, -6.81) * mm, "end": v(11.05, -9.12) * mm});
            skPoint(sketch, "E86.68.11.0", {"position": v(14.35, 5.72) * mm});
            skLineSegment(sketch, "E86.69.11.0", {"start": v(17.35, -2.83) * mm, "end": v(17.35, -5.14) * mm});
            skLineSegment(sketch, "E86.72.11.0", {"start": v(17.35, 2.83) * mm, "end": v(17.35, 5.14) * mm});
            skPoint(sketch, "E86.75.11.0", {"position": v(14.05, 6.24) * mm});
            skLineSegment(sketch, "E86.76.11.0", {"start": v(12.75, -5.14) * mm, "end": v(10.45, -6.47) * mm});
            skPoint(sketch, "E86.79.11.0", {"position": v(11.05, 0) * mm});
            skLineSegment(sketch, "E86.80.11.0", {"start": v(15.65, 9.25) * mm, "end": v(15.65, 6.81) * mm});
            skLineSegment(sketch, "E86.83.11.0", {"start": v(15.65, -9.25) * mm, "end": v(15.65, -6.81) * mm});
            skPoint(sketch, "E86.86.11.0", {"position": v(10.45, 0) * mm});
            skPoint(sketch, "E86.87.11.0", {"position": v(14.05, -6.24) * mm});
            skPoint(sketch, "E86.88.11.0", {"position": v(13.05, -3) * mm});
            skLineSegment(sketch, "E86.89.11.0", {"start": v(15.05, -9.12) * mm, "end": v(15.05, -6.81) * mm});
            skLineSegment(sketch, "E86.92.11.0", {"start": v(15.05, 9.12) * mm, "end": v(15.05, 6.81) * mm});
            skPoint(sketch, "E86.95.11.0", {"position": v(15.65, -1.5) * mm});
            skLineSegment(sketch, "E86.96.11.0", {"start": v(10.45, 1.5) * mm, "end": v(12.75, 2.83) * mm});
            skLineSegment(sketch, "E86.99.11.0", {"start": v(13.35, 5.14) * mm, "end": v(13.35, 2.83) * mm});
            skLineSegment(sketch, "E86.102.11.0", {"start": v(15.35, 1.67) * mm, "end": v(17.35, 2.83) * mm});
            skLineSegment(sketch, "E86.105.11.0", {"start": v(13.05, -5.66) * mm, "end": v(11.05, -6.81) * mm});
            skLineSegment(sketch, "E86.108.11.0", {"start": v(12.75, 5.14) * mm, "end": v(12.75, 2.83) * mm});
            skLineSegment(sketch, "E86.111.11.0", {"start": v(13.35, -5.14) * mm, "end": v(13.35, -2.83) * mm});
            skLineSegment(sketch, "E86.114.11.0", {"start": v(15.65, -1.15) * mm, "end": v(17.95, -2.48) * mm});
            skLineSegment(sketch, "E86.117.11.0", {"start": v(15.65, -1.15) * mm, "end": v(15.65, 1.15) * mm});
            skLineSegment(sketch, "E86.120.11.0", {"start": v(15.65, -9.25) * mm, "end": v(14.83, -9.25) * mm});
            skLineSegment(sketch, "E86.123.11.0", {"start": v(15.35, -1.67) * mm, "end": v(17.35, -2.83) * mm});
            skLineSegment(sketch, "E86.126.11.0", {"start": v(17.35, -5.14) * mm, "end": v(15.35, -6.3) * mm});
            skCircle(sketch, "E86.129.11.0", {"center": v(13.05, 0) * mm, "radius": 2 * mm, "construction": true});
            skLineSegment(sketch, "E86.131.11.0", {"start": v(11.05, -9.12) * mm, "end": v(11.27, -9.25) * mm});
            skLineSegment(sketch, "E86.134.11.0", {"start": v(17.35, 5.14) * mm, "end": v(15.35, 6.3) * mm});
            skLineSegment(sketch, "E86.137.11.0", {"start": v(12.75, -2.83) * mm, "end": v(10.45, -1.5) * mm});
            skLineSegment(sketch, "E86.140.11.0", {"start": v(10.45, 6.47) * mm, "end": v(10.45, 9.25) * mm});
            skPoint(sketch, "E86.143.11.0", {"position": v(11.05, 0) * mm});
            skLineSegment(sketch, "E86.144.11.0", {"start": v(12.75, -5.14) * mm, "end": v(12.75, -2.83) * mm});
            skLineSegment(sketch, "E86.147.11.0", {"start": v(10.45, -6.81) * mm, "end": v(10.45, -9.12) * mm});
            skLineSegment(sketch, "E86.150.11.0", {"start": v(15.65, 1.15) * mm, "end": v(17.95, 2.48) * mm});
            skLineSegment(sketch, "E86.153.11.0", {"start": v(13.05, 5.66) * mm, "end": v(11.05, 6.81) * mm});
            skLineSegment(sketch, "E86.156.11.0", {"start": v(10.45, -1.5) * mm, "end": v(10.45, 0) * mm});
            skLineSegment(sketch, "E86.159.11.0", {"start": v(14.83, 9.25) * mm, "end": v(15.05, 9.12) * mm});
            skLineSegment(sketch, "E86.162.11.0", {"start": v(11.05, 9.12) * mm, "end": v(11.27, 9.25) * mm});
            skLineSegment(sketch, "E86.165.11.0", {"start": v(15.65, -1.15) * mm, "end": v(15.65, 1.15) * mm});
            skLineSegment(sketch, "E86.168.11.0", {"start": v(10.45, 1.5) * mm, "end": v(12.75, 2.83) * mm});
            skLineSegment(sketch, "E86.171.11.0", {"start": v(15.35, -6.3) * mm, "end": v(13.35, -5.14) * mm});
            skLineSegment(sketch, "E86.174.11.0", {"start": v(14.83, -9.25) * mm, "end": v(15.05, -9.12) * mm});
            skLineSegment(sketch, "E86.177.11.0", {"start": v(15.05, 6.81) * mm, "end": v(13.05, 5.66) * mm});
            skLineSegment(sketch, "E86.180.11.0", {"start": v(15.05, -6.81) * mm, "end": v(13.05, -5.66) * mm});
            skLineSegment(sketch, "E86.183.11.0", {"start": v(11.27, -9.25) * mm, "end": v(10.45, -9.25) * mm});
            skLineSegment(sketch, "E86.186.11.0", {"start": v(15.35, 6.3) * mm, "end": v(13.35, 5.14) * mm});
            skCircle(sketch, "E86.189.11.0", {"center": v(13.05, 0) * mm, "radius": 2 * mm, "construction": true});
            skLineSegment(sketch, "E86.191.11.0", {"start": v(15.65, 9.25) * mm, "end": v(14.83, 9.25) * mm});
            skLineSegment(sketch, "E86.194.11.0", {"start": v(10.45, -1.5) * mm, "end": v(12.75, -2.83) * mm});
            skLineSegment(sketch, "E86.197.11.0", {"start": v(15.05, 1.15) * mm, "end": v(15.05, -1.15) * mm});
            skLineSegment(sketch, "E86.200.11.0", {"start": v(11.05, -1.15) * mm, "end": v(11.05, 1.15) * mm});
            skLineSegment(sketch, "E86.203.11.0", {"start": v(15.65, 1.15) * mm, "end": v(15.65, -1.15) * mm});
            skLineSegment(sketch, "E86.206.11.0", {"start": v(15.05, 6.81) * mm, "end": v(13.05, 5.66) * mm});
            skLineSegment(sketch, "E86.209.11.0", {"start": v(15.05, -6.81) * mm, "end": v(13.05, -5.66) * mm});
            skLineSegment(sketch, "E86.212.11.0", {"start": v(15.35, -6.3) * mm, "end": v(13.35, -5.14) * mm});
            skLineSegment(sketch, "E86.215.11.0", {"start": v(10.45, 1.5) * mm, "end": v(10.45, -1.5) * mm});
            skLineSegment(sketch, "E86.218.11.0", {"start": v(12.75, 2.83) * mm, "end": v(10.45, 1.5) * mm});
            skLineSegment(sketch, "E86.221.11.0", {"start": v(15.35, 6.3) * mm, "end": v(13.35, 5.14) * mm});
            skLineSegment(sketch, "E86.224.11.0", {"start": v(10.45, -1.5) * mm, "end": v(12.75, -2.83) * mm});
            skLineSegment(sketch, "E86.227.11.0", {"start": v(13.05, -2.3) * mm, "end": v(11.05, -1.15) * mm});
            skLineSegment(sketch, "E86.230.11.0", {"start": v(14.35, 2.25) * mm, "end": v(15.35, 1.67) * mm});
            skLineSegment(sketch, "E86.233.11.0", {"start": v(13.35, 2.83) * mm, "end": v(15.35, 1.67) * mm});
            skLineSegment(sketch, "E86.236.11.0", {"start": v(11.05, 1.15) * mm, "end": v(11.05, -1.15) * mm});
            skLineSegment(sketch, "E86.239.11.0", {"start": v(15.05, -1.15) * mm, "end": v(15.05, 1.15) * mm});
            skLineSegment(sketch, "E86.242.11.0", {"start": v(15.65, 1.15) * mm, "end": v(15.65, -1.15) * mm});
            skLineSegment(sketch, "E86.245.11.0", {"start": v(15.05, -1.15) * mm, "end": v(13.05, -2.3) * mm});
            skLineSegment(sketch, "E86.248.11.0", {"start": v(11.05, 1.15) * mm, "end": v(13.05, 2.3) * mm});
            skLineSegment(sketch, "E86.251.11.0", {"start": v(15.35, -1.67) * mm, "end": v(13.35, -2.83) * mm});
            skLineSegment(sketch, "E86.254.11.0", {"start": v(15.35, 1.67) * mm, "end": v(13.35, 2.83) * mm});
            skLineSegment(sketch, "E86.257.11.0", {"start": v(15.05, 1.15) * mm, "end": v(15.05, -1.15) * mm});
            skLineSegment(sketch, "E86.260.11.0", {"start": v(11.05, -1.15) * mm, "end": v(13.05, -2.3) * mm});
            skLineSegment(sketch, "E86.263.11.0", {"start": v(13.05, 2.3) * mm, "end": v(15.05, 1.15) * mm});
            skLineSegment(sketch, "E86.266.11.0", {"start": v(13.05, -2.3) * mm, "end": v(15.05, -1.15) * mm});
            skLineSegment(sketch, "E86.269.11.0", {"start": v(13.35, -2.83) * mm, "end": v(15.35, -1.67) * mm});
            skLineSegment(sketch, "E86.272.11.0", {"start": v(11.05, 1.15) * mm, "end": v(13.05, 2.3) * mm});
            skLineSegment(sketch, "E86.275.11.0", {"start": v(15.05, -1.15) * mm, "end": v(15.05, 1.15) * mm});
            skLineSegment(sketch, "E86.278.11.0", {"start": v(11.05, -1.15) * mm, "end": v(13.05, -2.3) * mm});
            skLineSegment(sketch, "E86.281.11.0", {"start": v(15.05, 1.15) * mm, "end": v(13.05, 2.3) * mm});
            skLineSegment(sketch, "E86.284.11.0", {"start": v(13.05, -2.3) * mm, "end": v(15.05, -1.15) * mm});
            skLineSegment(sketch, "E86.287.11.0", {"start": v(13.35, -2.83) * mm, "end": v(15.35, -1.67) * mm});
            skLineSegment(sketch, "E86.290.11.0", {"start": v(13.05, 2.3) * mm, "end": v(11.05, 1.15) * mm});
            skLineSegment(sketch, "E86.293.11.0", {"start": v(13.05, 2.3) * mm, "end": v(15.05, 1.15) * mm});
            skPoint(sketch, "E86.0.12.0", {"position": v(20.25, -1.5) * mm});
            skPoint(sketch, "E86.1.12.0", {"position": v(18.95, -5.72) * mm});
            skCircle(sketch, "E86.2.12.0", {"center": v(17.65, 0) * mm, "radius": 2 * mm, "construction": true});
            skPoint(sketch, "E86.4.12.0", {"position": v(17.65, 3) * mm});
            skPoint(sketch, "E86.5.12.0", {"position": v(18.65, -6.24) * mm});
            skPoint(sketch, "E86.6.12.0", {"position": v(20.25, 1.5) * mm});
            skCircle(sketch, "E86.7.12.0", {"center": v(17.65, 0) * mm, "radius": 2.6 * mm, "construction": true});
            skPoint(sketch, "E86.9.12.0", {"position": v(18.65, 6.24) * mm});
            skPoint(sketch, "E86.10.12.0", {"position": v(17.65, -3) * mm});
            skCircle(sketch, "E86.11.12.0", {"center": v(17.65, -7.97) * mm, "radius": 2.6 * mm, "construction": true});
            skPoint(sketch, "E86.13.12.0", {"position": v(18.95, 5.72) * mm});
            skCircle(sketch, "E86.14.12.0", {"center": v(19.95, -3.98) * mm, "radius": 2.6 * mm, "construction": true});
            skCircle(sketch, "E86.16.12.0", {"center": v(19.95, 3.98) * mm, "radius": 2.6 * mm, "construction": true});
            skCircle(sketch, "E86.18.12.0", {"center": v(17.65, 7.97) * mm, "radius": 2 * mm, "construction": true});
            skCircle(sketch, "E86.20.12.0", {"center": v(19.95, -3.98) * mm, "radius": 2 * mm, "construction": true});
            skLineSegment(sketch, "E86.22.12.0", {"start": v(19.18, 9.25) * mm, "end": v(15.05, 9.25) * mm});
            skPoint(sketch, "E86.25.12.0", {"position": v(15.05, 0) * mm});
            skCircle(sketch, "E86.26.12.0", {"center": v(17.65, 7.97) * mm, "radius": 2.6 * mm, "construction": true});
            skCircle(sketch, "E86.28.12.0", {"center": v(19.95, 3.98) * mm, "radius": 2 * mm, "construction": true});
            skCircle(sketch, "E86.30.12.0", {"center": v(17.65, -7.97) * mm, "radius": 2 * mm, "construction": true});
            skArc(sketch, "E86.32.12.0", {"start": v(16.35, -2.25) * mm, "mid": v(20.25, 0) * mm, "end": v(16.35, 2.25) * mm, "construction": true});
            skPoint(sketch, "E86.36.12.0", {"position": v(17.65, 3) * mm});
            skCircle(sketch, "E86.37.12.0", {"center": v(17.65, 0) * mm, "radius": 2 * mm, "construction": true});
            skPoint(sketch, "E86.39.12.0", {"position": v(20.25, 1.5) * mm});
            skLineSegment(sketch, "E86.40.12.0", {"start": v(15.05, 6.81) * mm, "end": v(15.05, 9.12) * mm});
            skLineSegment(sketch, "E86.43.12.0", {"start": v(17.35, 5.14) * mm, "end": v(15.05, 6.47) * mm});
            skLineSegment(sketch, "E86.46.12.0", {"start": v(15.65, 6.81) * mm, "end": v(15.65, 9.12) * mm});
            skLineSegment(sketch, "E86.49.12.0", {"start": v(22.55, 5.48) * mm, "end": v(20.25, 6.81) * mm});
            skLineSegment(sketch, "E86.52.12.0", {"start": v(22.55, 2.48) * mm, "end": v(22.55, 5.48) * mm});
            skLineSegment(sketch, "E86.55.12.0", {"start": v(22.55, -2.48) * mm, "end": v(22.55, -5.48) * mm});
            skLineSegment(sketch, "E86.58.12.0", {"start": v(15.05, -6.47) * mm, "end": v(15.05, -9.25) * mm});
            skLineSegment(sketch, "E86.61.12.0", {"start": v(22.55, -5.48) * mm, "end": v(20.25, -6.81) * mm});
            skPoint(sketch, "E86.64.12.0", {"position": v(18.95, -5.72) * mm});
            skLineSegment(sketch, "E86.65.12.0", {"start": v(15.65, -6.81) * mm, "end": v(15.65, -9.12) * mm});
            skPoint(sketch, "E86.68.12.0", {"position": v(18.95, 5.72) * mm});
            skLineSegment(sketch, "E86.69.12.0", {"start": v(21.95, -2.83) * mm, "end": v(21.95, -5.14) * mm});
            skLineSegment(sketch, "E86.72.12.0", {"start": v(21.95, 2.83) * mm, "end": v(21.95, 5.14) * mm});
            skPoint(sketch, "E86.75.12.0", {"position": v(18.65, 6.24) * mm});
            skLineSegment(sketch, "E86.76.12.0", {"start": v(17.35, -5.14) * mm, "end": v(15.05, -6.47) * mm});
            skPoint(sketch, "E86.79.12.0", {"position": v(15.65, 0) * mm});
            skLineSegment(sketch, "E86.80.12.0", {"start": v(20.25, 9.25) * mm, "end": v(20.25, 6.81) * mm});
            skLineSegment(sketch, "E86.83.12.0", {"start": v(20.25, -9.25) * mm, "end": v(20.25, -6.81) * mm});
            skPoint(sketch, "E86.86.12.0", {"position": v(15.05, 0) * mm});
            skPoint(sketch, "E86.87.12.0", {"position": v(18.65, -6.24) * mm});
            skPoint(sketch, "E86.88.12.0", {"position": v(17.65, -3) * mm});
            skLineSegment(sketch, "E86.89.12.0", {"start": v(19.65, -9.12) * mm, "end": v(19.65, -6.81) * mm});
            skLineSegment(sketch, "E86.92.12.0", {"start": v(19.65, 9.12) * mm, "end": v(19.65, 6.81) * mm});
            skPoint(sketch, "E86.95.12.0", {"position": v(20.25, -1.5) * mm});
            skLineSegment(sketch, "E86.96.12.0", {"start": v(15.05, 1.5) * mm, "end": v(17.35, 2.83) * mm});
            skLineSegment(sketch, "E86.99.12.0", {"start": v(17.95, 5.14) * mm, "end": v(17.95, 2.83) * mm});
            skLineSegment(sketch, "E86.102.12.0", {"start": v(19.95, 1.67) * mm, "end": v(21.95, 2.83) * mm});
            skLineSegment(sketch, "E86.105.12.0", {"start": v(17.65, -5.66) * mm, "end": v(15.65, -6.81) * mm});
            skLineSegment(sketch, "E86.108.12.0", {"start": v(17.35, 5.14) * mm, "end": v(17.35, 2.83) * mm});
            skLineSegment(sketch, "E86.111.12.0", {"start": v(17.95, -5.14) * mm, "end": v(17.95, -2.83) * mm});
            skLineSegment(sketch, "E86.114.12.0", {"start": v(20.25, -1.15) * mm, "end": v(22.55, -2.48) * mm});
            skLineSegment(sketch, "E86.117.12.0", {"start": v(20.25, -1.15) * mm, "end": v(20.25, 1.15) * mm});
            skLineSegment(sketch, "E86.120.12.0", {"start": v(20.25, -9.25) * mm, "end": v(19.43, -9.25) * mm});
            skLineSegment(sketch, "E86.123.12.0", {"start": v(19.95, -1.67) * mm, "end": v(21.95, -2.83) * mm});
            skLineSegment(sketch, "E86.126.12.0", {"start": v(21.95, -5.14) * mm, "end": v(19.95, -6.3) * mm});
            skCircle(sketch, "E86.129.12.0", {"center": v(17.65, 0) * mm, "radius": 2 * mm, "construction": true});
            skLineSegment(sketch, "E86.131.12.0", {"start": v(15.65, -9.12) * mm, "end": v(15.87, -9.25) * mm});
            skLineSegment(sketch, "E86.134.12.0", {"start": v(21.95, 5.14) * mm, "end": v(19.95, 6.3) * mm});
            skLineSegment(sketch, "E86.137.12.0", {"start": v(17.35, -2.83) * mm, "end": v(15.05, -1.5) * mm});
            skLineSegment(sketch, "E86.140.12.0", {"start": v(15.05, 6.47) * mm, "end": v(15.05, 9.25) * mm});
            skPoint(sketch, "E86.143.12.0", {"position": v(15.65, 0) * mm});
            skLineSegment(sketch, "E86.144.12.0", {"start": v(17.35, -5.14) * mm, "end": v(17.35, -2.83) * mm});
            skLineSegment(sketch, "E86.147.12.0", {"start": v(15.05, -6.81) * mm, "end": v(15.05, -9.12) * mm});
            skLineSegment(sketch, "E86.150.12.0", {"start": v(20.25, 1.15) * mm, "end": v(22.55, 2.48) * mm});
            skLineSegment(sketch, "E86.153.12.0", {"start": v(17.65, 5.66) * mm, "end": v(15.65, 6.81) * mm});
            skLineSegment(sketch, "E86.156.12.0", {"start": v(15.05, -1.5) * mm, "end": v(15.05, 0) * mm});
            skLineSegment(sketch, "E86.159.12.0", {"start": v(19.43, 9.25) * mm, "end": v(19.65, 9.12) * mm});
            skLineSegment(sketch, "E86.162.12.0", {"start": v(15.65, 9.12) * mm, "end": v(15.87, 9.25) * mm});
            skLineSegment(sketch, "E86.165.12.0", {"start": v(20.25, -1.15) * mm, "end": v(20.25, 1.15) * mm});
            skLineSegment(sketch, "E86.168.12.0", {"start": v(15.05, 1.5) * mm, "end": v(17.35, 2.83) * mm});
            skLineSegment(sketch, "E86.171.12.0", {"start": v(19.95, -6.3) * mm, "end": v(17.95, -5.14) * mm});
            skLineSegment(sketch, "E86.174.12.0", {"start": v(19.43, -9.25) * mm, "end": v(19.65, -9.12) * mm});
            skLineSegment(sketch, "E86.177.12.0", {"start": v(19.65, 6.81) * mm, "end": v(17.65, 5.66) * mm});
            skLineSegment(sketch, "E86.180.12.0", {"start": v(19.65, -6.81) * mm, "end": v(17.65, -5.66) * mm});
            skLineSegment(sketch, "E86.183.12.0", {"start": v(15.87, -9.25) * mm, "end": v(15.05, -9.25) * mm});
            skLineSegment(sketch, "E86.186.12.0", {"start": v(19.95, 6.3) * mm, "end": v(17.95, 5.14) * mm});
            skCircle(sketch, "E86.189.12.0", {"center": v(17.65, 0) * mm, "radius": 2 * mm, "construction": true});
            skLineSegment(sketch, "E86.191.12.0", {"start": v(20.25, 9.25) * mm, "end": v(19.43, 9.25) * mm});
            skLineSegment(sketch, "E86.194.12.0", {"start": v(15.05, -1.5) * mm, "end": v(17.35, -2.83) * mm});
            skLineSegment(sketch, "E86.197.12.0", {"start": v(19.65, 1.15) * mm, "end": v(19.65, -1.15) * mm});
            skLineSegment(sketch, "E86.200.12.0", {"start": v(15.65, -1.15) * mm, "end": v(15.65, 1.15) * mm});
            skLineSegment(sketch, "E86.203.12.0", {"start": v(20.25, 1.15) * mm, "end": v(20.25, -1.15) * mm});
            skLineSegment(sketch, "E86.206.12.0", {"start": v(19.65, 6.81) * mm, "end": v(17.65, 5.66) * mm});
            skLineSegment(sketch, "E86.209.12.0", {"start": v(19.65, -6.81) * mm, "end": v(17.65, -5.66) * mm});
            skLineSegment(sketch, "E86.212.12.0", {"start": v(19.95, -6.3) * mm, "end": v(17.95, -5.14) * mm});
            skLineSegment(sketch, "E86.215.12.0", {"start": v(15.05, 1.5) * mm, "end": v(15.05, -1.5) * mm});
            skLineSegment(sketch, "E86.218.12.0", {"start": v(17.35, 2.83) * mm, "end": v(15.05, 1.5) * mm});
            skLineSegment(sketch, "E86.221.12.0", {"start": v(19.95, 6.3) * mm, "end": v(17.95, 5.14) * mm});
            skLineSegment(sketch, "E86.224.12.0", {"start": v(15.05, -1.5) * mm, "end": v(17.35, -2.83) * mm});
            skLineSegment(sketch, "E86.227.12.0", {"start": v(17.65, -2.3) * mm, "end": v(15.65, -1.15) * mm});
            skLineSegment(sketch, "E86.230.12.0", {"start": v(18.95, 2.25) * mm, "end": v(19.95, 1.67) * mm});
            skLineSegment(sketch, "E86.233.12.0", {"start": v(17.95, 2.83) * mm, "end": v(19.95, 1.67) * mm});
            skLineSegment(sketch, "E86.236.12.0", {"start": v(15.65, 1.15) * mm, "end": v(15.65, -1.15) * mm});
            skLineSegment(sketch, "E86.239.12.0", {"start": v(19.65, -1.15) * mm, "end": v(19.65, 1.15) * mm});
            skLineSegment(sketch, "E86.242.12.0", {"start": v(20.25, 1.15) * mm, "end": v(20.25, -1.15) * mm});
            skLineSegment(sketch, "E86.245.12.0", {"start": v(19.65, -1.15) * mm, "end": v(17.65, -2.3) * mm});
            skLineSegment(sketch, "E86.248.12.0", {"start": v(15.65, 1.15) * mm, "end": v(17.65, 2.3) * mm});
            skLineSegment(sketch, "E86.251.12.0", {"start": v(19.95, -1.67) * mm, "end": v(17.95, -2.83) * mm});
            skLineSegment(sketch, "E86.254.12.0", {"start": v(19.95, 1.67) * mm, "end": v(17.95, 2.83) * mm});
            skLineSegment(sketch, "E86.257.12.0", {"start": v(19.65, 1.15) * mm, "end": v(19.65, -1.15) * mm});
            skLineSegment(sketch, "E86.260.12.0", {"start": v(15.65, -1.15) * mm, "end": v(17.65, -2.3) * mm});
            skLineSegment(sketch, "E86.263.12.0", {"start": v(17.65, 2.3) * mm, "end": v(19.65, 1.15) * mm});
            skLineSegment(sketch, "E86.266.12.0", {"start": v(17.65, -2.3) * mm, "end": v(19.65, -1.15) * mm});
            skLineSegment(sketch, "E86.269.12.0", {"start": v(17.95, -2.83) * mm, "end": v(19.95, -1.67) * mm});
            skLineSegment(sketch, "E86.272.12.0", {"start": v(15.65, 1.15) * mm, "end": v(17.65, 2.3) * mm});
            skLineSegment(sketch, "E86.275.12.0", {"start": v(19.65, -1.15) * mm, "end": v(19.65, 1.15) * mm});
            skLineSegment(sketch, "E86.278.12.0", {"start": v(15.65, -1.15) * mm, "end": v(17.65, -2.3) * mm});
            skLineSegment(sketch, "E86.281.12.0", {"start": v(19.65, 1.15) * mm, "end": v(17.65, 2.3) * mm});
            skLineSegment(sketch, "E86.284.12.0", {"start": v(17.65, -2.3) * mm, "end": v(19.65, -1.15) * mm});
            skLineSegment(sketch, "E86.287.12.0", {"start": v(17.95, -2.83) * mm, "end": v(19.95, -1.67) * mm});
            skLineSegment(sketch, "E86.290.12.0", {"start": v(17.65, 2.3) * mm, "end": v(15.65, 1.15) * mm});
            skLineSegment(sketch, "E86.293.12.0", {"start": v(17.65, 2.3) * mm, "end": v(19.65, 1.15) * mm});
            skPoint(sketch, "E86.0.13.0", {"position": v(24.85, -1.5) * mm});
            skPoint(sketch, "E86.1.13.0", {"position": v(23.55, -5.72) * mm});
            skCircle(sketch, "E86.2.13.0", {"center": v(22.25, 0) * mm, "radius": 2 * mm, "construction": true});
            skPoint(sketch, "E86.4.13.0", {"position": v(22.25, 3) * mm});
            skPoint(sketch, "E86.5.13.0", {"position": v(23.25, -6.24) * mm});
            skPoint(sketch, "E86.6.13.0", {"position": v(24.85, 1.5) * mm});
            skCircle(sketch, "E86.7.13.0", {"center": v(22.25, 0) * mm, "radius": 2.6 * mm, "construction": true});
            skPoint(sketch, "E86.9.13.0", {"position": v(23.25, 6.24) * mm});
            skPoint(sketch, "E86.10.13.0", {"position": v(22.25, -3) * mm});
            skCircle(sketch, "E86.11.13.0", {"center": v(22.25, -7.97) * mm, "radius": 2.6 * mm, "construction": true});
            skPoint(sketch, "E86.13.13.0", {"position": v(23.55, 5.72) * mm});
            skCircle(sketch, "E86.14.13.0", {"center": v(24.55, -3.98) * mm, "radius": 2.6 * mm, "construction": true});
            skCircle(sketch, "E86.16.13.0", {"center": v(24.55, 3.98) * mm, "radius": 2.6 * mm, "construction": true});
            skCircle(sketch, "E86.18.13.0", {"center": v(22.25, 7.97) * mm, "radius": 2 * mm, "construction": true});
            skCircle(sketch, "E86.20.13.0", {"center": v(24.55, -3.98) * mm, "radius": 2 * mm, "construction": true});
            skLineSegment(sketch, "E86.22.13.0", {"start": v(23.78, 9.25) * mm, "end": v(19.65, 9.25) * mm});
            skPoint(sketch, "E86.25.13.0", {"position": v(19.65, 0) * mm});
            skCircle(sketch, "E86.26.13.0", {"center": v(22.25, 7.97) * mm, "radius": 2.6 * mm, "construction": true});
            skCircle(sketch, "E86.28.13.0", {"center": v(24.55, 3.98) * mm, "radius": 2 * mm, "construction": true});
            skCircle(sketch, "E86.30.13.0", {"center": v(22.25, -7.97) * mm, "radius": 2 * mm, "construction": true});
            skArc(sketch, "E86.32.13.0", {"start": v(20.95, -2.25) * mm, "mid": v(24.85, 0) * mm, "end": v(20.95, 2.25) * mm, "construction": true});
            skPoint(sketch, "E86.36.13.0", {"position": v(22.25, 3) * mm});
            skCircle(sketch, "E86.37.13.0", {"center": v(22.25, 0) * mm, "radius": 2 * mm, "construction": true});
            skPoint(sketch, "E86.39.13.0", {"position": v(24.85, 1.5) * mm});
            skLineSegment(sketch, "E86.40.13.0", {"start": v(19.65, 6.81) * mm, "end": v(19.65, 9.12) * mm});
            skLineSegment(sketch, "E86.43.13.0", {"start": v(21.95, 5.14) * mm, "end": v(19.65, 6.47) * mm});
            skLineSegment(sketch, "E86.46.13.0", {"start": v(20.25, 6.81) * mm, "end": v(20.25, 9.12) * mm});
            skLineSegment(sketch, "E86.49.13.0", {"start": v(27.15, 5.48) * mm, "end": v(24.85, 6.81) * mm});
            skLineSegment(sketch, "E86.52.13.0", {"start": v(27.15, 2.48) * mm, "end": v(27.15, 5.48) * mm});
            skLineSegment(sketch, "E86.55.13.0", {"start": v(27.15, -2.48) * mm, "end": v(27.15, -5.48) * mm});
            skLineSegment(sketch, "E86.58.13.0", {"start": v(19.65, -6.47) * mm, "end": v(19.65, -9.25) * mm});
            skLineSegment(sketch, "E86.61.13.0", {"start": v(27.15, -5.48) * mm, "end": v(24.85, -6.81) * mm});
            skPoint(sketch, "E86.64.13.0", {"position": v(23.55, -5.72) * mm});
            skLineSegment(sketch, "E86.65.13.0", {"start": v(20.25, -6.81) * mm, "end": v(20.25, -9.12) * mm});
            skPoint(sketch, "E86.68.13.0", {"position": v(23.55, 5.72) * mm});
            skLineSegment(sketch, "E86.69.13.0", {"start": v(26.55, -2.83) * mm, "end": v(26.55, -5.14) * mm});
            skLineSegment(sketch, "E86.72.13.0", {"start": v(26.55, 2.83) * mm, "end": v(26.55, 5.14) * mm});
            skPoint(sketch, "E86.75.13.0", {"position": v(23.25, 6.24) * mm});
            skLineSegment(sketch, "E86.76.13.0", {"start": v(21.95, -5.14) * mm, "end": v(19.65, -6.47) * mm});
            skPoint(sketch, "E86.79.13.0", {"position": v(20.25, 0) * mm});
            skLineSegment(sketch, "E86.80.13.0", {"start": v(24.85, 9.25) * mm, "end": v(24.85, 6.81) * mm});
            skLineSegment(sketch, "E86.83.13.0", {"start": v(24.85, -9.25) * mm, "end": v(24.85, -6.81) * mm});
            skPoint(sketch, "E86.86.13.0", {"position": v(19.65, 0) * mm});
            skPoint(sketch, "E86.87.13.0", {"position": v(23.25, -6.24) * mm});
            skPoint(sketch, "E86.88.13.0", {"position": v(22.25, -3) * mm});
            skLineSegment(sketch, "E86.89.13.0", {"start": v(24.25, -9.12) * mm, "end": v(24.25, -6.81) * mm});
            skLineSegment(sketch, "E86.92.13.0", {"start": v(24.25, 9.12) * mm, "end": v(24.25, 6.81) * mm});
            skPoint(sketch, "E86.95.13.0", {"position": v(24.85, -1.5) * mm});
            skLineSegment(sketch, "E86.96.13.0", {"start": v(19.65, 1.5) * mm, "end": v(21.95, 2.83) * mm});
            skLineSegment(sketch, "E86.99.13.0", {"start": v(22.55, 5.14) * mm, "end": v(22.55, 2.83) * mm});
            skLineSegment(sketch, "E86.102.13.0", {"start": v(24.55, 1.67) * mm, "end": v(26.55, 2.83) * mm});
            skLineSegment(sketch, "E86.105.13.0", {"start": v(22.25, -5.66) * mm, "end": v(20.25, -6.81) * mm});
            skLineSegment(sketch, "E86.108.13.0", {"start": v(21.95, 5.14) * mm, "end": v(21.95, 2.83) * mm});
            skLineSegment(sketch, "E86.111.13.0", {"start": v(22.55, -5.14) * mm, "end": v(22.55, -2.83) * mm});
            skLineSegment(sketch, "E86.114.13.0", {"start": v(24.85, -1.15) * mm, "end": v(27.15, -2.48) * mm});
            skLineSegment(sketch, "E86.117.13.0", {"start": v(24.85, -1.15) * mm, "end": v(24.85, 1.15) * mm});
            skLineSegment(sketch, "E86.120.13.0", {"start": v(24.85, -9.25) * mm, "end": v(24.03, -9.25) * mm});
            skLineSegment(sketch, "E86.123.13.0", {"start": v(24.55, -1.67) * mm, "end": v(26.55, -2.83) * mm});
            skLineSegment(sketch, "E86.126.13.0", {"start": v(26.55, -5.14) * mm, "end": v(24.55, -6.3) * mm});
            skCircle(sketch, "E86.129.13.0", {"center": v(22.25, 0) * mm, "radius": 2 * mm, "construction": true});
            skLineSegment(sketch, "E86.131.13.0", {"start": v(20.25, -9.12) * mm, "end": v(20.47, -9.25) * mm});
            skLineSegment(sketch, "E86.134.13.0", {"start": v(26.55, 5.14) * mm, "end": v(24.55, 6.3) * mm});
            skLineSegment(sketch, "E86.137.13.0", {"start": v(21.95, -2.83) * mm, "end": v(19.65, -1.5) * mm});
            skLineSegment(sketch, "E86.140.13.0", {"start": v(19.65, 6.47) * mm, "end": v(19.65, 9.25) * mm});
            skPoint(sketch, "E86.143.13.0", {"position": v(20.25, 0) * mm});
            skLineSegment(sketch, "E86.144.13.0", {"start": v(21.95, -5.14) * mm, "end": v(21.95, -2.83) * mm});
            skLineSegment(sketch, "E86.147.13.0", {"start": v(19.65, -6.81) * mm, "end": v(19.65, -9.12) * mm});
            skLineSegment(sketch, "E86.150.13.0", {"start": v(24.85, 1.15) * mm, "end": v(27.15, 2.48) * mm});
            skLineSegment(sketch, "E86.153.13.0", {"start": v(22.25, 5.66) * mm, "end": v(20.25, 6.81) * mm});
            skLineSegment(sketch, "E86.156.13.0", {"start": v(19.65, -1.5) * mm, "end": v(19.65, 0) * mm});
            skLineSegment(sketch, "E86.159.13.0", {"start": v(24.03, 9.25) * mm, "end": v(24.25, 9.12) * mm});
            skLineSegment(sketch, "E86.162.13.0", {"start": v(20.25, 9.12) * mm, "end": v(20.47, 9.25) * mm});
            skLineSegment(sketch, "E86.165.13.0", {"start": v(24.85, -1.15) * mm, "end": v(24.85, 1.15) * mm});
            skLineSegment(sketch, "E86.168.13.0", {"start": v(19.65, 1.5) * mm, "end": v(21.95, 2.83) * mm});
            skLineSegment(sketch, "E86.171.13.0", {"start": v(24.55, -6.3) * mm, "end": v(22.55, -5.14) * mm});
            skLineSegment(sketch, "E86.174.13.0", {"start": v(24.03, -9.25) * mm, "end": v(24.25, -9.12) * mm});
            skLineSegment(sketch, "E86.177.13.0", {"start": v(24.25, 6.81) * mm, "end": v(22.25, 5.66) * mm});
            skLineSegment(sketch, "E86.180.13.0", {"start": v(24.25, -6.81) * mm, "end": v(22.25, -5.66) * mm});
            skLineSegment(sketch, "E86.183.13.0", {"start": v(20.47, -9.25) * mm, "end": v(19.65, -9.25) * mm});
            skLineSegment(sketch, "E86.186.13.0", {"start": v(24.55, 6.3) * mm, "end": v(22.55, 5.14) * mm});
            skCircle(sketch, "E86.189.13.0", {"center": v(22.25, 0) * mm, "radius": 2 * mm, "construction": true});
            skLineSegment(sketch, "E86.191.13.0", {"start": v(24.85, 9.25) * mm, "end": v(24.03, 9.25) * mm});
            skLineSegment(sketch, "E86.194.13.0", {"start": v(19.65, -1.5) * mm, "end": v(21.95, -2.83) * mm});
            skLineSegment(sketch, "E86.197.13.0", {"start": v(24.25, 1.15) * mm, "end": v(24.25, -1.15) * mm});
            skLineSegment(sketch, "E86.200.13.0", {"start": v(20.25, -1.15) * mm, "end": v(20.25, 1.15) * mm});
            skLineSegment(sketch, "E86.203.13.0", {"start": v(24.85, 1.15) * mm, "end": v(24.85, -1.15) * mm});
            skLineSegment(sketch, "E86.206.13.0", {"start": v(24.25, 6.81) * mm, "end": v(22.25, 5.66) * mm});
            skLineSegment(sketch, "E86.209.13.0", {"start": v(24.25, -6.81) * mm, "end": v(22.25, -5.66) * mm});
            skLineSegment(sketch, "E86.212.13.0", {"start": v(24.55, -6.3) * mm, "end": v(22.55, -5.14) * mm});
            skLineSegment(sketch, "E86.215.13.0", {"start": v(19.65, 1.5) * mm, "end": v(19.65, -1.5) * mm});
            skLineSegment(sketch, "E86.218.13.0", {"start": v(21.95, 2.83) * mm, "end": v(19.65, 1.5) * mm});
            skLineSegment(sketch, "E86.221.13.0", {"start": v(24.55, 6.3) * mm, "end": v(22.55, 5.14) * mm});
            skLineSegment(sketch, "E86.224.13.0", {"start": v(19.65, -1.5) * mm, "end": v(21.95, -2.83) * mm});
            skLineSegment(sketch, "E86.227.13.0", {"start": v(22.25, -2.3) * mm, "end": v(20.25, -1.15) * mm});
            skLineSegment(sketch, "E86.230.13.0", {"start": v(23.55, 2.25) * mm, "end": v(24.55, 1.67) * mm});
            skLineSegment(sketch, "E86.233.13.0", {"start": v(22.55, 2.83) * mm, "end": v(24.55, 1.67) * mm});
            skLineSegment(sketch, "E86.236.13.0", {"start": v(20.25, 1.15) * mm, "end": v(20.25, -1.15) * mm});
            skLineSegment(sketch, "E86.239.13.0", {"start": v(24.25, -1.15) * mm, "end": v(24.25, 1.15) * mm});
            skLineSegment(sketch, "E86.242.13.0", {"start": v(24.85, 1.15) * mm, "end": v(24.85, -1.15) * mm});
            skLineSegment(sketch, "E86.245.13.0", {"start": v(24.25, -1.15) * mm, "end": v(22.25, -2.3) * mm});
            skLineSegment(sketch, "E86.248.13.0", {"start": v(20.25, 1.15) * mm, "end": v(22.25, 2.3) * mm});
            skLineSegment(sketch, "E86.251.13.0", {"start": v(24.55, -1.67) * mm, "end": v(22.55, -2.83) * mm});
            skLineSegment(sketch, "E86.254.13.0", {"start": v(24.55, 1.67) * mm, "end": v(22.55, 2.83) * mm});
            skLineSegment(sketch, "E86.257.13.0", {"start": v(24.25, 1.15) * mm, "end": v(24.25, -1.15) * mm});
            skLineSegment(sketch, "E86.260.13.0", {"start": v(20.25, -1.15) * mm, "end": v(22.25, -2.3) * mm});
            skLineSegment(sketch, "E86.263.13.0", {"start": v(22.25, 2.3) * mm, "end": v(24.25, 1.15) * mm});
            skLineSegment(sketch, "E86.266.13.0", {"start": v(22.25, -2.3) * mm, "end": v(24.25, -1.15) * mm});
            skLineSegment(sketch, "E86.269.13.0", {"start": v(22.55, -2.83) * mm, "end": v(24.55, -1.67) * mm});
            skLineSegment(sketch, "E86.272.13.0", {"start": v(20.25, 1.15) * mm, "end": v(22.25, 2.3) * mm});
            skLineSegment(sketch, "E86.275.13.0", {"start": v(24.25, -1.15) * mm, "end": v(24.25, 1.15) * mm});
            skLineSegment(sketch, "E86.278.13.0", {"start": v(20.25, -1.15) * mm, "end": v(22.25, -2.3) * mm});
            skLineSegment(sketch, "E86.281.13.0", {"start": v(24.25, 1.15) * mm, "end": v(22.25, 2.3) * mm});
            skLineSegment(sketch, "E86.284.13.0", {"start": v(22.25, -2.3) * mm, "end": v(24.25, -1.15) * mm});
            skLineSegment(sketch, "E86.287.13.0", {"start": v(22.55, -2.83) * mm, "end": v(24.55, -1.67) * mm});
            skLineSegment(sketch, "E86.290.13.0", {"start": v(22.25, 2.3) * mm, "end": v(20.25, 1.15) * mm});
            skLineSegment(sketch, "E86.293.13.0", {"start": v(22.25, 2.3) * mm, "end": v(24.25, 1.15) * mm});
            skPoint(sketch, "E86.0.14.0", {"position": v(29.45, -1.5) * mm});
            skPoint(sketch, "E86.1.14.0", {"position": v(28.15, -5.72) * mm});
            skCircle(sketch, "E86.2.14.0", {"center": v(26.85, 0) * mm, "radius": 2 * mm, "construction": true});
            skPoint(sketch, "E86.4.14.0", {"position": v(26.85, 3) * mm});
            skPoint(sketch, "E86.5.14.0", {"position": v(27.85, -6.24) * mm});
            skPoint(sketch, "E86.6.14.0", {"position": v(29.45, 1.5) * mm});
            skCircle(sketch, "E86.7.14.0", {"center": v(26.85, 0) * mm, "radius": 2.6 * mm, "construction": true});
            skPoint(sketch, "E86.9.14.0", {"position": v(27.85, 6.24) * mm});
            skPoint(sketch, "E86.10.14.0", {"position": v(26.85, -3) * mm});
            skCircle(sketch, "E86.11.14.0", {"center": v(26.85, -7.97) * mm, "radius": 2.6 * mm, "construction": true});
            skPoint(sketch, "E86.13.14.0", {"position": v(28.15, 5.72) * mm});
            skCircle(sketch, "E86.14.14.0", {"center": v(29.15, -3.98) * mm, "radius": 2.6 * mm, "construction": true});
            skCircle(sketch, "E86.16.14.0", {"center": v(29.15, 3.98) * mm, "radius": 2.6 * mm, "construction": true});
            skCircle(sketch, "E86.18.14.0", {"center": v(26.85, 7.97) * mm, "radius": 2 * mm, "construction": true});
            skCircle(sketch, "E86.20.14.0", {"center": v(29.15, -3.98) * mm, "radius": 2 * mm, "construction": true});
            skLineSegment(sketch, "E86.22.14.0", {"start": v(28.38, 9.25) * mm, "end": v(24.25, 9.25) * mm});
            skPoint(sketch, "E86.25.14.0", {"position": v(24.25, 0) * mm});
            skCircle(sketch, "E86.26.14.0", {"center": v(26.85, 7.97) * mm, "radius": 2.6 * mm, "construction": true});
            skCircle(sketch, "E86.28.14.0", {"center": v(29.15, 3.98) * mm, "radius": 2 * mm, "construction": true});
            skCircle(sketch, "E86.30.14.0", {"center": v(26.85, -7.97) * mm, "radius": 2 * mm, "construction": true});
            skArc(sketch, "E86.32.14.0", {"start": v(25.55, -2.25) * mm, "mid": v(29.45, 0) * mm, "end": v(25.55, 2.25) * mm, "construction": true});
            skPoint(sketch, "E86.36.14.0", {"position": v(26.85, 3) * mm});
            skCircle(sketch, "E86.37.14.0", {"center": v(26.85, 0) * mm, "radius": 2 * mm, "construction": true});
            skPoint(sketch, "E86.39.14.0", {"position": v(29.45, 1.5) * mm});
            skLineSegment(sketch, "E86.40.14.0", {"start": v(24.25, 6.81) * mm, "end": v(24.25, 9.12) * mm});
            skLineSegment(sketch, "E86.43.14.0", {"start": v(26.55, 5.14) * mm, "end": v(24.25, 6.47) * mm});
            skLineSegment(sketch, "E86.46.14.0", {"start": v(24.85, 6.81) * mm, "end": v(24.85, 9.12) * mm});
            skLineSegment(sketch, "E86.49.14.0", {"start": v(31.75, 5.48) * mm, "end": v(29.45, 6.81) * mm});
            skLineSegment(sketch, "E86.52.14.0", {"start": v(31.75, 2.48) * mm, "end": v(31.75, 5.48) * mm});
            skLineSegment(sketch, "E86.55.14.0", {"start": v(31.75, -2.48) * mm, "end": v(31.75, -5.48) * mm});
            skLineSegment(sketch, "E86.58.14.0", {"start": v(24.25, -6.47) * mm, "end": v(24.25, -9.25) * mm});
            skLineSegment(sketch, "E86.61.14.0", {"start": v(31.75, -5.48) * mm, "end": v(29.45, -6.81) * mm});
            skPoint(sketch, "E86.64.14.0", {"position": v(28.15, -5.72) * mm});
            skLineSegment(sketch, "E86.65.14.0", {"start": v(24.85, -6.81) * mm, "end": v(24.85, -9.12) * mm});
            skPoint(sketch, "E86.68.14.0", {"position": v(28.15, 5.72) * mm});
            skLineSegment(sketch, "E86.69.14.0", {"start": v(31.15, -2.83) * mm, "end": v(31.15, -5.14) * mm});
            skLineSegment(sketch, "E86.72.14.0", {"start": v(31.15, 2.83) * mm, "end": v(31.15, 5.14) * mm});
            skPoint(sketch, "E86.75.14.0", {"position": v(27.85, 6.24) * mm});
            skLineSegment(sketch, "E86.76.14.0", {"start": v(26.55, -5.14) * mm, "end": v(24.25, -6.47) * mm});
            skPoint(sketch, "E86.79.14.0", {"position": v(24.85, 0) * mm});
            skLineSegment(sketch, "E86.80.14.0", {"start": v(29.45, 9.25) * mm, "end": v(29.45, 6.81) * mm});
            skLineSegment(sketch, "E86.83.14.0", {"start": v(29.45, -9.25) * mm, "end": v(29.45, -6.81) * mm});
            skPoint(sketch, "E86.86.14.0", {"position": v(24.25, 0) * mm});
            skPoint(sketch, "E86.87.14.0", {"position": v(27.85, -6.24) * mm});
            skPoint(sketch, "E86.88.14.0", {"position": v(26.85, -3) * mm});
            skLineSegment(sketch, "E86.89.14.0", {"start": v(28.85, -9.12) * mm, "end": v(28.85, -6.81) * mm});
            skLineSegment(sketch, "E86.92.14.0", {"start": v(28.85, 9.12) * mm, "end": v(28.85, 6.81) * mm});
            skPoint(sketch, "E86.95.14.0", {"position": v(29.45, -1.5) * mm});
            skLineSegment(sketch, "E86.96.14.0", {"start": v(24.25, 1.5) * mm, "end": v(26.55, 2.83) * mm});
            skLineSegment(sketch, "E86.99.14.0", {"start": v(27.15, 5.14) * mm, "end": v(27.15, 2.83) * mm});
            skLineSegment(sketch, "E86.102.14.0", {"start": v(29.15, 1.67) * mm, "end": v(31.15, 2.83) * mm});
            skLineSegment(sketch, "E86.105.14.0", {"start": v(26.85, -5.66) * mm, "end": v(24.85, -6.81) * mm});
            skLineSegment(sketch, "E86.108.14.0", {"start": v(26.55, 5.14) * mm, "end": v(26.55, 2.83) * mm});
            skLineSegment(sketch, "E86.111.14.0", {"start": v(27.15, -5.14) * mm, "end": v(27.15, -2.83) * mm});
            skLineSegment(sketch, "E86.114.14.0", {"start": v(29.45, -1.15) * mm, "end": v(31.75, -2.48) * mm});
            skLineSegment(sketch, "E86.117.14.0", {"start": v(29.45, -1.15) * mm, "end": v(29.45, 1.15) * mm});
            skLineSegment(sketch, "E86.120.14.0", {"start": v(29.45, -9.25) * mm, "end": v(28.63, -9.25) * mm});
            skLineSegment(sketch, "E86.123.14.0", {"start": v(29.15, -1.67) * mm, "end": v(31.15, -2.83) * mm});
            skLineSegment(sketch, "E86.126.14.0", {"start": v(31.15, -5.14) * mm, "end": v(29.15, -6.3) * mm});
            skCircle(sketch, "E86.129.14.0", {"center": v(26.85, 0) * mm, "radius": 2 * mm, "construction": true});
            skLineSegment(sketch, "E86.131.14.0", {"start": v(24.85, -9.12) * mm, "end": v(25.07, -9.25) * mm});
            skLineSegment(sketch, "E86.134.14.0", {"start": v(31.15, 5.14) * mm, "end": v(29.15, 6.3) * mm});
            skLineSegment(sketch, "E86.137.14.0", {"start": v(26.55, -2.83) * mm, "end": v(24.25, -1.5) * mm});
            skLineSegment(sketch, "E86.140.14.0", {"start": v(24.25, 6.47) * mm, "end": v(24.25, 9.25) * mm});
            skPoint(sketch, "E86.143.14.0", {"position": v(24.85, 0) * mm});
            skLineSegment(sketch, "E86.144.14.0", {"start": v(26.55, -5.14) * mm, "end": v(26.55, -2.83) * mm});
            skLineSegment(sketch, "E86.147.14.0", {"start": v(24.25, -6.81) * mm, "end": v(24.25, -9.12) * mm});
            skLineSegment(sketch, "E86.150.14.0", {"start": v(29.45, 1.15) * mm, "end": v(31.75, 2.48) * mm});
            skLineSegment(sketch, "E86.153.14.0", {"start": v(26.85, 5.66) * mm, "end": v(24.85, 6.81) * mm});
            skLineSegment(sketch, "E86.156.14.0", {"start": v(24.25, -1.5) * mm, "end": v(24.25, 0) * mm});
            skLineSegment(sketch, "E86.159.14.0", {"start": v(28.63, 9.25) * mm, "end": v(28.85, 9.12) * mm});
            skLineSegment(sketch, "E86.162.14.0", {"start": v(24.85, 9.12) * mm, "end": v(25.07, 9.25) * mm});
            skLineSegment(sketch, "E86.165.14.0", {"start": v(29.45, -1.15) * mm, "end": v(29.45, 1.15) * mm});
            skLineSegment(sketch, "E86.168.14.0", {"start": v(24.25, 1.5) * mm, "end": v(26.55, 2.83) * mm});
            skLineSegment(sketch, "E86.171.14.0", {"start": v(29.15, -6.3) * mm, "end": v(27.15, -5.14) * mm});
            skLineSegment(sketch, "E86.174.14.0", {"start": v(28.63, -9.25) * mm, "end": v(28.85, -9.12) * mm});
            skLineSegment(sketch, "E86.177.14.0", {"start": v(28.85, 6.81) * mm, "end": v(26.85, 5.66) * mm});
            skLineSegment(sketch, "E86.180.14.0", {"start": v(28.85, -6.81) * mm, "end": v(26.85, -5.66) * mm});
            skLineSegment(sketch, "E86.183.14.0", {"start": v(25.07, -9.25) * mm, "end": v(24.25, -9.25) * mm});
            skLineSegment(sketch, "E86.186.14.0", {"start": v(29.15, 6.3) * mm, "end": v(27.15, 5.14) * mm});
            skCircle(sketch, "E86.189.14.0", {"center": v(26.85, 0) * mm, "radius": 2 * mm, "construction": true});
            skLineSegment(sketch, "E86.191.14.0", {"start": v(29.45, 9.25) * mm, "end": v(28.63, 9.25) * mm});
            skLineSegment(sketch, "E86.194.14.0", {"start": v(24.25, -1.5) * mm, "end": v(26.55, -2.83) * mm});
            skLineSegment(sketch, "E86.197.14.0", {"start": v(28.85, 1.15) * mm, "end": v(28.85, -1.15) * mm});
            skLineSegment(sketch, "E86.200.14.0", {"start": v(24.85, -1.15) * mm, "end": v(24.85, 1.15) * mm});
            skLineSegment(sketch, "E86.203.14.0", {"start": v(29.45, 1.15) * mm, "end": v(29.45, -1.15) * mm});
            skLineSegment(sketch, "E86.206.14.0", {"start": v(28.85, 6.81) * mm, "end": v(26.85, 5.66) * mm});
            skLineSegment(sketch, "E86.209.14.0", {"start": v(28.85, -6.81) * mm, "end": v(26.85, -5.66) * mm});
            skLineSegment(sketch, "E86.212.14.0", {"start": v(29.15, -6.3) * mm, "end": v(27.15, -5.14) * mm});
            skLineSegment(sketch, "E86.215.14.0", {"start": v(24.25, 1.5) * mm, "end": v(24.25, -1.5) * mm});
            skLineSegment(sketch, "E86.218.14.0", {"start": v(26.55, 2.83) * mm, "end": v(24.25, 1.5) * mm});
            skLineSegment(sketch, "E86.221.14.0", {"start": v(29.15, 6.3) * mm, "end": v(27.15, 5.14) * mm});
            skLineSegment(sketch, "E86.224.14.0", {"start": v(24.25, -1.5) * mm, "end": v(26.55, -2.83) * mm});
            skLineSegment(sketch, "E86.227.14.0", {"start": v(26.85, -2.3) * mm, "end": v(24.85, -1.15) * mm});
            skLineSegment(sketch, "E86.230.14.0", {"start": v(28.15, 2.25) * mm, "end": v(29.15, 1.67) * mm});
            skLineSegment(sketch, "E86.233.14.0", {"start": v(27.15, 2.83) * mm, "end": v(29.15, 1.67) * mm});
            skLineSegment(sketch, "E86.236.14.0", {"start": v(24.85, 1.15) * mm, "end": v(24.85, -1.15) * mm});
            skLineSegment(sketch, "E86.239.14.0", {"start": v(28.85, -1.15) * mm, "end": v(28.85, 1.15) * mm});
            skLineSegment(sketch, "E86.242.14.0", {"start": v(29.45, 1.15) * mm, "end": v(29.45, -1.15) * mm});
            skLineSegment(sketch, "E86.245.14.0", {"start": v(28.85, -1.15) * mm, "end": v(26.85, -2.3) * mm});
            skLineSegment(sketch, "E86.248.14.0", {"start": v(24.85, 1.15) * mm, "end": v(26.85, 2.3) * mm});
            skLineSegment(sketch, "E86.251.14.0", {"start": v(29.15, -1.67) * mm, "end": v(27.15, -2.83) * mm});
            skLineSegment(sketch, "E86.254.14.0", {"start": v(29.15, 1.67) * mm, "end": v(27.15, 2.83) * mm});
            skLineSegment(sketch, "E86.257.14.0", {"start": v(28.85, 1.15) * mm, "end": v(28.85, -1.15) * mm});
            skLineSegment(sketch, "E86.260.14.0", {"start": v(24.85, -1.15) * mm, "end": v(26.85, -2.3) * mm});
            skLineSegment(sketch, "E86.263.14.0", {"start": v(26.85, 2.3) * mm, "end": v(28.85, 1.15) * mm});
            skLineSegment(sketch, "E86.266.14.0", {"start": v(26.85, -2.3) * mm, "end": v(28.85, -1.15) * mm});
            skLineSegment(sketch, "E86.269.14.0", {"start": v(27.15, -2.83) * mm, "end": v(29.15, -1.67) * mm});
            skLineSegment(sketch, "E86.272.14.0", {"start": v(24.85, 1.15) * mm, "end": v(26.85, 2.3) * mm});
            skLineSegment(sketch, "E86.275.14.0", {"start": v(28.85, -1.15) * mm, "end": v(28.85, 1.15) * mm});
            skLineSegment(sketch, "E86.278.14.0", {"start": v(24.85, -1.15) * mm, "end": v(26.85, -2.3) * mm});
            skLineSegment(sketch, "E86.281.14.0", {"start": v(28.85, 1.15) * mm, "end": v(26.85, 2.3) * mm});
            skLineSegment(sketch, "E86.284.14.0", {"start": v(26.85, -2.3) * mm, "end": v(28.85, -1.15) * mm});
            skLineSegment(sketch, "E86.287.14.0", {"start": v(27.15, -2.83) * mm, "end": v(29.15, -1.67) * mm});
            skLineSegment(sketch, "E86.290.14.0", {"start": v(26.85, 2.3) * mm, "end": v(24.85, 1.15) * mm});
            skLineSegment(sketch, "E86.293.14.0", {"start": v(26.85, 2.3) * mm, "end": v(28.85, 1.15) * mm});
            skPoint(sketch, "E86.0.15.0", {"position": v(34.05, -1.5) * mm});
            skPoint(sketch, "E86.1.15.0", {"position": v(32.75, -5.72) * mm});
            skCircle(sketch, "E86.2.15.0", {"center": v(31.45, 0) * mm, "radius": 2 * mm, "construction": true});
            skPoint(sketch, "E86.4.15.0", {"position": v(31.45, 3) * mm});
            skPoint(sketch, "E86.5.15.0", {"position": v(32.45, -6.24) * mm});
            skPoint(sketch, "E86.6.15.0", {"position": v(34.05, 1.5) * mm});
            skCircle(sketch, "E86.7.15.0", {"center": v(31.45, 0) * mm, "radius": 2.6 * mm, "construction": true});
            skPoint(sketch, "E86.9.15.0", {"position": v(32.45, 6.24) * mm});
            skPoint(sketch, "E86.10.15.0", {"position": v(31.45, -3) * mm});
            skCircle(sketch, "E86.11.15.0", {"center": v(31.45, -7.97) * mm, "radius": 2.6 * mm, "construction": true});
            skPoint(sketch, "E86.13.15.0", {"position": v(32.75, 5.72) * mm});
            skCircle(sketch, "E86.14.15.0", {"center": v(33.75, -3.98) * mm, "radius": 2.6 * mm, "construction": true});
            skCircle(sketch, "E86.16.15.0", {"center": v(33.75, 3.98) * mm, "radius": 2.6 * mm, "construction": true});
            skCircle(sketch, "E86.18.15.0", {"center": v(31.45, 7.97) * mm, "radius": 2 * mm, "construction": true});
            skCircle(sketch, "E86.20.15.0", {"center": v(33.75, -3.98) * mm, "radius": 2 * mm, "construction": true});
            skLineSegment(sketch, "E86.22.15.0", {"start": v(32.98, 9.25) * mm, "end": v(28.85, 9.25) * mm});
            skPoint(sketch, "E86.25.15.0", {"position": v(28.85, 0) * mm});
            skCircle(sketch, "E86.26.15.0", {"center": v(31.45, 7.97) * mm, "radius": 2.6 * mm, "construction": true});
            skCircle(sketch, "E86.28.15.0", {"center": v(33.75, 3.98) * mm, "radius": 2 * mm, "construction": true});
            skCircle(sketch, "E86.30.15.0", {"center": v(31.45, -7.97) * mm, "radius": 2 * mm, "construction": true});
            skArc(sketch, "E86.32.15.0", {"start": v(30.15, -2.25) * mm, "mid": v(34.05, 0) * mm, "end": v(30.15, 2.25) * mm, "construction": true});
            skPoint(sketch, "E86.36.15.0", {"position": v(31.45, 3) * mm});
            skCircle(sketch, "E86.37.15.0", {"center": v(31.45, 0) * mm, "radius": 2 * mm, "construction": true});
            skPoint(sketch, "E86.39.15.0", {"position": v(34.05, 1.5) * mm});
            skLineSegment(sketch, "E86.40.15.0", {"start": v(28.85, 6.81) * mm, "end": v(28.85, 9.12) * mm});
            skLineSegment(sketch, "E86.43.15.0", {"start": v(31.15, 5.14) * mm, "end": v(28.85, 6.47) * mm});
            skLineSegment(sketch, "E86.46.15.0", {"start": v(29.45, 6.81) * mm, "end": v(29.45, 9.12) * mm});
            skLineSegment(sketch, "E86.49.15.0", {"start": v(36.35, 5.48) * mm, "end": v(34.05, 6.81) * mm});
            skLineSegment(sketch, "E86.52.15.0", {"start": v(36.35, 2.48) * mm, "end": v(36.35, 5.48) * mm});
            skLineSegment(sketch, "E86.55.15.0", {"start": v(36.35, -2.48) * mm, "end": v(36.35, -5.48) * mm});
            skLineSegment(sketch, "E86.58.15.0", {"start": v(28.85, -6.47) * mm, "end": v(28.85, -9.25) * mm});
            skLineSegment(sketch, "E86.61.15.0", {"start": v(36.35, -5.48) * mm, "end": v(34.05, -6.81) * mm});
            skPoint(sketch, "E86.64.15.0", {"position": v(32.75, -5.72) * mm});
            skLineSegment(sketch, "E86.65.15.0", {"start": v(29.45, -6.81) * mm, "end": v(29.45, -9.12) * mm});
            skPoint(sketch, "E86.68.15.0", {"position": v(32.75, 5.72) * mm});
            skLineSegment(sketch, "E86.69.15.0", {"start": v(35.75, -2.83) * mm, "end": v(35.75, -5.14) * mm});
            skLineSegment(sketch, "E86.72.15.0", {"start": v(35.75, 2.83) * mm, "end": v(35.75, 5.14) * mm});
            skPoint(sketch, "E86.75.15.0", {"position": v(32.45, 6.24) * mm});
            skLineSegment(sketch, "E86.76.15.0", {"start": v(31.15, -5.14) * mm, "end": v(28.85, -6.47) * mm});
            skPoint(sketch, "E86.79.15.0", {"position": v(29.45, 0) * mm});
            skLineSegment(sketch, "E86.80.15.0", {"start": v(34.05, 9.25) * mm, "end": v(34.05, 6.81) * mm});
            skLineSegment(sketch, "E86.83.15.0", {"start": v(34.05, -9.25) * mm, "end": v(34.05, -6.81) * mm});
            skPoint(sketch, "E86.86.15.0", {"position": v(28.85, 0) * mm});
            skPoint(sketch, "E86.87.15.0", {"position": v(32.45, -6.24) * mm});
            skPoint(sketch, "E86.88.15.0", {"position": v(31.45, -3) * mm});
            skLineSegment(sketch, "E86.89.15.0", {"start": v(33.45, -9.12) * mm, "end": v(33.45, -6.81) * mm});
            skLineSegment(sketch, "E86.92.15.0", {"start": v(33.45, 9.12) * mm, "end": v(33.45, 6.81) * mm});
            skPoint(sketch, "E86.95.15.0", {"position": v(34.05, -1.5) * mm});
            skLineSegment(sketch, "E86.96.15.0", {"start": v(28.85, 1.5) * mm, "end": v(31.15, 2.83) * mm});
            skLineSegment(sketch, "E86.99.15.0", {"start": v(31.75, 5.14) * mm, "end": v(31.75, 2.83) * mm});
            skLineSegment(sketch, "E86.102.15.0", {"start": v(33.75, 1.67) * mm, "end": v(35.75, 2.83) * mm});
            skLineSegment(sketch, "E86.105.15.0", {"start": v(31.45, -5.66) * mm, "end": v(29.45, -6.81) * mm});
            skLineSegment(sketch, "E86.108.15.0", {"start": v(31.15, 5.14) * mm, "end": v(31.15, 2.83) * mm});
            skLineSegment(sketch, "E86.111.15.0", {"start": v(31.75, -5.14) * mm, "end": v(31.75, -2.83) * mm});
            skLineSegment(sketch, "E86.114.15.0", {"start": v(34.05, -1.15) * mm, "end": v(36.35, -2.48) * mm});
            skLineSegment(sketch, "E86.117.15.0", {"start": v(34.05, -1.15) * mm, "end": v(34.05, 1.15) * mm});
            skLineSegment(sketch, "E86.120.15.0", {"start": v(34.05, -9.25) * mm, "end": v(33.23, -9.25) * mm});
            skLineSegment(sketch, "E86.123.15.0", {"start": v(33.75, -1.67) * mm, "end": v(35.75, -2.83) * mm});
            skLineSegment(sketch, "E86.126.15.0", {"start": v(35.75, -5.14) * mm, "end": v(33.75, -6.3) * mm});
            skCircle(sketch, "E86.129.15.0", {"center": v(31.45, 0) * mm, "radius": 2 * mm, "construction": true});
            skLineSegment(sketch, "E86.131.15.0", {"start": v(29.45, -9.12) * mm, "end": v(29.67, -9.25) * mm});
            skLineSegment(sketch, "E86.134.15.0", {"start": v(35.75, 5.14) * mm, "end": v(33.75, 6.3) * mm});
            skLineSegment(sketch, "E86.137.15.0", {"start": v(31.15, -2.83) * mm, "end": v(28.85, -1.5) * mm});
            skLineSegment(sketch, "E86.140.15.0", {"start": v(28.85, 6.47) * mm, "end": v(28.85, 9.25) * mm});
            skPoint(sketch, "E86.143.15.0", {"position": v(29.45, 0) * mm});
            skLineSegment(sketch, "E86.144.15.0", {"start": v(31.15, -5.14) * mm, "end": v(31.15, -2.83) * mm});
            skLineSegment(sketch, "E86.147.15.0", {"start": v(28.85, -6.81) * mm, "end": v(28.85, -9.12) * mm});
            skLineSegment(sketch, "E86.150.15.0", {"start": v(34.05, 1.15) * mm, "end": v(36.35, 2.48) * mm});
            skLineSegment(sketch, "E86.153.15.0", {"start": v(31.45, 5.66) * mm, "end": v(29.45, 6.81) * mm});
            skLineSegment(sketch, "E86.156.15.0", {"start": v(28.85, -1.5) * mm, "end": v(28.85, 0) * mm});
            skLineSegment(sketch, "E86.159.15.0", {"start": v(33.23, 9.25) * mm, "end": v(33.45, 9.12) * mm});
            skLineSegment(sketch, "E86.162.15.0", {"start": v(29.45, 9.12) * mm, "end": v(29.67, 9.25) * mm});
            skLineSegment(sketch, "E86.165.15.0", {"start": v(34.05, -1.15) * mm, "end": v(34.05, 1.15) * mm});
            skLineSegment(sketch, "E86.168.15.0", {"start": v(28.85, 1.5) * mm, "end": v(31.15, 2.83) * mm});
            skLineSegment(sketch, "E86.171.15.0", {"start": v(33.75, -6.3) * mm, "end": v(31.75, -5.14) * mm});
            skLineSegment(sketch, "E86.174.15.0", {"start": v(33.23, -9.25) * mm, "end": v(33.45, -9.12) * mm});
            skLineSegment(sketch, "E86.177.15.0", {"start": v(33.45, 6.81) * mm, "end": v(31.45, 5.66) * mm});
            skLineSegment(sketch, "E86.180.15.0", {"start": v(33.45, -6.81) * mm, "end": v(31.45, -5.66) * mm});
            skLineSegment(sketch, "E86.183.15.0", {"start": v(29.67, -9.25) * mm, "end": v(28.85, -9.25) * mm});
            skLineSegment(sketch, "E86.186.15.0", {"start": v(33.75, 6.3) * mm, "end": v(31.75, 5.14) * mm});
            skCircle(sketch, "E86.189.15.0", {"center": v(31.45, 0) * mm, "radius": 2 * mm, "construction": true});
            skLineSegment(sketch, "E86.191.15.0", {"start": v(34.05, 9.25) * mm, "end": v(33.23, 9.25) * mm});
            skLineSegment(sketch, "E86.194.15.0", {"start": v(28.85, -1.5) * mm, "end": v(31.15, -2.83) * mm});
            skLineSegment(sketch, "E86.197.15.0", {"start": v(33.45, 1.15) * mm, "end": v(33.45, -1.15) * mm});
            skLineSegment(sketch, "E86.200.15.0", {"start": v(29.45, -1.15) * mm, "end": v(29.45, 1.15) * mm});
            skLineSegment(sketch, "E86.203.15.0", {"start": v(34.05, 1.15) * mm, "end": v(34.05, -1.15) * mm});
            skLineSegment(sketch, "E86.206.15.0", {"start": v(33.45, 6.81) * mm, "end": v(31.45, 5.66) * mm});
            skLineSegment(sketch, "E86.209.15.0", {"start": v(33.45, -6.81) * mm, "end": v(31.45, -5.66) * mm});
            skLineSegment(sketch, "E86.212.15.0", {"start": v(33.75, -6.3) * mm, "end": v(31.75, -5.14) * mm});
            skLineSegment(sketch, "E86.215.15.0", {"start": v(28.85, 1.5) * mm, "end": v(28.85, -1.5) * mm});
            skLineSegment(sketch, "E86.218.15.0", {"start": v(31.15, 2.83) * mm, "end": v(28.85, 1.5) * mm});
            skLineSegment(sketch, "E86.221.15.0", {"start": v(33.75, 6.3) * mm, "end": v(31.75, 5.14) * mm});
            skLineSegment(sketch, "E86.224.15.0", {"start": v(28.85, -1.5) * mm, "end": v(31.15, -2.83) * mm});
            skLineSegment(sketch, "E86.227.15.0", {"start": v(31.45, -2.3) * mm, "end": v(29.45, -1.15) * mm});
            skLineSegment(sketch, "E86.230.15.0", {"start": v(32.75, 2.25) * mm, "end": v(33.75, 1.67) * mm});
            skLineSegment(sketch, "E86.233.15.0", {"start": v(31.75, 2.83) * mm, "end": v(33.75, 1.67) * mm});
            skLineSegment(sketch, "E86.236.15.0", {"start": v(29.45, 1.15) * mm, "end": v(29.45, -1.15) * mm});
            skLineSegment(sketch, "E86.239.15.0", {"start": v(33.45, -1.15) * mm, "end": v(33.45, 1.15) * mm});
            skLineSegment(sketch, "E86.242.15.0", {"start": v(34.05, 1.15) * mm, "end": v(34.05, -1.15) * mm});
            skLineSegment(sketch, "E86.245.15.0", {"start": v(33.45, -1.15) * mm, "end": v(31.45, -2.3) * mm});
            skLineSegment(sketch, "E86.248.15.0", {"start": v(29.45, 1.15) * mm, "end": v(31.45, 2.3) * mm});
            skLineSegment(sketch, "E86.251.15.0", {"start": v(33.75, -1.67) * mm, "end": v(31.75, -2.83) * mm});
            skLineSegment(sketch, "E86.254.15.0", {"start": v(33.75, 1.67) * mm, "end": v(31.75, 2.83) * mm});
            skLineSegment(sketch, "E86.257.15.0", {"start": v(33.45, 1.15) * mm, "end": v(33.45, -1.15) * mm});
            skLineSegment(sketch, "E86.260.15.0", {"start": v(29.45, -1.15) * mm, "end": v(31.45, -2.3) * mm});
            skLineSegment(sketch, "E86.263.15.0", {"start": v(31.45, 2.3) * mm, "end": v(33.45, 1.15) * mm});
            skLineSegment(sketch, "E86.266.15.0", {"start": v(31.45, -2.3) * mm, "end": v(33.45, -1.15) * mm});
            skLineSegment(sketch, "E86.269.15.0", {"start": v(31.75, -2.83) * mm, "end": v(33.75, -1.67) * mm});
            skLineSegment(sketch, "E86.272.15.0", {"start": v(29.45, 1.15) * mm, "end": v(31.45, 2.3) * mm});
            skLineSegment(sketch, "E86.275.15.0", {"start": v(33.45, -1.15) * mm, "end": v(33.45, 1.15) * mm});
            skLineSegment(sketch, "E86.278.15.0", {"start": v(29.45, -1.15) * mm, "end": v(31.45, -2.3) * mm});
            skLineSegment(sketch, "E86.281.15.0", {"start": v(33.45, 1.15) * mm, "end": v(31.45, 2.3) * mm});
            skLineSegment(sketch, "E86.284.15.0", {"start": v(31.45, -2.3) * mm, "end": v(33.45, -1.15) * mm});
            skLineSegment(sketch, "E86.287.15.0", {"start": v(31.75, -2.83) * mm, "end": v(33.75, -1.67) * mm});
            skLineSegment(sketch, "E86.290.15.0", {"start": v(31.45, 2.3) * mm, "end": v(29.45, 1.15) * mm});
            skLineSegment(sketch, "E86.293.15.0", {"start": v(31.45, 2.3) * mm, "end": v(33.45, 1.15) * mm});
            skPoint(sketch, "E86.0.16.0", {"position": v(38.65, -1.5) * mm});
            skPoint(sketch, "E86.1.16.0", {"position": v(37.35, -5.72) * mm});
            skCircle(sketch, "E86.2.16.0", {"center": v(36.05, 0) * mm, "radius": 2 * mm, "construction": true});
            skPoint(sketch, "E86.4.16.0", {"position": v(36.05, 3) * mm});
            skPoint(sketch, "E86.5.16.0", {"position": v(37.05, -6.24) * mm});
            skPoint(sketch, "E86.6.16.0", {"position": v(38.65, 1.5) * mm});
            skCircle(sketch, "E86.7.16.0", {"center": v(36.05, 0) * mm, "radius": 2.6 * mm, "construction": true});
            skPoint(sketch, "E86.10.16.0", {"position": v(36.05, -3) * mm});
            skCircle(sketch, "E86.11.16.0", {"center": v(36.05, -7.97) * mm, "radius": 2.6 * mm, "construction": true});
            skCircle(sketch, "E86.14.16.0", {"center": v(38.35, -3.98) * mm, "radius": 2.6 * mm, "construction": true});
            skCircle(sketch, "E86.20.16.0", {"center": v(38.35, -3.98) * mm, "radius": 2 * mm, "construction": true});
            skPoint(sketch, "E86.25.16.0", {"position": v(33.45, 0) * mm});
            skCircle(sketch, "E86.30.16.0", {"center": v(36.05, -7.97) * mm, "radius": 2 * mm, "construction": true});
            skArc(sketch, "E86.32.16.0", {"start": v(34.75, -2.25) * mm, "mid": v(38.65, 0) * mm, "end": v(34.75, 2.25) * mm, "construction": true});
            skPoint(sketch, "E86.36.16.0", {"position": v(36.05, 3) * mm});
            skCircle(sketch, "E86.37.16.0", {"center": v(36.05, 0) * mm, "radius": 2 * mm, "construction": true});
            skPoint(sketch, "E86.39.16.0", {"position": v(38.65, 1.5) * mm});
            skLineSegment(sketch, "E86.40.16.0", {"start": v(33.45, 6.81) * mm, "end": v(33.45, 9.12) * mm});
            skLineSegment(sketch, "E86.43.16.0", {"start": v(35.75, 5.14) * mm, "end": v(33.45, 6.47) * mm});
            skLineSegment(sketch, "E86.46.16.0", {"start": v(34.05, 6.81) * mm, "end": v(34.05, 9.12) * mm});
            skLineSegment(sketch, "E86.55.16.0", {"start": v(40.95, -2.48) * mm, "end": v(40.95, -5.48) * mm});
            skLineSegment(sketch, "E86.58.16.0", {"start": v(33.45, -6.47) * mm, "end": v(33.45, -9.25) * mm});
            skLineSegment(sketch, "E86.61.16.0", {"start": v(40.95, -5.48) * mm, "end": v(38.65, -6.81) * mm});
            skPoint(sketch, "E86.64.16.0", {"position": v(37.35, -5.72) * mm});
            skLineSegment(sketch, "E86.65.16.0", {"start": v(34.05, -6.81) * mm, "end": v(34.05, -9.12) * mm});
            skLineSegment(sketch, "E86.69.16.0", {"start": v(40.35, -2.83) * mm, "end": v(40.35, -5.14) * mm});
            skLineSegment(sketch, "E86.76.16.0", {"start": v(35.75, -5.14) * mm, "end": v(33.45, -6.47) * mm});
            skPoint(sketch, "E86.79.16.0", {"position": v(34.05, 0) * mm});
            skLineSegment(sketch, "E86.83.16.0", {"start": v(38.65, -9.25) * mm, "end": v(38.65, -6.81) * mm});
            skPoint(sketch, "E86.86.16.0", {"position": v(33.45, 0) * mm});
            skPoint(sketch, "E86.87.16.0", {"position": v(37.05, -6.24) * mm});
            skPoint(sketch, "E86.88.16.0", {"position": v(36.05, -3) * mm});
            skLineSegment(sketch, "E86.89.16.0", {"start": v(38.05, -9.12) * mm, "end": v(38.05, -6.81) * mm});
            skPoint(sketch, "E86.95.16.0", {"position": v(38.65, -1.5) * mm});
            skLineSegment(sketch, "E86.96.16.0", {"start": v(33.45, 1.5) * mm, "end": v(35.75, 2.83) * mm});
            skLineSegment(sketch, "E86.99.16.0", {"start": v(36.35, 5.14) * mm, "end": v(36.35, 2.83) * mm});
            skLineSegment(sketch, "E86.105.16.0", {"start": v(36.05, -5.66) * mm, "end": v(34.05, -6.81) * mm});
            skLineSegment(sketch, "E86.108.16.0", {"start": v(35.75, 5.14) * mm, "end": v(35.75, 2.83) * mm});
            skLineSegment(sketch, "E86.111.16.0", {"start": v(36.35, -5.14) * mm, "end": v(36.35, -2.83) * mm});
            skLineSegment(sketch, "E86.114.16.0", {"start": v(38.65, -1.15) * mm, "end": v(40.95, -2.48) * mm});
            skLineSegment(sketch, "E86.117.16.0", {"start": v(38.65, -1.15) * mm, "end": v(38.65, 1.15) * mm});
            skLineSegment(sketch, "E86.120.16.0", {"start": v(38.65, -9.25) * mm, "end": v(37.83, -9.25) * mm});
            skLineSegment(sketch, "E86.123.16.0", {"start": v(38.35, -1.67) * mm, "end": v(40.35, -2.83) * mm});
            skLineSegment(sketch, "E86.126.16.0", {"start": v(40.35, -5.14) * mm, "end": v(38.35, -6.3) * mm});
            skCircle(sketch, "E86.129.16.0", {"center": v(36.05, 0) * mm, "radius": 2 * mm, "construction": true});
            skLineSegment(sketch, "E86.131.16.0", {"start": v(34.05, -9.12) * mm, "end": v(34.27, -9.25) * mm});
            skLineSegment(sketch, "E86.137.16.0", {"start": v(35.75, -2.83) * mm, "end": v(33.45, -1.5) * mm});
            skLineSegment(sketch, "E86.140.16.0", {"start": v(33.45, 6.47) * mm, "end": v(33.45, 9.25) * mm});
            skPoint(sketch, "E86.143.16.0", {"position": v(34.05, 0) * mm});
            skLineSegment(sketch, "E86.144.16.0", {"start": v(35.75, -5.14) * mm, "end": v(35.75, -2.83) * mm});
            skLineSegment(sketch, "E86.147.16.0", {"start": v(33.45, -6.81) * mm, "end": v(33.45, -9.12) * mm});
            skLineSegment(sketch, "E86.150.16.0", {"start": v(38.65, 1.15) * mm, "end": v(40.95, 2.48) * mm});
            skLineSegment(sketch, "E86.153.16.0", {"start": v(36.05, 5.66) * mm, "end": v(34.05, 6.81) * mm});
            skLineSegment(sketch, "E86.156.16.0", {"start": v(33.45, -1.5) * mm, "end": v(33.45, 0) * mm});
            skLineSegment(sketch, "E86.162.16.0", {"start": v(34.05, 9.12) * mm, "end": v(34.27, 9.25) * mm});
            skLineSegment(sketch, "E86.165.16.0", {"start": v(38.65, -1.15) * mm, "end": v(38.65, 1.15) * mm});
            skLineSegment(sketch, "E86.168.16.0", {"start": v(33.45, 1.5) * mm, "end": v(35.75, 2.83) * mm});
            skLineSegment(sketch, "E86.171.16.0", {"start": v(38.35, -6.3) * mm, "end": v(36.35, -5.14) * mm});
            skLineSegment(sketch, "E86.174.16.0", {"start": v(37.83, -9.25) * mm, "end": v(38.05, -9.12) * mm});
            skLineSegment(sketch, "E86.180.16.0", {"start": v(38.05, -6.81) * mm, "end": v(36.05, -5.66) * mm});
            skLineSegment(sketch, "E86.183.16.0", {"start": v(34.27, -9.25) * mm, "end": v(33.45, -9.25) * mm});
            skCircle(sketch, "E86.189.16.0", {"center": v(36.05, 0) * mm, "radius": 2 * mm, "construction": true});
            skLineSegment(sketch, "E86.194.16.0", {"start": v(33.45, -1.5) * mm, "end": v(35.75, -2.83) * mm});
            skLineSegment(sketch, "E86.197.16.0", {"start": v(38.05, 1.15) * mm, "end": v(38.05, -1.15) * mm});
            skLineSegment(sketch, "E86.200.16.0", {"start": v(34.05, -1.15) * mm, "end": v(34.05, 1.15) * mm});
            skLineSegment(sketch, "E86.203.16.0", {"start": v(38.65, 1.15) * mm, "end": v(38.65, -1.15) * mm});
            skLineSegment(sketch, "E86.209.16.0", {"start": v(38.05, -6.81) * mm, "end": v(36.05, -5.66) * mm});
            skLineSegment(sketch, "E86.212.16.0", {"start": v(37.35, -5.72) * mm, "end": v(36.35, -5.14) * mm});
            skLineSegment(sketch, "E86.215.16.0", {"start": v(33.45, 1.5) * mm, "end": v(33.45, -1.5) * mm});
            skLineSegment(sketch, "E86.218.16.0", {"start": v(35.75, 2.83) * mm, "end": v(33.45, 1.5) * mm});
            skLineSegment(sketch, "E86.224.16.0", {"start": v(33.45, -1.5) * mm, "end": v(35.75, -2.83) * mm});
            skLineSegment(sketch, "E86.227.16.0", {"start": v(36.05, -2.3) * mm, "end": v(34.05, -1.15) * mm});
            skLineSegment(sketch, "E86.230.16.0", {"start": v(37.35, 2.25) * mm, "end": v(38.35, 1.67) * mm});
            skLineSegment(sketch, "E86.233.16.0", {"start": v(36.35, 2.83) * mm, "end": v(38.35, 1.67) * mm});
            skLineSegment(sketch, "E86.236.16.0", {"start": v(34.05, 1.15) * mm, "end": v(34.05, -1.15) * mm});
            skLineSegment(sketch, "E86.239.16.0", {"start": v(38.05, -1.15) * mm, "end": v(38.05, 1.15) * mm});
            skLineSegment(sketch, "E86.242.16.0", {"start": v(38.65, 1.15) * mm, "end": v(38.65, -1.15) * mm});
            skLineSegment(sketch, "E86.245.16.0", {"start": v(38.05, -1.15) * mm, "end": v(36.05, -2.3) * mm});
            skLineSegment(sketch, "E86.248.16.0", {"start": v(34.05, 1.15) * mm, "end": v(36.05, 2.3) * mm});
            skLineSegment(sketch, "E86.251.16.0", {"start": v(38.35, -1.67) * mm, "end": v(36.35, -2.83) * mm});
            skLineSegment(sketch, "E86.254.16.0", {"start": v(38.35, 1.67) * mm, "end": v(36.35, 2.83) * mm});
            skLineSegment(sketch, "E86.257.16.0", {"start": v(38.05, 1.15) * mm, "end": v(38.05, -1.15) * mm});
            skLineSegment(sketch, "E86.260.16.0", {"start": v(34.05, -1.15) * mm, "end": v(36.05, -2.3) * mm});
            skLineSegment(sketch, "E86.263.16.0", {"start": v(36.05, 2.3) * mm, "end": v(38.05, 1.15) * mm});
            skLineSegment(sketch, "E86.266.16.0", {"start": v(36.05, -2.3) * mm, "end": v(38.05, -1.15) * mm});
            skLineSegment(sketch, "E86.269.16.0", {"start": v(36.35, -2.83) * mm, "end": v(38.35, -1.67) * mm});
            skLineSegment(sketch, "E86.272.16.0", {"start": v(34.05, 1.15) * mm, "end": v(36.05, 2.3) * mm});
            skLineSegment(sketch, "E86.275.16.0", {"start": v(38.05, -1.15) * mm, "end": v(38.05, 1.15) * mm});
            skLineSegment(sketch, "E86.278.16.0", {"start": v(34.05, -1.15) * mm, "end": v(36.05, -2.3) * mm});
            skLineSegment(sketch, "E86.281.16.0", {"start": v(38.05, 1.15) * mm, "end": v(36.05, 2.3) * mm});
            skLineSegment(sketch, "E86.284.16.0", {"start": v(36.05, -2.3) * mm, "end": v(38.05, -1.15) * mm});
            skLineSegment(sketch, "E86.287.16.0", {"start": v(36.35, -2.83) * mm, "end": v(38.35, -1.67) * mm});
            skLineSegment(sketch, "E86.290.16.0", {"start": v(36.05, 2.3) * mm, "end": v(34.05, 1.15) * mm});
            skLineSegment(sketch, "E86.293.16.0", {"start": v(36.05, 2.3) * mm, "end": v(38.05, 1.15) * mm});
            skLineSegment(sketch, "E87", {"start": v(41.42, 10.26) * mm, "end": v(41, 8.03) * mm});
            skLineSegment(sketch, "E88", {"start": v(38.65, 0) * mm, "end": v(39.52, 0) * mm});
            skPoint(sketch, "E88.endSnap0", {"position": v(38.65, 0) * mm});
            skLineSegment(sketch, "E89.MirrorCS", {"start": v(38.35, 1.67) * mm, "end": v(40.35, 2.83) * mm});
            skLineSegment(sketch, "E90", {"start": v(40.35, 2.83) * mm, "end": v(40.95, 2.48) * mm});
            skLineSegment(sketch, "E91", {"start": v(40.95, -2.48) * mm, "end": v(40.35, -2.83) * mm});
            skSolve(sketch);
        }
        {
            var Q0;
            {var subQ0=sQuery(id+"F2.wireOp",EDGE,"E25.MirrorCS");Q0=makeQuery(id+"F2.imprint","IMPRINT",FACE,{"disambiguationData":[TD([[makeQuery(id+"F2.imprint","IMPRINT",EDGE,{"derivedFrom":subQ0}),1.0]])]});}
            var Q1;
            {var subQ0=sQuery(id+"F2.wireOp",EDGE,"E28.MirrorCS");Q1=makeQuery(id+"F2.imprint","IMPRINT",FACE,{"disambiguationData":[TD([[makeQuery(id+"F2.imprint","IMPRINT",EDGE,{"derivedFrom":subQ0}),1.0]])]});}
            var Q2;
            {var subQ0=sQuery(id+"F2.wireOp",EDGE,"E43.MirrorCS");Q2=makeQuery(id+"F2.imprint","IMPRINT",FACE,{"disambiguationData":[TD([[makeQuery(id+"F2.imprint","IMPRINT",EDGE,{"derivedFrom":subQ0}),-1.0]])]});}
            var Q3;
            {var subQ0=sQuery(id+"F2.wireOp",EDGE,"E78.MirrorCS");Q3=makeQuery(id+"F2.imprint","IMPRINT",FACE,{"disambiguationData":[TD([[makeQuery(id+"F2.imprint","IMPRINT",EDGE,{"derivedFrom":subQ0}),-1.0]])]});}
            var Q4;
            {var subQ0=sQuery(id+"F2.wireOp",EDGE,"E85.1.0.40");Q4=makeQuery(id+"F2.imprint","IMPRINT",FACE,{"disambiguationData":[TD([[makeQuery(id+"F2.imprint","IMPRINT",EDGE,{"derivedFrom":subQ0}),1.0]])]});}
            var Q5;
            {var subQ0=sQuery(id+"F2.wireOp",EDGE,"E85.1.0.41");Q5=makeQuery(id+"F2.imprint","IMPRINT",FACE,{"disambiguationData":[TD([[makeQuery(id+"F2.imprint","IMPRINT",EDGE,{"derivedFrom":subQ0}),-1.0]])]});}
            var Q6;
            {var subQ0=sQuery(id+"F2.wireOp",EDGE,"E85.1.0.56");Q6=makeQuery(id+"F2.imprint","IMPRINT",FACE,{"disambiguationData":[TD([[makeQuery(id+"F2.imprint","IMPRINT",EDGE,{"derivedFrom":subQ0}),-1.0]])]});}
            var Q7;
            {var subQ0=sQuery(id+"F2.wireOp",EDGE,"E85.1.0.70");Q7=makeQuery(id+"F2.imprint","IMPRINT",FACE,{"disambiguationData":[TD([[makeQuery(id+"F2.imprint","IMPRINT",EDGE,{"derivedFrom":subQ0}),1.0]])]});}
            var Q8;
            {var subQ0=sQuery(id+"F2.wireOp",EDGE,"E85.2.0.40");Q8=makeQuery(id+"F2.imprint","IMPRINT",FACE,{"disambiguationData":[TD([[makeQuery(id+"F2.imprint","IMPRINT",EDGE,{"derivedFrom":subQ0}),1.0]])]});}
            var Q9;
            {var subQ0=sQuery(id+"F2.wireOp",EDGE,"E85.2.0.41");Q9=makeQuery(id+"F2.imprint","IMPRINT",FACE,{"disambiguationData":[TD([[makeQuery(id+"F2.imprint","IMPRINT",EDGE,{"derivedFrom":subQ0}),-1.0]])]});}
            var Q10;
            {var subQ0=sQuery(id+"F2.wireOp",EDGE,"E85.2.0.56");Q10=makeQuery(id+"F2.imprint","IMPRINT",FACE,{"disambiguationData":[TD([[makeQuery(id+"F2.imprint","IMPRINT",EDGE,{"derivedFrom":subQ0}),-1.0]])]});}
            var Q11;
            {var subQ0=sQuery(id+"F2.wireOp",EDGE,"E85.2.0.70");Q11=makeQuery(id+"F2.imprint","IMPRINT",FACE,{"disambiguationData":[TD([[makeQuery(id+"F2.imprint","IMPRINT",EDGE,{"derivedFrom":subQ0}),1.0]])]});}
            var Q12;
            {var subQ0=sQuery(id+"F2.wireOp",EDGE,"E86.80.3.0");Q12=makeQuery(id+"F2.imprint","IMPRINT",FACE,{"disambiguationData":[TD([[makeQuery(id+"F2.imprint","IMPRINT",EDGE,{"derivedFrom":subQ0}),1.0]])]});}
            var Q13;
            {var subQ0=sQuery(id+"F2.wireOp",EDGE,"E86.83.3.0");Q13=makeQuery(id+"F2.imprint","IMPRINT",FACE,{"disambiguationData":[TD([[makeQuery(id+"F2.imprint","IMPRINT",EDGE,{"derivedFrom":subQ0}),-1.0]])]});}
            var Q14;
            {var subQ0=sQuery(id+"F2.wireOp",EDGE,"E86.120.3.0");Q14=makeQuery(id+"F2.imprint","IMPRINT",FACE,{"disambiguationData":[TD([[makeQuery(id+"F2.imprint","IMPRINT",EDGE,{"derivedFrom":subQ0}),-1.0]])]});}
            var Q15;
            {var subQ0=sQuery(id+"F2.wireOp",EDGE,"E86.159.3.0");Q15=makeQuery(id+"F2.imprint","IMPRINT",FACE,{"disambiguationData":[TD([[makeQuery(id+"F2.imprint","IMPRINT",EDGE,{"derivedFrom":subQ0}),1.0]])]});}
            var Q16;
            {var subQ0=sQuery(id+"F2.wireOp",EDGE,"E86.80.4.0");Q16=makeQuery(id+"F2.imprint","IMPRINT",FACE,{"disambiguationData":[TD([[makeQuery(id+"F2.imprint","IMPRINT",EDGE,{"derivedFrom":subQ0}),1.0]])]});}
            var Q17;
            {var subQ0=sQuery(id+"F2.wireOp",EDGE,"E86.83.4.0");Q17=makeQuery(id+"F2.imprint","IMPRINT",FACE,{"disambiguationData":[TD([[makeQuery(id+"F2.imprint","IMPRINT",EDGE,{"derivedFrom":subQ0}),-1.0]])]});}
            var Q18;
            {var subQ0=sQuery(id+"F2.wireOp",EDGE,"E86.120.4.0");Q18=makeQuery(id+"F2.imprint","IMPRINT",FACE,{"disambiguationData":[TD([[makeQuery(id+"F2.imprint","IMPRINT",EDGE,{"derivedFrom":subQ0}),-1.0]])]});}
            var Q19;
            {var subQ0=sQuery(id+"F2.wireOp",EDGE,"E86.159.4.0");Q19=makeQuery(id+"F2.imprint","IMPRINT",FACE,{"disambiguationData":[TD([[makeQuery(id+"F2.imprint","IMPRINT",EDGE,{"derivedFrom":subQ0}),1.0]])]});}
            var Q20;
            {var subQ0=sQuery(id+"F2.wireOp",EDGE,"E86.80.5.0");Q20=makeQuery(id+"F2.imprint","IMPRINT",FACE,{"disambiguationData":[TD([[makeQuery(id+"F2.imprint","IMPRINT",EDGE,{"derivedFrom":subQ0}),1.0]])]});}
            var Q21;
            {var subQ0=sQuery(id+"F2.wireOp",EDGE,"E86.83.5.0");Q21=makeQuery(id+"F2.imprint","IMPRINT",FACE,{"disambiguationData":[TD([[makeQuery(id+"F2.imprint","IMPRINT",EDGE,{"derivedFrom":subQ0}),-1.0]])]});}
            var Q22;
            {var subQ0=sQuery(id+"F2.wireOp",EDGE,"E86.120.5.0");Q22=makeQuery(id+"F2.imprint","IMPRINT",FACE,{"disambiguationData":[TD([[makeQuery(id+"F2.imprint","IMPRINT",EDGE,{"derivedFrom":subQ0}),-1.0]])]});}
            var Q23;
            {var subQ0=sQuery(id+"F2.wireOp",EDGE,"E86.159.5.0");Q23=makeQuery(id+"F2.imprint","IMPRINT",FACE,{"disambiguationData":[TD([[makeQuery(id+"F2.imprint","IMPRINT",EDGE,{"derivedFrom":subQ0}),1.0]])]});}
            var Q24;
            {var subQ0=sQuery(id+"F2.wireOp",EDGE,"E86.80.6.0");Q24=makeQuery(id+"F2.imprint","IMPRINT",FACE,{"disambiguationData":[TD([[makeQuery(id+"F2.imprint","IMPRINT",EDGE,{"derivedFrom":subQ0}),1.0]])]});}
            var Q25;
            {var subQ0=sQuery(id+"F2.wireOp",EDGE,"E86.83.6.0");Q25=makeQuery(id+"F2.imprint","IMPRINT",FACE,{"disambiguationData":[TD([[makeQuery(id+"F2.imprint","IMPRINT",EDGE,{"derivedFrom":subQ0}),-1.0]])]});}
            var Q26;
            {var subQ0=sQuery(id+"F2.wireOp",EDGE,"E86.120.6.0");Q26=makeQuery(id+"F2.imprint","IMPRINT",FACE,{"disambiguationData":[TD([[makeQuery(id+"F2.imprint","IMPRINT",EDGE,{"derivedFrom":subQ0}),-1.0]])]});}
            var Q27;
            {var subQ0=sQuery(id+"F2.wireOp",EDGE,"E86.159.6.0");Q27=makeQuery(id+"F2.imprint","IMPRINT",FACE,{"disambiguationData":[TD([[makeQuery(id+"F2.imprint","IMPRINT",EDGE,{"derivedFrom":subQ0}),1.0]])]});}
            var Q28;
            {var subQ0=sQuery(id+"F2.wireOp",EDGE,"E86.80.7.0");Q28=makeQuery(id+"F2.imprint","IMPRINT",FACE,{"disambiguationData":[TD([[makeQuery(id+"F2.imprint","IMPRINT",EDGE,{"derivedFrom":subQ0}),1.0]])]});}
            var Q29;
            {var subQ0=sQuery(id+"F2.wireOp",EDGE,"E86.83.7.0");Q29=makeQuery(id+"F2.imprint","IMPRINT",FACE,{"disambiguationData":[TD([[makeQuery(id+"F2.imprint","IMPRINT",EDGE,{"derivedFrom":subQ0}),-1.0]])]});}
            var Q30;
            {var subQ0=sQuery(id+"F2.wireOp",EDGE,"E86.120.7.0");Q30=makeQuery(id+"F2.imprint","IMPRINT",FACE,{"disambiguationData":[TD([[makeQuery(id+"F2.imprint","IMPRINT",EDGE,{"derivedFrom":subQ0}),-1.0]])]});}
            var Q31;
            {var subQ0=sQuery(id+"F2.wireOp",EDGE,"E86.159.7.0");Q31=makeQuery(id+"F2.imprint","IMPRINT",FACE,{"disambiguationData":[TD([[makeQuery(id+"F2.imprint","IMPRINT",EDGE,{"derivedFrom":subQ0}),1.0]])]});}
            var Q32;
            {var subQ0=sQuery(id+"F2.wireOp",EDGE,"E86.80.8.0");Q32=makeQuery(id+"F2.imprint","IMPRINT",FACE,{"disambiguationData":[TD([[makeQuery(id+"F2.imprint","IMPRINT",EDGE,{"derivedFrom":subQ0}),1.0]])]});}
            var Q33;
            {var subQ0=sQuery(id+"F2.wireOp",EDGE,"E86.83.8.0");Q33=makeQuery(id+"F2.imprint","IMPRINT",FACE,{"disambiguationData":[TD([[makeQuery(id+"F2.imprint","IMPRINT",EDGE,{"derivedFrom":subQ0}),-1.0]])]});}
            var Q34;
            {var subQ0=sQuery(id+"F2.wireOp",EDGE,"E86.120.8.0");Q34=makeQuery(id+"F2.imprint","IMPRINT",FACE,{"disambiguationData":[TD([[makeQuery(id+"F2.imprint","IMPRINT",EDGE,{"derivedFrom":subQ0}),-1.0]])]});}
            var Q35;
            {var subQ0=sQuery(id+"F2.wireOp",EDGE,"E86.159.8.0");Q35=makeQuery(id+"F2.imprint","IMPRINT",FACE,{"disambiguationData":[TD([[makeQuery(id+"F2.imprint","IMPRINT",EDGE,{"derivedFrom":subQ0}),1.0]])]});}
            var Q36;
            {var subQ0=sQuery(id+"F2.wireOp",EDGE,"E86.80.9.0");Q36=makeQuery(id+"F2.imprint","IMPRINT",FACE,{"disambiguationData":[TD([[makeQuery(id+"F2.imprint","IMPRINT",EDGE,{"derivedFrom":subQ0}),1.0]])]});}
            var Q37;
            {var subQ0=sQuery(id+"F2.wireOp",EDGE,"E86.83.9.0");Q37=makeQuery(id+"F2.imprint","IMPRINT",FACE,{"disambiguationData":[TD([[makeQuery(id+"F2.imprint","IMPRINT",EDGE,{"derivedFrom":subQ0}),-1.0]])]});}
            var Q38;
            {var subQ0=sQuery(id+"F2.wireOp",EDGE,"E86.120.9.0");Q38=makeQuery(id+"F2.imprint","IMPRINT",FACE,{"disambiguationData":[TD([[makeQuery(id+"F2.imprint","IMPRINT",EDGE,{"derivedFrom":subQ0}),-1.0]])]});}
            var Q39;
            {var subQ0=sQuery(id+"F2.wireOp",EDGE,"E86.159.9.0");Q39=makeQuery(id+"F2.imprint","IMPRINT",FACE,{"disambiguationData":[TD([[makeQuery(id+"F2.imprint","IMPRINT",EDGE,{"derivedFrom":subQ0}),1.0]])]});}
            var Q40;
            {var subQ0=sQuery(id+"F2.wireOp",EDGE,"E86.80.10.0");Q40=makeQuery(id+"F2.imprint","IMPRINT",FACE,{"disambiguationData":[TD([[makeQuery(id+"F2.imprint","IMPRINT",EDGE,{"derivedFrom":subQ0}),1.0]])]});}
            var Q41;
            {var subQ0=sQuery(id+"F2.wireOp",EDGE,"E86.83.10.0");Q41=makeQuery(id+"F2.imprint","IMPRINT",FACE,{"disambiguationData":[TD([[makeQuery(id+"F2.imprint","IMPRINT",EDGE,{"derivedFrom":subQ0}),-1.0]])]});}
            var Q42;
            {var subQ0=sQuery(id+"F2.wireOp",EDGE,"E86.120.10.0");Q42=makeQuery(id+"F2.imprint","IMPRINT",FACE,{"disambiguationData":[TD([[makeQuery(id+"F2.imprint","IMPRINT",EDGE,{"derivedFrom":subQ0}),-1.0]])]});}
            var Q43;
            {var subQ0=sQuery(id+"F2.wireOp",EDGE,"E86.159.10.0");Q43=makeQuery(id+"F2.imprint","IMPRINT",FACE,{"disambiguationData":[TD([[makeQuery(id+"F2.imprint","IMPRINT",EDGE,{"derivedFrom":subQ0}),1.0]])]});}
            var Q44;
            {var subQ0=sQuery(id+"F2.wireOp",EDGE,"E86.80.11.0");Q44=makeQuery(id+"F2.imprint","IMPRINT",FACE,{"disambiguationData":[TD([[makeQuery(id+"F2.imprint","IMPRINT",EDGE,{"derivedFrom":subQ0}),1.0]])]});}
            var Q45;
            {var subQ0=sQuery(id+"F2.wireOp",EDGE,"E86.83.11.0");Q45=makeQuery(id+"F2.imprint","IMPRINT",FACE,{"disambiguationData":[TD([[makeQuery(id+"F2.imprint","IMPRINT",EDGE,{"derivedFrom":subQ0}),-1.0]])]});}
            var Q46;
            {var subQ0=sQuery(id+"F2.wireOp",EDGE,"E86.120.11.0");Q46=makeQuery(id+"F2.imprint","IMPRINT",FACE,{"disambiguationData":[TD([[makeQuery(id+"F2.imprint","IMPRINT",EDGE,{"derivedFrom":subQ0}),-1.0]])]});}
            var Q47;
            {var subQ0=sQuery(id+"F2.wireOp",EDGE,"E86.159.11.0");Q47=makeQuery(id+"F2.imprint","IMPRINT",FACE,{"disambiguationData":[TD([[makeQuery(id+"F2.imprint","IMPRINT",EDGE,{"derivedFrom":subQ0}),1.0]])]});}
            var Q48;
            {var subQ0=sQuery(id+"F2.wireOp",EDGE,"E86.80.12.0");Q48=makeQuery(id+"F2.imprint","IMPRINT",FACE,{"disambiguationData":[TD([[makeQuery(id+"F2.imprint","IMPRINT",EDGE,{"derivedFrom":subQ0}),1.0]])]});}
            var Q49;
            {var subQ0=sQuery(id+"F2.wireOp",EDGE,"E86.83.12.0");Q49=makeQuery(id+"F2.imprint","IMPRINT",FACE,{"disambiguationData":[TD([[makeQuery(id+"F2.imprint","IMPRINT",EDGE,{"derivedFrom":subQ0}),-1.0]])]});}
            var Q50;
            {var subQ0=sQuery(id+"F2.wireOp",EDGE,"E86.120.12.0");Q50=makeQuery(id+"F2.imprint","IMPRINT",FACE,{"disambiguationData":[TD([[makeQuery(id+"F2.imprint","IMPRINT",EDGE,{"derivedFrom":subQ0}),-1.0]])]});}
            var Q51;
            {var subQ0=sQuery(id+"F2.wireOp",EDGE,"E86.159.12.0");Q51=makeQuery(id+"F2.imprint","IMPRINT",FACE,{"disambiguationData":[TD([[makeQuery(id+"F2.imprint","IMPRINT",EDGE,{"derivedFrom":subQ0}),1.0]])]});}
            var Q52;
            {var subQ0=sQuery(id+"F2.wireOp",EDGE,"E86.80.13.0");Q52=makeQuery(id+"F2.imprint","IMPRINT",FACE,{"disambiguationData":[TD([[makeQuery(id+"F2.imprint","IMPRINT",EDGE,{"derivedFrom":subQ0}),1.0]])]});}
            var Q53;
            {var subQ0=sQuery(id+"F2.wireOp",EDGE,"E86.83.13.0");Q53=makeQuery(id+"F2.imprint","IMPRINT",FACE,{"disambiguationData":[TD([[makeQuery(id+"F2.imprint","IMPRINT",EDGE,{"derivedFrom":subQ0}),-1.0]])]});}
            var Q54;
            {var subQ0=sQuery(id+"F2.wireOp",EDGE,"E86.120.13.0");Q54=makeQuery(id+"F2.imprint","IMPRINT",FACE,{"disambiguationData":[TD([[makeQuery(id+"F2.imprint","IMPRINT",EDGE,{"derivedFrom":subQ0}),-1.0]])]});}
            var Q55;
            {var subQ0=sQuery(id+"F2.wireOp",EDGE,"E86.159.13.0");Q55=makeQuery(id+"F2.imprint","IMPRINT",FACE,{"disambiguationData":[TD([[makeQuery(id+"F2.imprint","IMPRINT",EDGE,{"derivedFrom":subQ0}),1.0]])]});}
            var Q56;
            {var subQ0=sQuery(id+"F2.wireOp",EDGE,"E86.80.14.0");Q56=makeQuery(id+"F2.imprint","IMPRINT",FACE,{"disambiguationData":[TD([[makeQuery(id+"F2.imprint","IMPRINT",EDGE,{"derivedFrom":subQ0}),1.0]])]});}
            var Q57;
            {var subQ0=sQuery(id+"F2.wireOp",EDGE,"E86.83.14.0");Q57=makeQuery(id+"F2.imprint","IMPRINT",FACE,{"disambiguationData":[TD([[makeQuery(id+"F2.imprint","IMPRINT",EDGE,{"derivedFrom":subQ0}),-1.0]])]});}
            var Q58;
            {var subQ0=sQuery(id+"F2.wireOp",EDGE,"E86.120.14.0");Q58=makeQuery(id+"F2.imprint","IMPRINT",FACE,{"disambiguationData":[TD([[makeQuery(id+"F2.imprint","IMPRINT",EDGE,{"derivedFrom":subQ0}),-1.0]])]});}
            var Q59;
            {var subQ0=sQuery(id+"F2.wireOp",EDGE,"E86.159.14.0");Q59=makeQuery(id+"F2.imprint","IMPRINT",FACE,{"disambiguationData":[TD([[makeQuery(id+"F2.imprint","IMPRINT",EDGE,{"derivedFrom":subQ0}),1.0]])]});}
            var Q60;
            {var subQ0=sQuery(id+"F2.wireOp",EDGE,"E86.83.15.0");Q60=makeQuery(id+"F2.imprint","IMPRINT",FACE,{"disambiguationData":[TD([[makeQuery(id+"F2.imprint","IMPRINT",EDGE,{"derivedFrom":subQ0}),-1.0]])]});}
            var Q61;
            {var subQ0=sQuery(id+"F2.wireOp",EDGE,"E86.120.15.0");Q61=makeQuery(id+"F2.imprint","IMPRINT",FACE,{"disambiguationData":[TD([[makeQuery(id+"F2.imprint","IMPRINT",EDGE,{"derivedFrom":subQ0}),-1.0]])]});}
            var Q62;
            {var subQ0=sQuery(id+"F2.wireOp",EDGE,"E86.159.15.0");Q62=makeQuery(id+"F2.imprint","IMPRINT",FACE,{"disambiguationData":[TD([[makeQuery(id+"F2.imprint","IMPRINT",EDGE,{"derivedFrom":subQ0}),1.0]])]});}
            var Q63;
            {var subQ2=sQuery(id+"F2.wireOp",EDGE,"E21.MirrorCS");Q63=makeQuery(id+"F2.imprint","IMPRINT",FACE,{"disambiguationData":[TD([[makeQuery(id+"F2.imprint","IMPRINT",EDGE,{"derivedFrom":subQ2}),-1.0]])]});}
            var Q64;
            {var subQ2=sQuery(id+"F2.wireOp",EDGE,"E68.MirrorCS");Q64=makeQuery(id+"F2.imprint","IMPRINT",FACE,{"disambiguationData":[TD([[makeQuery(id+"F2.imprint","IMPRINT",EDGE,{"derivedFrom":subQ2}),1.0]])]});}
            var Q65;
            {var subQ6=sQuery(id+"F2.wireOp",EDGE,"E85.1.0.27");Q65=makeQuery(id+"F2.imprint","IMPRINT",FACE,{"disambiguationData":[TD([[makeQuery(id+"F2.imprint","IMPRINT",EDGE,{"derivedFrom":subQ6}),-1.0]])]});}
            var Q66;
            {var subQ1=sQuery(id+"F2.wireOp",EDGE,"E85.1.0.31");Q66=makeQuery(id+"F2.imprint","IMPRINT",FACE,{"disambiguationData":[TD([[makeQuery(id+"F2.imprint","IMPRINT",EDGE,{"derivedFrom":subQ1}),1.0]])]});}
            var Q67;
            {var subQ3=sQuery(id+"F2.wireOp",EDGE,"E85.2.0.27");Q67=makeQuery(id+"F2.imprint","IMPRINT",FACE,{"disambiguationData":[TD([[makeQuery(id+"F2.imprint","IMPRINT",EDGE,{"derivedFrom":subQ3}),-1.0]])]});}
            var Q68;
            {var subQ4=sQuery(id+"F2.wireOp",EDGE,"E85.2.0.31");Q68=makeQuery(id+"F2.imprint","IMPRINT",FACE,{"disambiguationData":[TD([[makeQuery(id+"F2.imprint","IMPRINT",EDGE,{"derivedFrom":subQ4}),1.0]])]});}
            var Q69;
            {var subQ3=sQuery(id+"F2.wireOp",EDGE,"E86.49.3.0");Q69=makeQuery(id+"F2.imprint","IMPRINT",FACE,{"disambiguationData":[TD([[makeQuery(id+"F2.imprint","IMPRINT",EDGE,{"derivedFrom":subQ3}),-1.0]])]});}
            var Q70;
            {var subQ2=sQuery(id+"F2.wireOp",EDGE,"E86.61.3.0");Q70=makeQuery(id+"F2.imprint","IMPRINT",FACE,{"disambiguationData":[TD([[makeQuery(id+"F2.imprint","IMPRINT",EDGE,{"derivedFrom":subQ2}),1.0]])]});}
            var Q71;
            {var subQ3=sQuery(id+"F2.wireOp",EDGE,"E86.49.4.0");Q71=makeQuery(id+"F2.imprint","IMPRINT",FACE,{"disambiguationData":[TD([[makeQuery(id+"F2.imprint","IMPRINT",EDGE,{"derivedFrom":subQ3}),-1.0]])]});}
            var Q72;
            {var subQ5=sQuery(id+"F2.wireOp",EDGE,"E86.61.4.0");Q72=makeQuery(id+"F2.imprint","IMPRINT",FACE,{"disambiguationData":[TD([[makeQuery(id+"F2.imprint","IMPRINT",EDGE,{"derivedFrom":subQ5}),1.0]])]});}
            var Q73;
            {var subQ3=sQuery(id+"F2.wireOp",EDGE,"E86.49.5.0");Q73=makeQuery(id+"F2.imprint","IMPRINT",FACE,{"disambiguationData":[TD([[makeQuery(id+"F2.imprint","IMPRINT",EDGE,{"derivedFrom":subQ3}),-1.0]])]});}
            var Q74;
            {var subQ2=sQuery(id+"F2.wireOp",EDGE,"E86.61.5.0");Q74=makeQuery(id+"F2.imprint","IMPRINT",FACE,{"disambiguationData":[TD([[makeQuery(id+"F2.imprint","IMPRINT",EDGE,{"derivedFrom":subQ2}),1.0]])]});}
            var Q75;
            {var subQ6=sQuery(id+"F2.wireOp",EDGE,"E86.49.6.0");Q75=makeQuery(id+"F2.imprint","IMPRINT",FACE,{"disambiguationData":[TD([[makeQuery(id+"F2.imprint","IMPRINT",EDGE,{"derivedFrom":subQ6}),-1.0]])]});}
            var Q76;
            {var subQ1=sQuery(id+"F2.wireOp",EDGE,"E86.61.6.0");Q76=makeQuery(id+"F2.imprint","IMPRINT",FACE,{"disambiguationData":[TD([[makeQuery(id+"F2.imprint","IMPRINT",EDGE,{"derivedFrom":subQ1}),1.0]])]});}
            var Q77;
            {var subQ3=sQuery(id+"F2.wireOp",EDGE,"E86.49.7.0");Q77=makeQuery(id+"F2.imprint","IMPRINT",FACE,{"disambiguationData":[TD([[makeQuery(id+"F2.imprint","IMPRINT",EDGE,{"derivedFrom":subQ3}),-1.0]])]});}
            var Q78;
            {var subQ4=sQuery(id+"F2.wireOp",EDGE,"E86.61.7.0");Q78=makeQuery(id+"F2.imprint","IMPRINT",FACE,{"disambiguationData":[TD([[makeQuery(id+"F2.imprint","IMPRINT",EDGE,{"derivedFrom":subQ4}),1.0]])]});}
            var Q79;
            {var subQ3=sQuery(id+"F2.wireOp",EDGE,"E86.49.8.0");Q79=makeQuery(id+"F2.imprint","IMPRINT",FACE,{"disambiguationData":[TD([[makeQuery(id+"F2.imprint","IMPRINT",EDGE,{"derivedFrom":subQ3}),-1.0]])]});}
            var Q80;
            {var subQ1=sQuery(id+"F2.wireOp",EDGE,"E86.61.8.0");Q80=makeQuery(id+"F2.imprint","IMPRINT",FACE,{"disambiguationData":[TD([[makeQuery(id+"F2.imprint","IMPRINT",EDGE,{"derivedFrom":subQ1}),1.0]])]});}
            var Q81;
            {var subQ2=sQuery(id+"F2.wireOp",EDGE,"E86.49.9.0");Q81=makeQuery(id+"F2.imprint","IMPRINT",FACE,{"disambiguationData":[TD([[makeQuery(id+"F2.imprint","IMPRINT",EDGE,{"derivedFrom":subQ2}),-1.0]])]});}
            var Q82;
            {var subQ5=sQuery(id+"F2.wireOp",EDGE,"E86.61.9.0");Q82=makeQuery(id+"F2.imprint","IMPRINT",FACE,{"disambiguationData":[TD([[makeQuery(id+"F2.imprint","IMPRINT",EDGE,{"derivedFrom":subQ5}),1.0]])]});}
            var Q83;
            {var subQ3=sQuery(id+"F2.wireOp",EDGE,"E86.49.10.0");Q83=makeQuery(id+"F2.imprint","IMPRINT",FACE,{"disambiguationData":[TD([[makeQuery(id+"F2.imprint","IMPRINT",EDGE,{"derivedFrom":subQ3}),-1.0]])]});}
            var Q84;
            {var subQ2=sQuery(id+"F2.wireOp",EDGE,"E86.61.10.0");Q84=makeQuery(id+"F2.imprint","IMPRINT",FACE,{"disambiguationData":[TD([[makeQuery(id+"F2.imprint","IMPRINT",EDGE,{"derivedFrom":subQ2}),1.0]])]});}
            var Q85;
            {var subQ3=sQuery(id+"F2.wireOp",EDGE,"E86.49.11.0");Q85=makeQuery(id+"F2.imprint","IMPRINT",FACE,{"disambiguationData":[TD([[makeQuery(id+"F2.imprint","IMPRINT",EDGE,{"derivedFrom":subQ3}),-1.0]])]});}
            var Q86;
            {var subQ2=sQuery(id+"F2.wireOp",EDGE,"E86.61.11.0");Q86=makeQuery(id+"F2.imprint","IMPRINT",FACE,{"disambiguationData":[TD([[makeQuery(id+"F2.imprint","IMPRINT",EDGE,{"derivedFrom":subQ2}),1.0]])]});}
            var Q87;
            {var subQ3=sQuery(id+"F2.wireOp",EDGE,"E86.49.12.0");Q87=makeQuery(id+"F2.imprint","IMPRINT",FACE,{"disambiguationData":[TD([[makeQuery(id+"F2.imprint","IMPRINT",EDGE,{"derivedFrom":subQ3}),-1.0]])]});}
            var Q88;
            {var subQ2=sQuery(id+"F2.wireOp",EDGE,"E86.61.12.0");Q88=makeQuery(id+"F2.imprint","IMPRINT",FACE,{"disambiguationData":[TD([[makeQuery(id+"F2.imprint","IMPRINT",EDGE,{"derivedFrom":subQ2}),1.0]])]});}
            var Q89;
            {var subQ3=sQuery(id+"F2.wireOp",EDGE,"E86.49.13.0");Q89=makeQuery(id+"F2.imprint","IMPRINT",FACE,{"disambiguationData":[TD([[makeQuery(id+"F2.imprint","IMPRINT",EDGE,{"derivedFrom":subQ3}),-1.0]])]});}
            var Q90;
            {var subQ2=sQuery(id+"F2.wireOp",EDGE,"E86.61.13.0");Q90=makeQuery(id+"F2.imprint","IMPRINT",FACE,{"disambiguationData":[TD([[makeQuery(id+"F2.imprint","IMPRINT",EDGE,{"derivedFrom":subQ2}),1.0]])]});}
            var Q91;
            {var subQ1=sQuery(id+"F2.wireOp",EDGE,"E86.49.14.0");Q91=makeQuery(id+"F2.imprint","IMPRINT",FACE,{"disambiguationData":[TD([[makeQuery(id+"F2.imprint","IMPRINT",EDGE,{"derivedFrom":subQ1}),-1.0]])]});}
            var Q92;
            {var subQ2=sQuery(id+"F2.wireOp",EDGE,"E86.61.14.0");Q92=makeQuery(id+"F2.imprint","IMPRINT",FACE,{"disambiguationData":[TD([[makeQuery(id+"F2.imprint","IMPRINT",EDGE,{"derivedFrom":subQ2}),1.0]])]});}
            var Q93;
            {var subQ18=sQuery(id+"F2.wireOp",EDGE,"E13.MirrorCS");Q93=makeQuery(id+"F2.imprint","IMPRINT",FACE,{"disambiguationData":[TD([[makeQuery(id+"F2.imprint","IMPRINT",EDGE,{"derivedFrom":subQ18}),-1.0]])]});}
            var Q94;
            {var subQ8=sQuery(id+"F2.wireOp",EDGE,"E86.114.15.0");Q94=makeQuery(id+"F2.imprint","IMPRINT",FACE,{"disambiguationData":[TD([[makeQuery(id+"F2.imprint","IMPRINT",EDGE,{"derivedFrom":subQ8}),1.0]])]});}
            var Q95;
            {var subQ0=sQuery(id+"F2.wireOp",EDGE,"E85.1.0.31");Q95=makeQuery(id+"F2.imprint","IMPRINT",FACE,{"disambiguationData":[TD([[makeQuery(id+"F2.imprint","IMPRINT",EDGE,{"derivedFrom":subQ0}),-1.0]])]});}
            var Q96;
            {var subQ27=sQuery(id+"F2.wireOp",EDGE,"E86.49.15.0");Q96=makeQuery(id+"F2.imprint","IMPRINT",FACE,{"disambiguationData":[TD([[makeQuery(id+"F2.imprint","IMPRINT",EDGE,{"derivedFrom":subQ27}),1.0]])]});}
            var Q97;
            {var subQ6=sQuery(id+"F2.wireOp",EDGE,"E21.MirrorCS");Q97=makeQuery(id+"F2.imprint","IMPRINT",FACE,{"disambiguationData":[TD([[makeQuery(id+"F2.imprint","IMPRINT",EDGE,{"derivedFrom":subQ6}),1.0]])]});}
            var Q98;
            {var subQ9=sQuery(id+"F2.wireOp",EDGE,"E85.1.0.27");Q98=makeQuery(id+"F2.imprint","IMPRINT",FACE,{"disambiguationData":[TD([[makeQuery(id+"F2.imprint","IMPRINT",EDGE,{"derivedFrom":subQ9}),1.0]])]});}
            var Q99;
            {var subQ0=sQuery(id+"F2.wireOp",EDGE,"E85.2.0.27");Q99=makeQuery(id+"F2.imprint","IMPRINT",FACE,{"disambiguationData":[TD([[makeQuery(id+"F2.imprint","IMPRINT",EDGE,{"derivedFrom":subQ0}),1.0]])]});}
            var Q100;
            {var subQ28=sQuery(id+"F2.wireOp",EDGE,"E86.49.3.0");Q100=makeQuery(id+"F2.imprint","IMPRINT",FACE,{"disambiguationData":[TD([[makeQuery(id+"F2.imprint","IMPRINT",EDGE,{"derivedFrom":subQ28}),1.0]])]});}
            var Q101;
            {var subQ25=sQuery(id+"F2.wireOp",EDGE,"E86.49.4.0");Q101=makeQuery(id+"F2.imprint","IMPRINT",FACE,{"disambiguationData":[TD([[makeQuery(id+"F2.imprint","IMPRINT",EDGE,{"derivedFrom":subQ25}),1.0]])]});}
            var Q102;
            {var subQ10=sQuery(id+"F2.wireOp",EDGE,"E86.49.5.0");Q102=makeQuery(id+"F2.imprint","IMPRINT",FACE,{"disambiguationData":[TD([[makeQuery(id+"F2.imprint","IMPRINT",EDGE,{"derivedFrom":subQ10}),1.0]])]});}
            var Q103;
            {var subQ27=sQuery(id+"F2.wireOp",EDGE,"E86.49.6.0");Q103=makeQuery(id+"F2.imprint","IMPRINT",FACE,{"disambiguationData":[TD([[makeQuery(id+"F2.imprint","IMPRINT",EDGE,{"derivedFrom":subQ27}),1.0]])]});}
            var Q104;
            {var subQ19=sQuery(id+"F2.wireOp",EDGE,"E86.49.7.0");Q104=makeQuery(id+"F2.imprint","IMPRINT",FACE,{"disambiguationData":[TD([[makeQuery(id+"F2.imprint","IMPRINT",EDGE,{"derivedFrom":subQ19}),1.0]])]});}
            var Q105;
            {var subQ27=sQuery(id+"F2.wireOp",EDGE,"E86.49.8.0");Q105=makeQuery(id+"F2.imprint","IMPRINT",FACE,{"disambiguationData":[TD([[makeQuery(id+"F2.imprint","IMPRINT",EDGE,{"derivedFrom":subQ27}),1.0]])]});}
            var Q106;
            {var subQ23=sQuery(id+"F2.wireOp",EDGE,"E86.49.9.0");Q106=makeQuery(id+"F2.imprint","IMPRINT",FACE,{"disambiguationData":[TD([[makeQuery(id+"F2.imprint","IMPRINT",EDGE,{"derivedFrom":subQ23}),1.0]])]});}
            var Q107;
            {var subQ29=sQuery(id+"F2.wireOp",EDGE,"E86.49.10.0");Q107=makeQuery(id+"F2.imprint","IMPRINT",FACE,{"disambiguationData":[TD([[makeQuery(id+"F2.imprint","IMPRINT",EDGE,{"derivedFrom":subQ29}),1.0]])]});}
            var Q108;
            {var subQ22=sQuery(id+"F2.wireOp",EDGE,"E86.49.11.0");Q108=makeQuery(id+"F2.imprint","IMPRINT",FACE,{"disambiguationData":[TD([[makeQuery(id+"F2.imprint","IMPRINT",EDGE,{"derivedFrom":subQ22}),1.0]])]});}
            var Q109;
            {var subQ28=sQuery(id+"F2.wireOp",EDGE,"E86.49.12.0");Q109=makeQuery(id+"F2.imprint","IMPRINT",FACE,{"disambiguationData":[TD([[makeQuery(id+"F2.imprint","IMPRINT",EDGE,{"derivedFrom":subQ28}),1.0]])]});}
            var Q110;
            {var subQ25=sQuery(id+"F2.wireOp",EDGE,"E86.49.13.0");Q110=makeQuery(id+"F2.imprint","IMPRINT",FACE,{"disambiguationData":[TD([[makeQuery(id+"F2.imprint","IMPRINT",EDGE,{"derivedFrom":subQ25}),1.0]])]});}
            var Q111;
            {var subQ22=sQuery(id+"F2.wireOp",EDGE,"E86.49.14.0");Q111=makeQuery(id+"F2.imprint","IMPRINT",FACE,{"disambiguationData":[TD([[makeQuery(id+"F2.imprint","IMPRINT",EDGE,{"derivedFrom":subQ22}),1.0]])]});}
            var Q112;
            {var subQ6=sQuery(id+"F2.wireOp",EDGE,"E37.trimOffspring");Q112=makeQuery(id+"F2.imprint","IMPRINT",FACE,{"disambiguationData":[TD([[makeQuery(id+"F2.imprint","IMPRINT",EDGE,{"derivedFrom":subQ6}),-1.0]])]});}
            var Q113;
            {var subQ2=sQuery(id+"F2.wireOp",EDGE,"E74.MirrorCS");Q113=makeQuery(id+"F2.imprint","IMPRINT",FACE,{"disambiguationData":[TD([[makeQuery(id+"F2.imprint","IMPRINT",EDGE,{"derivedFrom":subQ2}),1.0]])]});}
            var Q114;
            {var subQ9=sQuery(id+"F2.wireOp",EDGE,"E85.1.0.67");Q114=makeQuery(id+"F2.imprint","IMPRINT",FACE,{"disambiguationData":[TD([[makeQuery(id+"F2.imprint","IMPRINT",EDGE,{"derivedFrom":subQ9}),-1.0]])]});}
            var Q115;
            {var subQ2=sQuery(id+"F2.wireOp",EDGE,"E85.1.0.54");Q115=makeQuery(id+"F2.imprint","IMPRINT",FACE,{"disambiguationData":[TD([[makeQuery(id+"F2.imprint","IMPRINT",EDGE,{"derivedFrom":subQ2}),1.0]])]});}
            var Q116;
            {var subQ1=sQuery(id+"F2.wireOp",EDGE,"E85.2.0.54");Q116=makeQuery(id+"F2.imprint","IMPRINT",FACE,{"disambiguationData":[TD([[makeQuery(id+"F2.imprint","IMPRINT",EDGE,{"derivedFrom":subQ1}),1.0]])]});}
            var Q117;
            {var subQ7=sQuery(id+"F2.wireOp",EDGE,"E85.2.0.67");Q117=makeQuery(id+"F2.imprint","IMPRINT",FACE,{"disambiguationData":[TD([[makeQuery(id+"F2.imprint","IMPRINT",EDGE,{"derivedFrom":subQ7}),-1.0]])]});}
            var Q118;
            {var subQ6=sQuery(id+"F2.wireOp",EDGE,"E86.150.3.0");Q118=makeQuery(id+"F2.imprint","IMPRINT",FACE,{"disambiguationData":[TD([[makeQuery(id+"F2.imprint","IMPRINT",EDGE,{"derivedFrom":subQ6}),-1.0]])]});}
            var Q119;
            {var subQ1=sQuery(id+"F2.wireOp",EDGE,"E86.114.3.0");Q119=makeQuery(id+"F2.imprint","IMPRINT",FACE,{"disambiguationData":[TD([[makeQuery(id+"F2.imprint","IMPRINT",EDGE,{"derivedFrom":subQ1}),1.0]])]});}
            var Q120;
            {var subQ6=sQuery(id+"F2.wireOp",EDGE,"E86.150.4.0");Q120=makeQuery(id+"F2.imprint","IMPRINT",FACE,{"disambiguationData":[TD([[makeQuery(id+"F2.imprint","IMPRINT",EDGE,{"derivedFrom":subQ6}),-1.0]])]});}
            var Q121;
            {var subQ0=sQuery(id+"F2.wireOp",EDGE,"E86.114.4.0");Q121=makeQuery(id+"F2.imprint","IMPRINT",FACE,{"disambiguationData":[TD([[makeQuery(id+"F2.imprint","IMPRINT",EDGE,{"derivedFrom":subQ0}),1.0]])]});}
            var Q122;
            {var subQ6=sQuery(id+"F2.wireOp",EDGE,"E86.150.5.0");Q122=makeQuery(id+"F2.imprint","IMPRINT",FACE,{"disambiguationData":[TD([[makeQuery(id+"F2.imprint","IMPRINT",EDGE,{"derivedFrom":subQ6}),-1.0]])]});}
            var Q123;
            {var subQ1=sQuery(id+"F2.wireOp",EDGE,"E86.114.5.0");Q123=makeQuery(id+"F2.imprint","IMPRINT",FACE,{"disambiguationData":[TD([[makeQuery(id+"F2.imprint","IMPRINT",EDGE,{"derivedFrom":subQ1}),1.0]])]});}
            var Q124;
            {var subQ6=sQuery(id+"F2.wireOp",EDGE,"E86.150.6.0");Q124=makeQuery(id+"F2.imprint","IMPRINT",FACE,{"disambiguationData":[TD([[makeQuery(id+"F2.imprint","IMPRINT",EDGE,{"derivedFrom":subQ6}),-1.0]])]});}
            var Q125;
            {var subQ1=sQuery(id+"F2.wireOp",EDGE,"E86.114.6.0");Q125=makeQuery(id+"F2.imprint","IMPRINT",FACE,{"disambiguationData":[TD([[makeQuery(id+"F2.imprint","IMPRINT",EDGE,{"derivedFrom":subQ1}),1.0]])]});}
            var Q126;
            {var subQ4=sQuery(id+"F2.wireOp",EDGE,"E86.150.7.0");Q126=makeQuery(id+"F2.imprint","IMPRINT",FACE,{"disambiguationData":[TD([[makeQuery(id+"F2.imprint","IMPRINT",EDGE,{"derivedFrom":subQ4}),-1.0]])]});}
            var Q127;
            {var subQ1=sQuery(id+"F2.wireOp",EDGE,"E86.114.7.0");Q127=makeQuery(id+"F2.imprint","IMPRINT",FACE,{"disambiguationData":[TD([[makeQuery(id+"F2.imprint","IMPRINT",EDGE,{"derivedFrom":subQ1}),1.0]])]});}
            var Q128;
            {var subQ6=sQuery(id+"F2.wireOp",EDGE,"E86.150.8.0");Q128=makeQuery(id+"F2.imprint","IMPRINT",FACE,{"disambiguationData":[TD([[makeQuery(id+"F2.imprint","IMPRINT",EDGE,{"derivedFrom":subQ6}),-1.0]])]});}
            var Q129;
            {var subQ1=sQuery(id+"F2.wireOp",EDGE,"E86.114.8.0");Q129=makeQuery(id+"F2.imprint","IMPRINT",FACE,{"disambiguationData":[TD([[makeQuery(id+"F2.imprint","IMPRINT",EDGE,{"derivedFrom":subQ1}),1.0]])]});}
            var Q130;
            {var subQ6=sQuery(id+"F2.wireOp",EDGE,"E86.150.9.0");Q130=makeQuery(id+"F2.imprint","IMPRINT",FACE,{"disambiguationData":[TD([[makeQuery(id+"F2.imprint","IMPRINT",EDGE,{"derivedFrom":subQ6}),-1.0]])]});}
            var Q131;
            {var subQ1=sQuery(id+"F2.wireOp",EDGE,"E86.114.9.0");Q131=makeQuery(id+"F2.imprint","IMPRINT",FACE,{"disambiguationData":[TD([[makeQuery(id+"F2.imprint","IMPRINT",EDGE,{"derivedFrom":subQ1}),1.0]])]});}
            var Q132;
            {var subQ7=sQuery(id+"F2.wireOp",EDGE,"E86.150.10.0");Q132=makeQuery(id+"F2.imprint","IMPRINT",FACE,{"disambiguationData":[TD([[makeQuery(id+"F2.imprint","IMPRINT",EDGE,{"derivedFrom":subQ7}),-1.0]])]});}
            var Q133;
            {var subQ1=sQuery(id+"F2.wireOp",EDGE,"E86.114.10.0");Q133=makeQuery(id+"F2.imprint","IMPRINT",FACE,{"disambiguationData":[TD([[makeQuery(id+"F2.imprint","IMPRINT",EDGE,{"derivedFrom":subQ1}),1.0]])]});}
            var Q134;
            {var subQ6=sQuery(id+"F2.wireOp",EDGE,"E86.150.11.0");Q134=makeQuery(id+"F2.imprint","IMPRINT",FACE,{"disambiguationData":[TD([[makeQuery(id+"F2.imprint","IMPRINT",EDGE,{"derivedFrom":subQ6}),-1.0]])]});}
            var Q135;
            {var subQ1=sQuery(id+"F2.wireOp",EDGE,"E86.114.11.0");Q135=makeQuery(id+"F2.imprint","IMPRINT",FACE,{"disambiguationData":[TD([[makeQuery(id+"F2.imprint","IMPRINT",EDGE,{"derivedFrom":subQ1}),1.0]])]});}
            var Q136;
            {var subQ6=sQuery(id+"F2.wireOp",EDGE,"E86.150.12.0");Q136=makeQuery(id+"F2.imprint","IMPRINT",FACE,{"disambiguationData":[TD([[makeQuery(id+"F2.imprint","IMPRINT",EDGE,{"derivedFrom":subQ6}),-1.0]])]});}
            var Q137;
            {var subQ1=sQuery(id+"F2.wireOp",EDGE,"E86.114.12.0");Q137=makeQuery(id+"F2.imprint","IMPRINT",FACE,{"disambiguationData":[TD([[makeQuery(id+"F2.imprint","IMPRINT",EDGE,{"derivedFrom":subQ1}),1.0]])]});}
            var Q138;
            {var subQ8=sQuery(id+"F2.wireOp",EDGE,"E86.150.13.0");Q138=makeQuery(id+"F2.imprint","IMPRINT",FACE,{"disambiguationData":[TD([[makeQuery(id+"F2.imprint","IMPRINT",EDGE,{"derivedFrom":subQ8}),-1.0]])]});}
            var Q139;
            {var subQ5=sQuery(id+"F2.wireOp",EDGE,"E86.114.13.0");Q139=makeQuery(id+"F2.imprint","IMPRINT",FACE,{"disambiguationData":[TD([[makeQuery(id+"F2.imprint","IMPRINT",EDGE,{"derivedFrom":subQ5}),1.0]])]});}
            var Q140;
            {var subQ4=sQuery(id+"F2.wireOp",EDGE,"E86.150.14.0");Q140=makeQuery(id+"F2.imprint","IMPRINT",FACE,{"disambiguationData":[TD([[makeQuery(id+"F2.imprint","IMPRINT",EDGE,{"derivedFrom":subQ4}),-1.0]])]});}
            var Q141;
            {var subQ1=sQuery(id+"F2.wireOp",EDGE,"E86.114.14.0");Q141=makeQuery(id+"F2.imprint","IMPRINT",FACE,{"disambiguationData":[TD([[makeQuery(id+"F2.imprint","IMPRINT",EDGE,{"derivedFrom":subQ1}),1.0]])]});}
            extrude(context, id + "F3", {"entities" : qUnion([Q0, Q1, Q2, Q3, Q4, Q5, Q6, Q7, Q8, Q9, Q10, Q11, Q12, Q13, Q14, Q15, Q16, Q17, Q18, Q19, Q20, Q21, Q22, Q23, Q24, Q25, Q26, Q27, Q28, Q29, Q30, Q31, Q32, Q33, Q34, Q35, Q36, Q37, Q38, Q39, Q40, Q41, Q42, Q43, Q44, Q45, Q46, Q47, Q48, Q49, Q50, Q51, Q52, Q53, Q54, Q55, Q56, Q57, Q58, Q59, Q60, Q61, Q62, Q63, Q64, Q65, Q66, Q67, Q68, Q69, Q70, Q71, Q72, Q73, Q74, Q75, Q76, Q77, Q78, Q79, Q80, Q81, Q82, Q83, Q84, Q85, Q86, Q87, Q88, Q89, Q90, Q91, Q92, Q93, Q94, Q95, Q96, Q97, Q98, Q99, Q100, Q101, Q102, Q103, Q104, Q105, Q106, Q107, Q108, Q109, Q110, Q111, Q112, Q113, Q114, Q115, Q116, Q117, Q118, Q119, Q120, Q121, Q122, Q123, Q124, Q125, Q126, Q127, Q128, Q129, Q130, Q131, Q132, Q133, Q134, Q135, Q136, Q137, Q138, Q139, Q140, Q141]), "operationType" : NewBodyOperationType.ADD, "depth" : 1.2 * mm});
        }
        {
            var Q0;
            Q0=qCreatedBy(makeId("Front.planeOp"),FACE);
            var sketch = newSketch(context, id + "F4", { "sketchPlane" : qUnion([Q0])});
            skLineSegment(sketch, "E92", {"start": v(0, 0) * mm, "end": v(0, 1.65) * mm, "construction": true});
            skLineSegment(sketch, "E93", {"start": v(0, 1.65) * mm, "end": v(41.85, 1.65) * mm, "construction": true});
            skCircle(sketch, "E94", {"center": v(41.85, 1.65) * mm, "radius": 1.65 * mm});
            skLineSegment(sketch, "E95", {"start": v(0, 0) * mm, "end": v(43.5, 0) * mm});
            skLineSegment(sketch, "E96", {"start": v(43.5, 1.54) * mm, "end": v(43.5, 1.77) * mm});
            skPoint(sketch, "E97.end.orphan", {"position": v(40.2, 0) * mm});
            skLineSegment(sketch, "E98", {"start": v(40.2, 1.65) * mm, "end": v(39.93, 0) * mm});
            skLineSegment(sketch, "E99", {"start": v(43.5, 0) * mm, "end": v(43.7, 0) * mm});
            skLineSegment(sketch, "E100", {"start": v(43.7, 0) * mm, "end": v(43.5, 1.77) * mm});
            skSolve(sketch);
        }
        {
            var Q0;
            Q0=makeQuery(id+"F4.imprint","IMPRINT",FACE,{"disambiguationData":[TD([[makeQuery(id+"F4.imprint","IMPRINT",EDGE,{"derivedFrom":sQuery(id+"F4.wireOp",EDGE,"E94")}),1.0]])]});
            extrude(context, id + "F5", {"entities" : qUnion([Q0]), "operationType" : NewBodyOperationType.ADD, "endBound" : BoundingType.SYMMETRIC, "depth" : 25 * mm});
        }
        {
            var Q0;
            {var subQ0=sQuery(id+"F4.wireOp",EDGE,"E98");Q0=makeQuery(id+"F4.imprint","IMPRINT",FACE,{"disambiguationData":[TD([[makeQuery(id+"F4.imprint","IMPRINT",EDGE,{"derivedFrom":subQ0}),1.0]])]});}
            var Q1;
            {var subQ0=sQuery(id+"F4.wireOp",EDGE,"E99");Q1=makeQuery(id+"F4.imprint","IMPRINT",FACE,{"disambiguationData":[TD([[makeQuery(id+"F4.imprint","IMPRINT",EDGE,{"derivedFrom":subQ0}),1.0]])]});}
            extrude(context, id + "F6", {"entities" : qUnion([Q0, Q1]), "operationType" : NewBodyOperationType.REMOVE, "endBound" : BoundingType.SYMMETRIC, "oppositeDirection" : true, "depth" : 18.5 * mm});
        }
        {
            var Q0;
            {var subQ0=sQuery(id+"F4.wireOp",EDGE,"E98");Q0=makeQuery(id+"F4.imprint","IMPRINT",FACE,{"disambiguationData":[TD([[makeQuery(id+"F4.imprint","IMPRINT",EDGE,{"derivedFrom":subQ0}),1.0]])]});}
            extrude(context, id + "F7", {"entities" : qUnion([Q0]), "operationType" : NewBodyOperationType.ADD, "endBound" : BoundingType.SYMMETRIC, "depth" : 5.5 * mm});
        }
        {
            var Q0;
            Q0=makeQuery(id+"F1.opExtrude","SWEPT_FACE",FACE,{"disambiguationData":[OSD([sQuery(id+"F0.wireOp",EDGE,"E0.top")])]});
            cPlane(context, id + "F8", {"entities" : qUnion([Q0]), "cplaneType" : CPlaneType.OFFSET, "offset" : 0 * mm, "width" : 150 * mm, "height" : 150 * mm});
        }
        {
            var Q0;
            Q0=qCreatedBy(id+"F8.planeOp",FACE);
            var sketch = newSketch(context, id + "F9", { "sketchPlane" : qUnion([Q0])});
            skLineSegment(sketch, "E101", {"start": v(0, 0) * mm, "end": v(0, 1.65) * mm, "construction": true});
            skLineSegment(sketch, "E102", {"start": v(0, 1.65) * mm, "end": v(41.85, 1.55) * mm, "construction": true});
            skArc(sketch, "E103", {"start": v(44.76, 0) * mm, "mid": v(41.85, 4.85) * mm, "end": v(38.94, 0) * mm});
            skLineSegment(sketch, "E104", {"start": v(44.76, 0) * mm, "end": v(38.94, 0) * mm});
            skSolve(sketch);
        }
        {
            var Q0;
            Q0=qSketchRegion(id+"F9",true);
            extrude(context, id + "F10", {"entities" : qUnion([Q0]), "operationType" : NewBodyOperationType.ADD, "oppositeDirection" : true, "depth" : 1.5 * mm});
        }
        {
            var Q0;
            Q0=makeQuery(id+"F1.opExtrude","SWEPT_FACE",FACE,{"disambiguationData":[OSD([sQuery(id+"F0.wireOp",EDGE,"E0.bottom")])]});
            cPlane(context, id + "F11", {"entities" : qUnion([Q0]), "cplaneType" : CPlaneType.OFFSET, "offset" : 0 * mm, "width" : 150 * mm, "height" : 150 * mm});
        }
        {
            var Q0;
            Q0=qCreatedBy(id+"F11.planeOp",FACE);
            var sketch = newSketch(context, id + "F12", { "sketchPlane" : qUnion([Q0])});
            skLineSegment(sketch, "E105", {"start": v(0, 0) * mm, "end": v(0, 1.65) * mm, "construction": true});
            skLineSegment(sketch, "E106", {"start": v(0, 1.65) * mm, "end": v(-41.85, 1.65) * mm, "construction": true});
            skArc(sketch, "E107", {"start": v(-39, 0) * mm, "mid": v(-41.85, 4.95) * mm, "end": v(-44.7, 0) * mm});
            skLineSegment(sketch, "E108", {"start": v(-39, 0) * mm, "end": v(-44.7, 0) * mm});
            skSolve(sketch);
        }
        {
            var Q0;
            Q0=qSketchRegion(id+"F12",true);
            extrude(context, id + "F13", {"entities" : qUnion([Q0]), "operationType" : NewBodyOperationType.ADD, "oppositeDirection" : true, "depth" : 1.5 * mm});
        }
        {
            var Q0;
            Q0=qCreatedBy(makeId("Front.planeOp"),FACE);
            var sketch = newSketch(context, id + "F14", { "sketchPlane" : qUnion([Q0])});
            skLineSegment(sketch, "E109", {"start": v(0, 0) * mm, "end": v(0, 3.3) * mm, "construction": true});
            skLineSegment(sketch, "E110", {"start": v(0, 3.3) * mm, "end": v(-45.25, 3.3) * mm, "construction": true});
            skArc(sketch, "E111", {"start": v(-48.84, 1.78) * mm, "mid": v(-48.22, 0.77) * mm, "end": v(-47.33, 0) * mm});
            skArc(sketch, "E112", {"start": v(-46.6, 1.9) * mm, "mid": v(-43.3, 3.3) * mm, "end": v(-46.6, 4.7) * mm});
            skLineSegment(sketch, "E113", {"start": v(-45.25, 3.3) * mm, "end": v(-46.1, 3.3) * mm, "construction": true});
            skLineSegment(sketch, "E114", {"start": v(-46.1, 3.3) * mm, "end": v(-46.1, 1.58) * mm});
            skLineSegment(sketch, "E115", {"start": v(-47.33, 0) * mm, "end": v(-43.17, 0) * mm});
            skArc(sketch, "E116.trimOffspring", {"start": v(-43.17, 0) * mm, "mid": v(-42.72, 6.27) * mm, "end": v(-48.84, 4.83) * mm});
            skPoint(sketch, "E117.orphan", {"position": v(-47.57, 0) * mm});
            skCircle(sketch, "E118", {"center": v(-45.25, 3.3) * mm, "radius": 1.95 * mm});
            skCircle(sketch, "E119", {"center": v(-45.25, 3.3) * mm, "radius": 3.9 * mm});
            skLineSegment(sketch, "E120", {"start": v(-47.2, 3.3) * mm, "end": v(-43.77, 4.57) * mm});
            skLineSegment(sketch, "E121", {"start": v(-47.2, 3.3) * mm, "end": v(-48.52, 5.42) * mm});
            skLineSegment(sketch, "E122", {"start": v(-43.77, 4.57) * mm, "end": v(-44.14, 7.04) * mm});
            skLineSegment(sketch, "E123", {"start": v(-41.4, 3.93) * mm, "end": v(-40.46, 0) * mm});
            skLineSegment(sketch, "E124", {"start": v(-40.46, 0) * mm, "end": v(-43.17, 0) * mm});
            skSolve(sketch);
        }
        {
            var Q0;
            {var subQ1=sQuery(id+"F14.wireOp",EDGE,"E115");Q0=makeQuery(id+"F14.imprint","IMPRINT",FACE,{"disambiguationData":[TD([[makeQuery(id+"F14.imprint","IMPRINT",EDGE,{"derivedFrom":subQ1}),1.0]])]});}
            var Q1;
            {var subQ2=sQuery(id+"F14.wireOp",EDGE,"E123");Q1=makeQuery(id+"F14.imprint","IMPRINT",FACE,{"disambiguationData":[TD([[makeQuery(id+"F14.imprint","IMPRINT",EDGE,{"derivedFrom":subQ2}),-1.0]])]});}
            extrude(context, id + "F15", {"entities" : qUnion([Q0, Q1]), "operationType" : NewBodyOperationType.ADD, "endBound" : BoundingType.SYMMETRIC, "depth" : 18 * mm});
        }
        {
            var Q0;
            {var subQ1=sQuery(id+"F14.wireOp",EDGE,"E115");Q0=makeQuery(id+"F14.imprint","IMPRINT",FACE,{"disambiguationData":[TD([[makeQuery(id+"F14.imprint","IMPRINT",EDGE,{"derivedFrom":subQ1}),1.0]])]});}
            var Q1;
            {var subQ2=sQuery(id+"F14.wireOp",EDGE,"E123");Q1=makeQuery(id+"F14.imprint","IMPRINT",FACE,{"disambiguationData":[TD([[makeQuery(id+"F14.imprint","IMPRINT",EDGE,{"derivedFrom":subQ2}),-1.0]])]});}
            extrude(context, id + "F16", {"entities" : qUnion([Q0, Q1]), "operationType" : NewBodyOperationType.REMOVE, "endBound" : BoundingType.SYMMETRIC, "depth" : 9 * mm});
        }
    });
